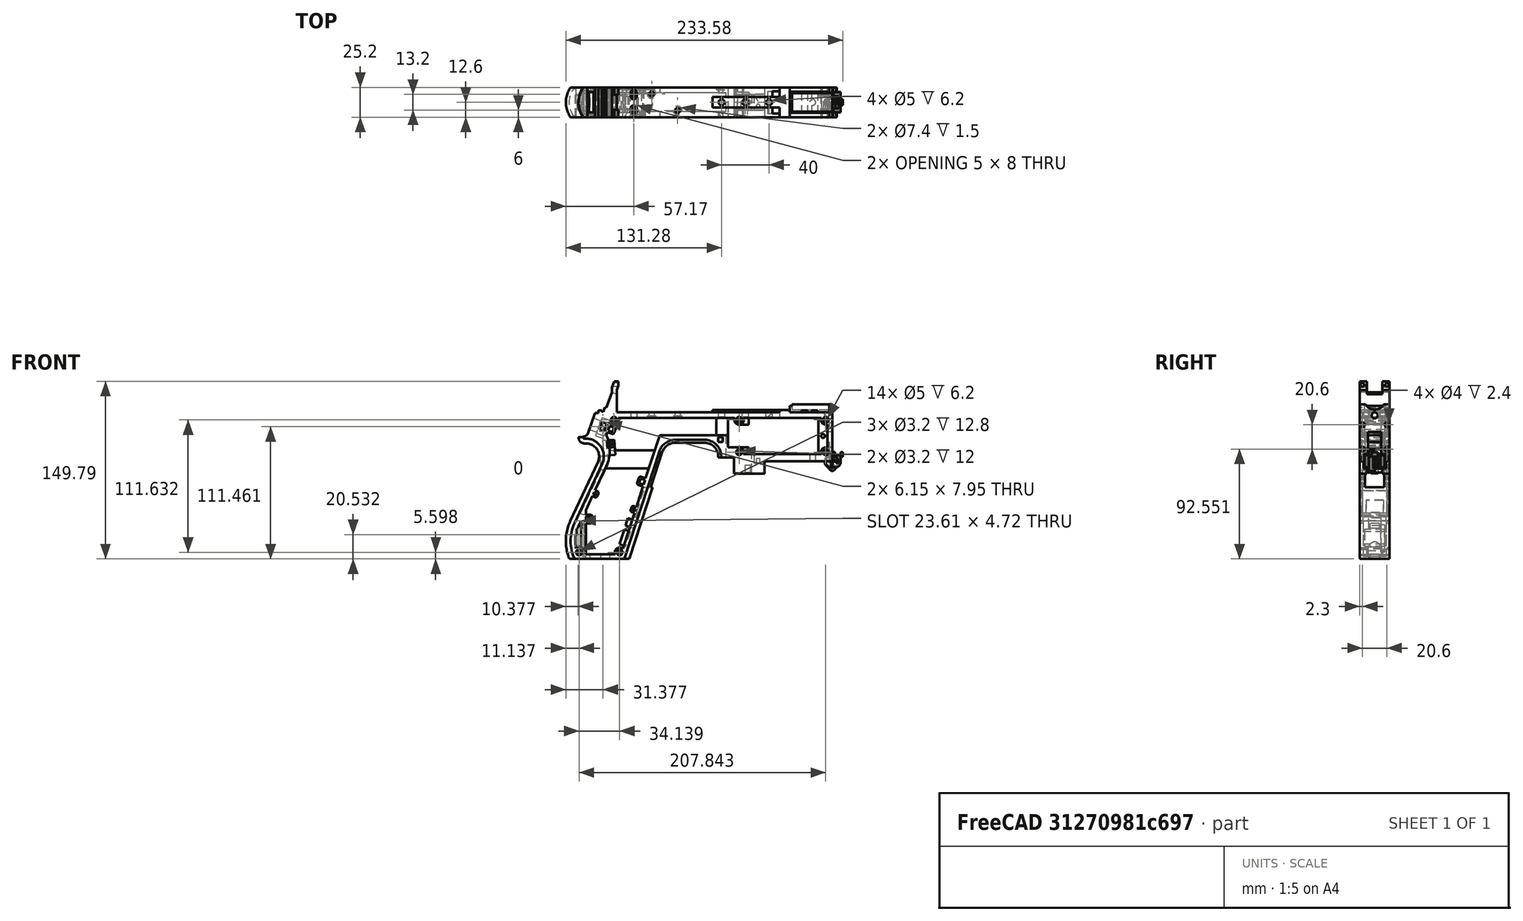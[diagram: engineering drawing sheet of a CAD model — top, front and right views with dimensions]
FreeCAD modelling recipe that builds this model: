
FCSTD DOCUMENT  (FreeCAD 1.0R39319 (Git))
Label: PICON-OF_ver_43
License: All rights reserved
LicenseURL: https://en.wikipedia.org/wiki/All_rights_reserved
objects: Sketcher::SketchObject×112, Part::Extrusion×55, Part::Cut×39, PartDesign::Pad×29, PartDesign::Pocket×18, PartDesign::Chamfer×15, PartDesign::Body×10, PartDesign::Fillet×6, PartDesign::SubtractivePipe×4, Part::Part2DObjectPython×4, PartDesign::SubtractiveLoft×4, PartDesign::Plane×2, PartDesign::SubShapeBinder×2, Part::Sweep×1, PartDesign::ShapeBinder×1, Part::MultiFuse×1, Mesh::Feature×1
note: 567 computed .brp shape members not serialized (recipe doc carries the construction recipe); baked Part::Feature solids carry a one-line shape summary decoded from their .brp

FEATURE [Sketcher::SketchObject] Sketch  label="corpo principale"
  ArcFitTolerance = 1e-06
  AttacherType = Attacher::AttachEngine3D
  AttachmentSupport = -> [XZ_Plane]
  FullyConstrained = true
  MakeInternals = false
  MapMode = 5
  Placement = pos=(0,0,0) rot=(1,0,0;1.5708rad)
  sketch-geometry (65):
    g0: LineSegment StartX=0 StartY=0 StartZ=0 EndX=-57.2 EndY=0 EndZ=0
    g1: LineSegment StartX=-57.2 StartY=0 StartZ=0 EndX=-57.2 EndY=-10.4 EndZ=0
    g2: LineSegment StartX=-57.2 StartY=-10.4 StartZ=0 EndX=-82.8 EndY=-10.4 EndZ=0
    g3: LineSegment StartX=-82.8 StartY=-10.4 StartZ=0 EndX=-82.8 EndY=3.2 EndZ=0
    g4: LineSegment StartX=-82.8 StartY=3.2 StartZ=0 EndX=-93.6 EndY=3.2 EndZ=0
    g5: LineSegment StartX=-93.6 StartY=3.2 StartZ=0 EndX=-93.6 EndY=4 EndZ=0
    g6: LineSegment StartX=-107.6 StartY=18 StartZ=0 EndX=-132.428 EndY=18 EndZ=0
    g7: LineSegment StartX=-145.743 StartY=8.32624 StartZ=0 EndX=-175.232 EndY=-82.4316 EndZ=0
    g8: LineSegment StartX=-175.232 StartY=-82.4316 StartZ=0 EndX=-217.232 EndY=-82.4316 EndZ=0
    g9: LineSegment StartX=-217.232 StartY=-52.1862 StartZ=0 EndX=-193.988 EndY=-2.33927 EndZ=0
    g10: LineSegment StartX=-206.196 StartY=23.0857 StartZ=0 EndX=-199.861 EndY=40.4914 EndZ=0
    g11: LineSegment StartX=-199.861 StartY=40.4914 StartZ=0 EndX=-197.061 EndY=40.4914 EndZ=0
    g12: LineSegment StartX=-197.061 StartY=40.4914 StartZ=0 EndX=-197.061 EndY=42.8914 EndZ=0
    g13: LineSegment StartX=-197.061 StartY=42.8914 StartZ=0 EndX=-194.261 EndY=42.8914 EndZ=0
    g14: LineSegment StartX=-194.261 StartY=42.8914 StartZ=0 EndX=-194.535 EndY=42.1397 EndZ=0
    g15: LineSegment StartX=-194.535 StartY=42.1397 StartZ=0 EndX=-193.031 EndY=41.5924 EndZ=0
    g16: LineSegment StartX=-193.031 StartY=41.5924 StartZ=0 EndX=-191.663 EndY=45.3512 EndZ=0
    g17: LineSegment StartX=-191.663 StartY=45.3512 StartZ=0 EndX=-190.536 EndY=44.9408 EndZ=0
    g18: LineSegment StartX=-190.536 StartY=44.9408 StartZ=0 EndX=-185.747 EndY=58.0965 EndZ=0
    g19: LineSegment StartX=-185.747 StartY=58.0965 StartZ=0 EndX=-185.747 EndY=62.0965 EndZ=0
    g20: LineSegment StartX=-185.747 StartY=62.0965 StartZ=0 EndX=-183.832 EndY=67.3588 EndZ=0
    g21: LineSegment StartX=-183.832 StartY=67.3588 StartZ=0 EndX=-180.232 EndY=67.3588 EndZ=0
    g22: LineSegment StartX=-180.232 StartY=67.3588 StartZ=0 EndX=-180.232 EndY=63.7588 EndZ=0
    g23: LineSegment StartX=-180.232 StartY=63.7588 StartZ=0 EndX=-181.6 EndY=60 EndZ=0
    g24: LineSegment StartX=-181.6 StartY=60 StartZ=0 EndX=-181.6 EndY=41.2 EndZ=0
    g25: LineSegment StartX=-181.6 StartY=41.2 StartZ=0 EndX=-100.8 EndY=41.2 EndZ=0
    g26: LineSegment StartX=-36 StartY=43.2 StartZ=0 EndX=-36 EndY=41.2 EndZ=0
    g27: LineSegment StartX=0 StartY=48 StartZ=0 EndX=0 EndY=0 EndZ=0
    g28: LineSegment StartX=-209.901 StartY=19.85 StartZ=0 EndX=-209.901 EndY=20.1 EndZ=0
    g29: LineSegment StartX=-208.001 StartY=22 StartZ=0 EndX=-207.747 EndY=22 EndZ=0
    g30: LineSegment StartX=-207.583 StartY=19 StartZ=0 EndX=-209.051 EndY=19 EndZ=0
    g31: ArcOfCircle CenterX=-208.001 CenterY=20.1 CenterZ=0 NormalX=0 NormalY=0 NormalZ=1 AngleXU=0 Radius=1.9 StartAngle=1.5708 EndAngle=3.14159
    g32: GeomPoint [constr] X=-209.901 Y=22 Z=0
    g33: ArcOfCircle CenterX=-209.051 CenterY=19.85 CenterZ=0 NormalX=0 NormalY=0 NormalZ=1 AngleXU=0 Radius=0.85 StartAngle=3.14159 EndAngle=4.71239
    g34: GeomPoint [constr] X=-209.901 Y=19 Z=0
    g35: ArcOfCircle CenterX=-207.747 CenterY=23.65 CenterZ=0 NormalX=0 NormalY=0 NormalZ=1 AngleXU=0 Radius=1.65 StartAngle=4.71239 EndAngle=5.93412
    g36: GeomPoint [constr] X=-206.591 Y=22 Z=0
    g37: LineSegment StartX=-4 StartY=6 StartZ=0 EndX=-4 EndY=36.4 EndZ=0
    g38: LineSegment StartX=-4 StartY=36.4 StartZ=0 EndX=-185.2 EndY=36.4 EndZ=0
    g39: LineSegment StartX=-185.2 StartY=36.4 StartZ=0 EndX=-190.441 EndY=22 EndZ=0
    g40: LineSegment StartX=-214.575 StartY=-78.4316 StartZ=0 EndX=-178.142 EndY=-78.4316 EndZ=0
    g41: LineSegment StartX=-178.142 StartY=-78.4316 StartZ=0 EndX=-145.51 EndY=22 EndZ=0
    g42: LineSegment StartX=-145.51 StartY=22 StartZ=0 EndX=-87.91 EndY=22 EndZ=0
    g43: LineSegment StartX=-87.91 StartY=22 StartZ=0 EndX=-87.91 EndY=11.6 EndZ=0
    g44: LineSegment StartX=-87.91 StartY=11.6 StartZ=0 EndX=-80.11 EndY=11.6 EndZ=0
    g45: LineSegment StartX=-80.11 StartY=11.6 StartZ=0 EndX=-80.11 EndY=6 EndZ=0
    g46: LineSegment StartX=-80.11 StartY=6 StartZ=0 EndX=-4 EndY=6 EndZ=0
    g47: LineSegment StartX=-190.363 StartY=-4.02975 StartZ=0 EndX=-213.607 EndY=-53.8767 EndZ=0
    g48: ArcOfCircle CenterX=-132.428 CenterY=4 CenterZ=0 NormalX=0 NormalY=0 NormalZ=1 AngleXU=0 Radius=14 StartAngle=1.5708 EndAngle=2.82743
    g49: GeomPoint [constr] X=-142.6 Y=18 Z=0
    g50: ArcOfCircle CenterX=-107.6 CenterY=4 CenterZ=0 NormalX=0 NormalY=0 NormalZ=1 AngleXU=0 Radius=14 StartAngle=0 EndAngle=1.5708
    g51: GeomPoint [constr] X=-93.6 Y=18 Z=0
    g52: ArcOfCircle CenterX=-184.801 CenterY=-67.3089 CenterZ=0 NormalX=0 NormalY=0 NormalZ=1 AngleXU=0 Radius=35.7833 StartAngle=2.70526 EndAngle=3.57792
    g53: ArcOfCircle CenterX=-207.583 CenterY=4 CenterZ=0 NormalX=0 NormalY=0 NormalZ=1 AngleXU=0 Radius=15 StartAngle=5.84685 EndAngle=7.85398
    g54: LineSegment [constr] StartX=-213.607 StartY=-53.8767 StartZ=0 EndX=-217.232 EndY=-52.1862 EndZ=0
    g55: ArcOfCircle CenterX=-184.801 CenterY=-67.3089 CenterZ=0 NormalX=0 NormalY=0 NormalZ=1 AngleXU=0 Radius=31.7833 StartAngle=2.70526 EndAngle=3.49911
    g56: ArcOfCircle CenterX=-218.095 CenterY=8.90192 CenterZ=0 NormalX=0 NormalY=0 NormalZ=1 AngleXU=0 Radius=30.5989 StartAngle=5.84685 EndAngle=6.72553
    g57: LineSegment StartX=-44.6 StartY=43.2 StartZ=0 EndX=-36 EndY=43.2 EndZ=0
    g58: LineSegment StartX=-100.8 StartY=41.2 StartZ=0 EndX=-44.6 EndY=41.2 EndZ=0
    g59: LineSegment StartX=-44.6 StartY=41.2 StartZ=0 EndX=-44.6 EndY=43.2 EndZ=0
    g60: LineSegment StartX=-2.4 StartY=48 StartZ=0 EndX=0 EndY=48 EndZ=0
    g61: LineSegment StartX=-36 StartY=41.2 StartZ=0 EndX=-2.4 EndY=41.2 EndZ=0
    g62: LineSegment StartX=-2.4 StartY=41.2 StartZ=0 EndX=-2.4 EndY=48 EndZ=0
    g63: LineSegment [constr] StartX=-181.6 StartY=36.4 StartZ=0 EndX=-152.209 EndY=36.4 EndZ=0
    g64: LineSegment [constr] StartX=-181.6 StartY=36.4 StartZ=0 EndX=-130.41 EndY=36.4 EndZ=0
  constraints (183):
    c: Coincident(g-1,g0)
    c: PointOnObject(g0,g-1)
    c: Coincident(g0,g1)
    c: Vertical(g1)
    c: Coincident(g1,g2)
    c: Horizontal(g2)
    c: Coincident(g2,g3)
    c: Vertical(g3)
    c: Coincident(g3,g4)
    c: Coincident(g4,g5)
    c: Vertical(g5)
    c: Horizontal(g6)
    c: Coincident(g7,g8)
    c: Horizontal(g8)
    c: Coincident(g10,g11)
    c: Horizontal(g11)
    c: Coincident(g11,g12)
    c: Vertical(g12)
    c: Coincident(g12,g13)
    c: Horizontal(g13)
    c: Coincident(g13,g14)
    c: Coincident(g14,g15)
    c: Coincident(g15,g16)
    c: Coincident(g16,g17)
    c: Coincident(g17,g18)
    c: Coincident(g18,g19)
    c: Vertical(g19)
    c: Coincident(g19,g20)
    c: Coincident(g20,g21)
    c: Horizontal(g21)
    c: Coincident(g21,g22)
    c: Vertical(g22)
    c: Coincident(g22,g23)
    c: Coincident(g23,g24)
    c: Vertical(g24)
    c: Coincident(g24,g25)
    c: Horizontal(g25)
    c: Coincident(g57,g26)
    c: Vertical(g26)
    c: Coincident(g26,g61)
    c: PointOnObject(g60,g-2)
    c: Coincident(g60,g27)
    c: Coincident(g27,g0)
    c: DistanceY(g27,g27) = 48
    c: DistanceY(g1,g1) = 10.4
    c: DistanceX(g0,g0) = 57.2
    c: DistanceX(g2,g2) = 25.6
    c: Horizontal(g4)
    c: DistanceY(g3,g3) = 13.6
    c: DistanceX(g4,g4) = 10.8
    c: DistanceY(g5,g51) = 14.8
    c: DistanceX(g49,g51) = 49
    c: Distance(g7,g49) = 105.6
    c: DistanceX(g61,g60) = 36
    c: DistanceX(g25,g25) = 80.8
    c: DistanceY(g24,g24) = 18.8
    c: DistanceY(g22,g22) = 3.6
    c: Distance(g23) = 4
    c: Angle(g-1,g23) = 1.22173
    c: DistanceX(g21,g21) = 3.6
    c: Distance(g20) = 5.6
    c: Angle(g-1,g20) = 1.22173
    c: DistanceY(g19,g19) = 4
    c: Distance(g18) = 14
    c: Angle(g-1,g18) = 1.22173
    c: Distance(g17) = 1.2
    c: Distance(g16) = 4
    c: Angle(g16) = 1.22173
    c: Perpendicular(g18,g17)
    c: Distance(g15) = 1.6
    c: Perpendicular(g16,g15)
    c: Distance(g14) = 0.8
    c: DistanceX(g13,g13) = 2.8
    c: Perpendicular(g15,g14)
    c: DistanceY(g12,g12) = 2.4
    c: DistanceX(g11,g11) = 2.8
    c: Distance(g9) = 55
    c: Angle(g9,g-1) = 2.00713
    c: Horizontal(g29)
    c: Vertical(g28)
    c: Horizontal(g30)
    c: PointOnObject(g32,g29)
    c: PointOnObject(g32,g28)
    c: Tangent(g29,g31) = 1.5708
    c: Tangent(g28,g31) = 1.5708
    c: PointOnObject(g34,g28)
    c: PointOnObject(g34,g30)
    c: Tangent(g28,g33) = 1.5708
    c: Tangent(g30,g33) = 1.5708
    c: PointOnObject(g36,g29)
    c: PointOnObject(g36,g10)
    c: Tangent(g29,g35) = -1.5708
    c: Tangent(g10,g35) = -1.5708
    c: Angle(g-1,g10) = 1.22173
    c: Radius(g35) = 1.65
    c: Vertical(g37)
    c: Coincident(g37,g38)
    c: Horizontal(g38)
    c: Coincident(g38,g39)
    c: Horizontal(g40)
    c: Coincident(g40,g41)
    c: Coincident(g41,g42)
    c: Horizontal(g42)
    c: Coincident(g42,g43)
    c: Vertical(g43)
    c: Coincident(g43,g44)
    c: Horizontal(g44)
    c: Coincident(g44,g45)
    c: Vertical(g45)
    c: Coincident(g45,g46)
    c: Coincident(g46,g37)
    c: Horizontal(g46)
    c: DistanceY(g0,g37) = 6
    c: DistanceX(g37,g0) = 4
    c: DistanceY(g37,g25) = 4.8
    c: DistanceX(g38,g38) = 181.2
    c: DistanceX(g42,g42) = 57.6
    c: DistanceY(g49,g41) = 4
    c: DistanceX(g41,g49) = 2.91
    c: DistanceY(g43,g43) = 10.4
    c: DistanceX(g44,g44) = 7.8
    c: DistanceY(g7,g40) = 4
    c: Distance(g47) = 55
    c: Angle(g-1,g39) = 1.22173
    c: PointOnObject(g49,g7)
    c: PointOnObject(g49,g6)
    c: Tangent(g7,g48) = -1.5708
    c: Tangent(g6,g48) = -1.5708
    c: PointOnObject(g51,g5)
    c: PointOnObject(g51,g6)
    c: Tangent(g5,g50) = -1.5708
    c: Tangent(g6,g50) = -1.5708
    c: Radius(g50) = 14
    c: Radius(g48) = 14
    c: DistanceX(g8,g8) = 42
    c: Angle(g7,g-1) = 1.88496
    c: Parallel(g41,g7)
    c: Parallel(g47,g9)
    c: Coincident(g52,g8)
    c: Tangent(g52,g9) = 1.5708
    c: DistanceX(g9,g8) = 0
    c: Tangent(g53,g9) = -1.5708
    c: Tangent(g53,g30) = -1.5708
    c: Diameter(g53) = 30
    c: DistanceY(g53,g0) = -4
    c: Coincident(g54,g47)
    c: Distance(g54) = 4
    c: Coincident(g54,g9)
    c: Coincident(g55,g40)
    c: Tangent(g55,g47) = -1.5708
    c: Coincident(g52,g55)
    c: Coincident(g56,g39)
    c: Tangent(g56,g47) = 1.5708
    c: Horizontal(g57)
    c: DistanceX(g57,g57) = 8.6
    c: Coincident(g58,g25)
    c: Horizontal(g58)
    c: Coincident(g59,g58)
    c: Vertical(g59)
    c: DistanceY(g58,g57) = 2
    c: DistanceX(g58,g58) = 56.2
    c: Coincident(g59,g57)
    c: DistanceY(g41,g36) = 0
    c: DistanceY(g36,g39) = 0
    c: DistanceY(g28,g28) = 0.25
    c: DistanceX(g30,g36) = 2.46
    c: DistanceX(g28,g29) = 1.9
    c: Coincident(g62,g60)
    c: Horizontal(g60)
    c: DistanceX(g62,g27) = 2.4
    c: Coincident(g61,g62)
    c: DistanceY(g26,g26) = 2
    c: Vertical(g62)
    c: DistanceY(g61,g60) = 6.8
    c: Horizontal(g61)
    c: Distance(g63) = 29.391
    c: PointOnObject(g63,g38)
    c: PointOnObject(g63,g38)
    c: Distance(g64) = 51.19
    c: PointOnObject(g64,g38)
    c: PointOnObject(g64,g38)
    c: DistanceX(g24,g63) = 0
    c: DistanceX(g24,g64) = 0
FEATURE [Part::Extrusion] Extrude  label="Extrude corpo principale"
  Base = -> Sketch
  Dir = (0,-1,2e-16)
  DirMode = 2
  FaceMakerClass = Part::FaceMakerBullseye
  FaceMakerMode = 3
  LengthFwd = 25.2
  LengthRev = 12.6
  Solid = true
  Symmetric = true
FEATURE [Sketcher::SketchObject] Sketch002  label="scavo grilletto"
  ArcFitTolerance = 1e-06
  AttachmentSupport = -> [XZ_Plane]
  ExternalGeometry = -> [Sketch]
  FullyConstrained = true
  MakeInternals = false
  MapMode = 5
  Placement = pos=(0,0,0) rot=(1,0,0;1.5708rad)
  sketch-geometry (4):
    g0: LineSegment StartX=-89.51 StartY=22 StartZ=0 EndX=-152.71 EndY=22 EndZ=0
    g1: LineSegment StartX=-152.71 StartY=22 StartZ=0 EndX=-167.006 EndY=-22 EndZ=0
    g2: LineSegment StartX=-167.006 StartY=-22 StartZ=0 EndX=-89.51 EndY=-22 EndZ=0
    g3: LineSegment StartX=-89.51 StartY=-22 StartZ=0 EndX=-89.51 EndY=22 EndZ=0
  constraints (12):
    c: Horizontal(g0)
    c: Coincident(g0,g1)
    c: Coincident(g1,g2)
    c: Horizontal(g2)
    c: Coincident(g2,g3)
    c: Coincident(g3,g0)
    c: Vertical(g3)
    c: Angle(g1,g0) = 1.88496
    c: DistanceY(g3,g3) = 44
    c: DistanceX(g0,g0) = 63.2
    c: DistanceX(g0,g-3) = 1.6
    c: DistanceY(g-3,g0) = 0
FEATURE [Sketcher::SketchObject] Sketch004  label="traiettoria arrotondamento impugnatura anteriore"
  ArcFitTolerance = 1e-06
  AttachmentSupport = -> [XZ_Plane]
  ExternalGeometry = -> [Sketch]
  FullyConstrained = true
  MakeInternals = false
  MapMode = 5
  Placement = pos=(0,0,0) rot=(1,0,0;1.5708rad)
  sketch-geometry (13):
    g0: LineSegment StartX=-175.232 StartY=-82.4316 StartZ=0 EndX=-145.743 EndY=8.32624 EndZ=0
    g1: LineSegment StartX=-93.6 StartY=3.2 StartZ=0 EndX=-93.6 EndY=4 EndZ=0
    g2: LineSegment StartX=-132.428 StartY=18 StartZ=0 EndX=-107.6 EndY=18 EndZ=0
    g3: ArcOfCircle CenterX=-132.428 CenterY=4 CenterZ=0 NormalX=0 NormalY=0 NormalZ=1 AngleXU=0 Radius=14 StartAngle=1.5708 EndAngle=2.82743
    g4: ArcOfCircle CenterX=-107.6 CenterY=4 CenterZ=0 NormalX=0 NormalY=0 NormalZ=1 AngleXU=0 Radius=14 StartAngle=0 EndAngle=1.5708
    g5: LineSegment StartX=-175.232 StartY=-82.4316 StartZ=0 EndX=-217.232 EndY=-82.4316 EndZ=0
    g6: LineSegment StartX=-217.232 StartY=-52.1862 StartZ=0 EndX=-193.988 EndY=-2.33927 EndZ=0
    g7: LineSegment StartX=-209.051 StartY=19 StartZ=0 EndX=-207.583 EndY=19 EndZ=0
    g8: LineSegment StartX=-209.901 StartY=20.1 StartZ=0 EndX=-209.901 EndY=19.85 EndZ=0
    g9: ArcOfCircle CenterX=-184.801 CenterY=-67.3089 CenterZ=0 NormalX=0 NormalY=0 NormalZ=1 AngleXU=0 Radius=35.7833 StartAngle=2.70526 EndAngle=3.57792
    g10: ArcOfCircle CenterX=-207.583 CenterY=4 CenterZ=0 NormalX=0 NormalY=0 NormalZ=1 AngleXU=0 Radius=15 StartAngle=5.84685 EndAngle=7.85398
    g11: ArcOfCircle CenterX=-209.051 CenterY=19.85 CenterZ=0 NormalX=0 NormalY=0 NormalZ=1 AngleXU=0 Radius=0.85 StartAngle=3.14159 EndAngle=4.71239
    g12: ArcOfCircle CenterX=-208.001 CenterY=20.1 CenterZ=0 NormalX=0 NormalY=0 NormalZ=1 AngleXU=0 Radius=1.9 StartAngle=1.5708 EndAngle=3.14159
  constraints (26):
    c: Coincident(g0,g-3)
    c: Coincident(g0,g-6)
    c: Coincident(g1,g-8)
    c: Coincident(g1,g-7)
    c: Coincident(g2,g-5)
    c: Coincident(g2,g-4)
    c: Coincident(g3,g2)
    c: Tangent(g3,g0) = 1.5708
    c: Coincident(g4,g1)
    c: Tangent(g4,g2) = 1.5708
    c: Coincident(g5,g0)
    c: Coincident(g5,g-9)
    c: Coincident(g6,g-12)
    c: Coincident(g6,g-11)
    c: Coincident(g7,g-15)
    c: Coincident(g7,g-14)
    c: Coincident(g8,g-16)
    c: Coincident(g8,g-17)
    c: Tangent(g9,g6) = 1.5708
    c: Coincident(g9,g5)
    c: Coincident(g10,g7)
    c: Tangent(g10,g6) = -1.5708
    c: Tangent(g11,g7) = -1.5708
    c: Coincident(g11,g8)
    c: Tangent(g12,g8) = -1.5708
    c: Coincident(g12,g-17)
FEATURE [PartDesign::Plane] DatumPlane  label="Piano per disegno arrotondamento impugnatura"
  AttachmentSupport = -> [Sketch]
  Length = 73.6581
  MapMode = 7
  Placement = pos=(-145.743,1.8e-15,8.32624) rot=(0.154555,0.154555,0.97582;1.59527rad)
  ResizeMode = 0
  Width = 303.511
FEATURE [Sketcher::SketchObject] Sketch005  label="forma arrotondamento impugnatura anteriore"
  ArcFitTolerance = 1e-06
  AttachmentSupport = -> [DatumPlane]
  FullyConstrained = true
  MakeInternals = false
  MapMode = 5
  Placement = pos=(-145.743,1.8e-15,8.32624) rot=(0.154555,0.154555,0.97582;1.59527rad)
  sketch-geometry (5):
    g0: GeomPoint [constr] X=0 Y=-4 Z=0
    g1: GeomPoint [constr] X=-12.6 Y=7.1e-15 Z=0
    g2: GeomPoint [constr] X=12.6 Y=4.97e-14 Z=0
    g3: LineSegment StartX=-12.6 StartY=7.1e-15 StartZ=0 EndX=12.6 EndY=4.97e-14 EndZ=0
    g4: ArcOfCircle CenterX=-3.88e-14 CenterY=17.845 CenterZ=0 NormalX=0 NormalY=0 NormalZ=1 AngleXU=0 Radius=21.845 StartAngle=4.09759 EndAngle=5.32718
  constraints (11):
    c: DistanceY(g0,g-1) = 4
    c: DistanceX(g-1,g0) = 0
    c: DistanceX(g1,g-1) = 12.6
    c: DistanceX(g-1,g2) = 12.6
    c: DistanceY(g-1,g2) = 0
    c: DistanceY(g-1,g1) = 0
    c: Coincident(g3,g1)
    c: Coincident(g3,g2)
    c: Coincident(g4,g1)
    c: Coincident(g4,g2)
    c: PointOnObject(g0,g4)
FEATURE [Part::Sweep] Sweep  label="Sweep impugnatura"
  Frenet = true
  Sections = -> [Sketch005]
  Solid = true
  Spine = -> Sketch [Edge32,Edge33,Edge34,Edge35,Edge36,Edge37,Edge38,Edge39,Edge40,Edge41,Edge42,Edge43,Edge44]
  Transition = 1
FEATURE [Sketcher::SketchObject] Sketch008  label="buchi e pulizie varie"
  ArcFitTolerance = 1e-06
  AttachmentSupport = -> [XZ_Plane]
  ExternalGeometry = -> [Sketch]
  FullyConstrained = true
  MakeInternals = false
  MapMode = 5
  Placement = pos=(0,0,0) rot=(1,0,0;1.5708rad)
  sketch-geometry (26):
    g0: LineSegment StartX=-96.278 StartY=20.155 StartZ=0 EndX=-92.278 EndY=20.155 EndZ=0
    g1: LineSegment StartX=-92.278 StartY=20.155 StartZ=0 EndX=-92.278 EndY=16.155 EndZ=0
    g2: LineSegment StartX=-92.278 StartY=16.155 StartZ=0 EndX=-96.278 EndY=16.155 EndZ=0
    g3: LineSegment StartX=-96.278 StartY=16.155 StartZ=0 EndX=-96.278 EndY=20.155 EndZ=0
    g4: LineSegment StartX=-222.232 StartY=-82.4316 StartZ=0 EndX=-170.232 EndY=-82.4316 EndZ=0
    g5: LineSegment StartX=-170.232 StartY=-82.4316 StartZ=0 EndX=-170.232 EndY=-86.4316 EndZ=0
    g6: LineSegment StartX=-170.232 StartY=-86.4316 StartZ=0 EndX=-222.232 EndY=-86.4316 EndZ=0
    g7: LineSegment StartX=-222.232 StartY=-86.4316 StartZ=0 EndX=-222.232 EndY=-82.4316 EndZ=0
    g8: LineSegment StartX=-213.901 StartY=20.1 StartZ=0 EndX=-213.901 EndY=26 EndZ=0
    g9: LineSegment StartX=-213.901 StartY=26 StartZ=0 EndX=-206.196 EndY=26 EndZ=0
    g10: LineSegment StartX=-17.4 StartY=42.8 StartZ=0 EndX=-12.4 EndY=42.8 EndZ=0
    g11: LineSegment StartX=-12.4 StartY=42.8 StartZ=0 EndX=-12.4 EndY=41.2 EndZ=0
    g12: LineSegment StartX=-12.4 StartY=41.2 StartZ=0 EndX=-17.4 EndY=41.2 EndZ=0
    g13: LineSegment StartX=-17.4 StartY=41.2 StartZ=0 EndX=-17.4 EndY=42.8 EndZ=0
    g14: LineSegment StartX=-25.9 StartY=42.8 StartZ=0 EndX=-20.9 EndY=42.8 EndZ=0
    g15: LineSegment StartX=-20.9 StartY=42.8 StartZ=0 EndX=-20.9 EndY=41.2 EndZ=0
    g16: LineSegment StartX=-20.9 StartY=41.2 StartZ=0 EndX=-25.9 EndY=41.2 EndZ=0
    g17: LineSegment StartX=-25.9 StartY=41.2 StartZ=0 EndX=-25.9 EndY=42.8 EndZ=0
    g18: GeomPoint [constr] X=-206.196 Y=23.0857 Z=0
    g19: GeomPoint [constr] X=-213.901 Y=20.1 Z=0
    g20: BSplineCurve PolesCount=4 KnotsCount=2 Degree=3 IsPeriodic=0
    g21-g24: Circle [constr] x4 (B-spline internal-alignment scaffolding for g20; pole/knot coordinates omitted)
    g25: LineSegment StartX=-206.196 StartY=26 StartZ=0 EndX=-206.196 EndY=23.0857 EndZ=0
  constraints (73):
    c: Horizontal(g0)
    c: Coincident(g1,g0)
    c: Vertical(g1)
    c: Coincident(g2,g1)
    c: Horizontal(g2)
    c: Coincident(g3,g2)
    c: Coincident(g3,g0)
    c: Vertical(g3)
    c: DistanceX(g0,g-4) = 4.368
    c: DistanceY(g0,g-4) = 1.845
    c: DistanceY(g1,g1) = 4
    c: DistanceX(g2,g2) = 4
    c: Horizontal(g4)
    c: Coincident(g5,g4)
    c: Vertical(g5)
    c: Coincident(g6,g5)
    c: Horizontal(g6)
    c: Coincident(g7,g6)
    c: Coincident(g7,g4)
    c: Vertical(g7)
    c: DistanceY(g7,g7) = 4
    c: DistanceX(g4,g-5) = 5
    c: DistanceX(g-5,g4) = 5
    c: DistanceY(g4,g-5) = 0
    c: Coincident(g9,g8)
    c: Parallel(g9,g-6)
    c: DistanceX(g8,g-8) = 4
    c: Horizontal(g10)
    c: Coincident(g11,g10)
    c: Vertical(g11)
    c: Coincident(g12,g11)
    c: Horizontal(g12)
    c: Coincident(g13,g12)
    c: Coincident(g13,g10)
    c: Vertical(g13)
    c: Horizontal(g14)
    c: Coincident(g15,g14)
    c: Vertical(g15)
    c: Coincident(g16,g15)
    c: Horizontal(g16)
    c: Coincident(g17,g16)
    c: Coincident(g17,g14)
    c: Vertical(g17)
    c: DistanceY(g11,g10) = 1.6
    c: DistanceX(g10,g10) = 5
    c: DistanceY(g15,g14) = 1.6
    c: DistanceX(g14,g14) = 5
    c: DistanceX(g15,g12) = 3.5
    c: DistanceX(g11,g-9) = 10
    c: DistanceY(g-9,g11) = 0
    c: DistanceY(g-9,g15) = 0
    c: Perpendicular(g8,g9)
    c: DistanceY(g-7,g9) = 4
    c: DistanceY(g8,g-8) = 0
    c: InternalAlignment(g18,g20)
    c: InternalAlignment(g19,g20)
    c: InternalAlignment(g21,g20)
    c: Weight(g21) = 1
    c: InternalAlignment(g22,g20)
    c: Equal(g22,g21)
    c: InternalAlignment(g23,g20)
    c: Equal(g23,g21)
    c: InternalAlignment(g24,g20)
    c: Equal(g24,g21)
    c: Coincident(g18,g-12)
    c: Coincident(g19,g8)
    c: Coincident(g25,g9)
    c: Coincident(g25,g20)
    c: Vertical(g25)
    c: DistanceY(g20,g23) = 0
    c: DistanceY(g22,g18) = 2.26
    c: DistanceX(g22,g18) = 0.93
    c: DistanceX(g20,g23) = 2.9
FEATURE [Part::Extrusion] Extrude004  label="Extrude Buchi e pulizie varie"
  Base = -> Sketch008
  Dir = (0,-1,2e-16)
  DirMode = 2
  FaceMakerClass = Part::FaceMakerBullseye
  FaceMakerMode = 3
  LengthFwd = 25.2
  LengthRev = 0
  Solid = true
  Symmetric = true
FEATURE [Sketcher::SketchObject] Sketch009  label="rinforzi"
  ArcFitTolerance = 1e-06
  AttachmentSupport = -> [XZ_Plane]
  ExternalGeometry = -> [Sketch]
  FullyConstrained = true
  MakeInternals = false
  MapMode = 5
  Placement = pos=(0,0,0) rot=(1,0,0;1.5708rad)
  sketch-geometry (9):
    g0: LineSegment StartX=-87.91 StartY=22 StartZ=0 EndX=-87.91 EndY=36.4 EndZ=0
    g1: LineSegment StartX=-87.91 StartY=36.4 StartZ=0 EndX=-97.91 EndY=36.4 EndZ=0
    g2: LineSegment StartX=-97.91 StartY=36.4 StartZ=0 EndX=-97.91 EndY=22 EndZ=0
    g3: LineSegment StartX=-97.91 StartY=22 StartZ=0 EndX=-87.91 EndY=22 EndZ=0
    g4: LineSegment StartX=-149.713 StartY=9.06563 StartZ=0 EndX=-154.586 EndY=-5.93437 EndZ=0
    g5: LineSegment StartX=-154.586 StartY=-5.93437 StartZ=0 EndX=-191.863 EndY=-5.93437 EndZ=0
    g6: LineSegment StartX=-191.863 StartY=-5.93437 StartZ=0 EndX=-191.863 EndY=9.06563 EndZ=0
    g7: LineSegment StartX=-191.863 StartY=9.06563 StartZ=0 EndX=-149.713 EndY=9.06563 EndZ=0
    g8: LineSegment [constr] StartX=-145.51 StartY=22 StartZ=0 EndX=-149.713 EndY=9.06563 EndZ=0
  constraints (25):
    c: Vertical(g0)
    c: Coincident(g1,g0)
    c: Horizontal(g1)
    c: Coincident(g2,g1)
    c: Vertical(g2)
    c: Coincident(g3,g2)
    c: Coincident(g3,g0)
    c: Horizontal(g3)
    c: Coincident(g0,g-4)
    c: DistanceX(g3,g3) = 10
    c: DistanceY(g0,g-3) = 0
    c: Coincident(g5,g4)
    c: Horizontal(g5)
    c: Coincident(g6,g5)
    c: Vertical(g6)
    c: Coincident(g7,g6)
    c: Coincident(g7,g4)
    c: Horizontal(g7)
    c: Distance(g8) = 13.6
    c: Parallel(g-6,g8)
    c: Coincident(g-6,g8)
    c: Parallel(g4,g-6)
    c: DistanceY(g4,g4) = 15
    c: Coincident(g4,g8)
    c: DistanceX(g-5,g5) = -1.5
FEATURE [Part::Extrusion] Extrude001  label="Extrude scavo grilletto"
  Base = -> Sketch002
  Dir = (0,-1,2e-16)
  DirMode = 2
  FaceMakerClass = Part::FaceMakerBullseye
  FaceMakerMode = 3
  LengthFwd = 16
  LengthRev = 0
  Solid = true
  Symmetric = true
FEATURE [Part::Extrusion] Extrude005  label="Extrude Rinforzi"
  Base = -> Sketch009
  Dir = (0,-1,2e-16)
  DirMode = 2
  FaceMakerClass = Part::FaceMakerBullseye
  FaceMakerMode = 3
  LengthFwd = 2
  LengthRev = 0
  Placement = pos=(0,12.6,0) rot=(0,0,1;0rad)
  Solid = true
  Symmetric = false
FEATURE [PartDesign::ShapeBinder] CopyCut
  TraceSupport = false
FEATURE [PartDesign::Plane] DatumPlane001
  AttachmentSupport = -> [CopyCut]
  Length = 283.944
  MapMode = 5
  Placement = pos=(0,12.6,0) rot=(0,0.707107,0.707107;3.14159rad)
  ResizeMode = 0
  Width = 188.15
FEATURE [Sketcher::SketchObject] Sketch010  label="buco neopixel"
  ArcFitTolerance = 1e-06
  AttachmentSupport = -> [XZ_Plane]
  ExternalGeometry = -> [Sketch]
  FullyConstrained = true
  MakeInternals = false
  MapMode = 5
  Placement = pos=(0,0,0) rot=(1,0,0;1.5708rad)
  sketch-geometry (5):
    g0: LineSegment [constr] StartX=-199.861 StartY=40.4914 StartZ=0 EndX=-201.368 EndY=36.3521 EndZ=0
    g1: LineSegment StartX=-201.368 StartY=36.3521 StartZ=0 EndX=-204.932 EndY=26.5605 EndZ=0
    g2: LineSegment StartX=-201.368 StartY=36.3521 StartZ=0 EndX=-180.2 EndY=28.6477 EndZ=0
    g3: LineSegment StartX=-180.2 StartY=28.6477 StartZ=0 EndX=-183.764 EndY=18.8561 EndZ=0
    g4: LineSegment StartX=-183.764 StartY=18.8561 StartZ=0 EndX=-204.932 EndY=26.5605 EndZ=0
  constraints (14):
    c: Parallel(g0,g-3)
    c: Distance(g0) = 4.405
    c: Coincident(g0,g-3)
    c: Coincident(g2,g1)
    c: Coincident(g3,g2)
    c: Coincident(g4,g3)
    c: Coincident(g4,g1)
    c: Parallel(g1,g-3)
    c: Distance(g1) = 10.42
    c: Coincident(g1,g0)
    c: Parallel(g2,g4)
    c: Perpendicular(g1,g2)
    c: DistanceX(g-4,g2) = 5
    c: Parallel(g3,g1)
FEATURE [Part::Extrusion] Extrude006  label="Extrude buco neopixel"
  Base = -> Sketch010
  Dir = (0,-1,2e-16)
  DirMode = 2
  FaceMakerClass = Part::FaceMakerBullseye
  FaceMakerMode = 3
  LengthFwd = 17.2
  LengthRev = 0
  Solid = true
  Symmetric = true
FEATURE [Sketcher::SketchObject] Sketch011  label="fermo grilletto"
  ArcFitTolerance = 1e-06
  AttachmentSupport = -> [XZ_Plane]
  ExternalGeometry = -> [Sketch]
  FullyConstrained = true
  MakeInternals = false
  MapMode = 5
  Placement = pos=(0,0,0) rot=(1,0,0;1.5708rad)
  sketch-geometry (18):
    g0: LineSegment [constr] StartX=-145.51 StartY=22 StartZ=0 EndX=-157.347 EndY=-14.4293 EndZ=0
    g1: LineSegment [constr] StartX=-157.347 StartY=-14.4293 StartZ=0 EndX=-157.841 EndY=-15.951 EndZ=0
    g2: LineSegment StartX=-161.151 StartY=-13.1932 StartZ=0 EndX=-155.825 EndY=-14.9237 EndZ=0
    g3: LineSegment StartX=-163.167 StartY=-14.2205 StartZ=0 EndX=-164.403 EndY=-18.0247 EndZ=0
    g4: LineSegment StartX=-163.376 StartY=-20.0408 StartZ=0 EndX=-158.05 EndY=-21.7713 EndZ=0
    g5: LineSegment StartX=-158.05 StartY=-21.7713 StartZ=0 EndX=-155.825 EndY=-14.9237 EndZ=0
    g6: LineSegment StartX=-161.645 StartY=-14.7149 StartZ=0 EndX=-157.841 EndY=-15.951 EndZ=0
    g7: LineSegment StartX=-157.841 StartY=-15.951 StartZ=0 EndX=-159.077 EndY=-19.7552 EndZ=0
    g8: LineSegment StartX=-159.077 StartY=-19.7552 StartZ=0 EndX=-162.881 EndY=-18.5191 EndZ=0
    g9: LineSegment StartX=-162.881 StartY=-18.5191 StartZ=0 EndX=-161.645 EndY=-14.7149 EndZ=0
    g10: LineSegment [constr] StartX=-161.645 StartY=-14.7149 StartZ=0 EndX=-161.151 EndY=-13.1932 EndZ=0
    g11: LineSegment [constr] StartX=-159.077 StartY=-19.7552 StartZ=0 EndX=-157.555 EndY=-20.2496 EndZ=0
    g12: LineSegment [constr] StartX=-159.077 StartY=-19.7552 StartZ=0 EndX=-159.572 EndY=-21.2769 EndZ=0
    g13: LineSegment [constr] StartX=-161.645 StartY=-14.7149 StartZ=0 EndX=-163.167 EndY=-14.2205 EndZ=0
    g14: ArcOfCircle CenterX=-161.645 CenterY=-14.7149 CenterZ=0 NormalX=0 NormalY=0 NormalZ=1 AngleXU=0 Radius=1.6 StartAngle=1.25664 EndAngle=2.82743
    g15: GeomPoint [constr] X=-162.673 Y=-12.6988 Z=0
    g16: ArcOfCircle CenterX=-162.881 CenterY=-18.5191 CenterZ=0 NormalX=0 NormalY=0 NormalZ=1 AngleXU=0 Radius=1.6 StartAngle=2.82743 EndAngle=4.39823
    g17: GeomPoint [constr] X=-164.897 Y=-19.5464 Z=0
  constraints (48):
    c: Parallel(g0,g-3)
    c: Distance(g0) = 38.304
    c: Coincident(g0,g-3)
    c: Parallel(g1,g-3)
    c: Distance(g1) = 1.6
    c: Coincident(g1,g0)
    c: Coincident(g5,g4)
    c: Coincident(g5,g2)
    c: Coincident(g7,g6)
    c: Coincident(g8,g7)
    c: Coincident(g9,g8)
    c: Coincident(g9,g6)
    c: Parallel(g7,g-3)
    c: Parallel(g9,g7)
    c: Perpendicular(g6,g7)
    c: Parallel(g6,g8)
    c: Distance(g6) = 4
    c: Distance(g9) = 4
    c: Parallel(g5,g7)
    c: Parallel(g9,g3)
    c: Parallel(g2,g6)
    c: Parallel(g4,g8)
    c: Parallel(g13,g6)
    c: Parallel(g10,g9)
    c: Parallel(g11,g8)
    c: Parallel(g12,g7)
    c: Distance(g10) = 1.6
    c: Distance(g13) = 1.6
    c: Distance(g12) = 1.6
    c: Distance(g11) = 1.6
    c: Coincident(g10,g6)
    c: Coincident(g13,g6)
    c: Coincident(g12,g7)
    c: Coincident(g11,g7)
    c: Distance(g10,g15) = 1.6
    c: Distance(g15,g13) = 1.6
    c: Distance(g4,g12) = 1.6
    c: Distance(g4,g11) = 1.6
    c: PointOnObject(g15,g2)
    c: Tangent(g3,g14) = -1.5708
    c: Tangent(g2,g14) = 1.5708
    c: PointOnObject(g17,g4)
    c: PointOnObject(g17,g3)
    c: Tangent(g4,g16) = -1.5708
    c: Tangent(g3,g16) = -1.5708
    c: Equal(g16,g14)
    c: Coincident(g16,g8)
    c: Coincident(g6,g1)
FEATURE [Part::Extrusion] Extrude007  label="Extrude fermo grilletto"
  Base = -> Sketch011
  Dir = (0,-1,2e-16)
  DirMode = 2
  FaceMakerClass = Part::FaceMakerBullseye
  FaceMakerMode = 3
  LengthFwd = 25.2
  LengthRev = 0
  Solid = true
  Symmetric = true
FEATURE [Sketcher::SketchObject] Sketch012  label="buco oled"
  ArcFitTolerance = 1e-06
  AttachmentSupport = -> [XZ_Plane]
  ExternalGeometry = -> [Sketch]
  FullyConstrained = true
  MakeInternals = false
  MapMode = 5
  Placement = pos=(0,0,0) rot=(1,0,0;1.5708rad)
  sketch-geometry (4):
    g0: LineSegment StartX=-185.747 StartY=58.0965 StartZ=0 EndX=-180.232 EndY=56.0891 EndZ=0
    g1: LineSegment StartX=-185.747 StartY=58.0965 StartZ=0 EndX=-185.747 EndY=67.3588 EndZ=0
    g2: LineSegment StartX=-185.747 StartY=67.3588 StartZ=0 EndX=-180.232 EndY=67.3588 EndZ=0
    g3: LineSegment StartX=-180.232 StartY=67.3588 StartZ=0 EndX=-180.232 EndY=56.0891 EndZ=0
  constraints (10):
    c: Coincident(g1,g0)
    c: Coincident(g2,g1)
    c: Coincident(g3,g2)
    c: Coincident(g3,g0)
    c: Parallel(g1,g-5)
    c: Perpendicular(g-3,g0)
    c: Parallel(g2,g-6)
    c: Parallel(g3,g-4)
    c: Coincident(g0,g-5)
    c: Coincident(g2,g-6)
FEATURE [Part::Extrusion] Extrude008  label="Extrude buco oled"
  Base = -> Sketch012
  Dir = (0,-1,2e-16)
  DirMode = 2
  FaceMakerClass = Part::FaceMakerBullseye
  FaceMakerMode = 3
  LengthFwd = 12.8
  LengthRev = 0
  Solid = true
  Symmetric = true
FEATURE [Sketcher::SketchObject] Sketch013  label="buco pompa"
  ArcFitTolerance = 1e-06
  AttachmentSupport = -> [XZ_Plane]
  ExternalGeometry = -> [Sketch]
  FullyConstrained = true
  MakeInternals = false
  MapMode = 5
  Placement = pos=(0,0,0) rot=(1,0,0;1.5708rad)
  sketch-geometry (8):
    g0: LineSegment StartX=-82.8 StartY=-10.4 StartZ=0 EndX=-82.8 EndY=-9.6 EndZ=0
    g1: LineSegment StartX=-82.8 StartY=-9.6 StartZ=0 EndX=-67.9 EndY=-9.6 EndZ=0
    g2: LineSegment StartX=-67.9 StartY=-9.6 StartZ=0 EndX=-67.9 EndY=6 EndZ=0
    g3: LineSegment StartX=-67.9 StartY=6 StartZ=0 EndX=-65.9 EndY=6 EndZ=0
    g4: LineSegment StartX=-65.9 StartY=6 StartZ=0 EndX=-65.9 EndY=-1.7 EndZ=0
    g5: LineSegment StartX=-65.9 StartY=-1.7 StartZ=0 EndX=-57.2 EndY=-1.7 EndZ=0
    g6: LineSegment StartX=-57.2 StartY=-1.7 StartZ=0 EndX=-57.2 EndY=-10.4 EndZ=0
    g7: LineSegment StartX=-57.2 StartY=-10.4 StartZ=0 EndX=-82.8 EndY=-10.4 EndZ=0
  constraints (22):
    c: Vertical(g0)
    c: Coincident(g1,g0)
    c: Horizontal(g1)
    c: Coincident(g2,g1)
    c: Vertical(g2)
    c: Coincident(g3,g2)
    c: Horizontal(g3)
    c: Coincident(g4,g3)
    c: Vertical(g4)
    c: Coincident(g5,g4)
    c: Horizontal(g5)
    c: Coincident(g6,g5)
    c: Vertical(g6)
    c: Coincident(g7,g6)
    c: Coincident(g7,g0)
    c: DistanceY(g0,g0) = 0.8
    c: DistanceY(g6,g6) = 8.7
    c: DistanceX(g1,g1) = 14.9
    c: DistanceX(g3,g3) = 2
    c: Coincident(g0,g-4)
    c: DistanceY(g2,g-6) = 0
    c: Coincident(g6,g-5)
FEATURE [Part::Extrusion] Extrude009  label="Extrude buco pompa"
  Base = -> Sketch013
  Dir = (0,-1,2e-16)
  DirMode = 2
  FaceMakerClass = Part::FaceMakerBullseye
  FaceMakerMode = 3
  LengthFwd = 13.2
  LengthRev = 0
  Solid = true
  Symmetric = true
FEATURE [Sketcher::SketchObject] Sketch014  label="buco frontale"
  ArcFitTolerance = 1e-06
  AttachmentSupport = -> [XZ_Plane]
  ExternalGeometry = -> [Sketch]
  FullyConstrained = true
  MakeInternals = false
  MapMode = 5
  Placement = pos=(0,0,0) rot=(1,0,0;1.5708rad)
  sketch-geometry (10):
    g0: LineSegment StartX=0 StartY=0 StartZ=0 EndX=0 EndY=24.671 EndZ=0
    g1: LineSegment StartX=0 StartY=24.671 StartZ=0 EndX=-4 EndY=24.671 EndZ=0
    g2: LineSegment StartX=-4 StartY=24.671 StartZ=0 EndX=-4 EndY=16 EndZ=0
    g3: LineSegment StartX=-4 StartY=16 StartZ=0 EndX=-2.4 EndY=16 EndZ=0
    g4: LineSegment StartX=-2.4 StartY=16 StartZ=0 EndX=-2.4 EndY=10 EndZ=0
    g5: LineSegment StartX=-2.4 StartY=10 StartZ=0 EndX=-12 EndY=10 EndZ=0
    g6: LineSegment StartX=-12 StartY=10 StartZ=0 EndX=-12 EndY=6 EndZ=0
    g7: LineSegment StartX=-12 StartY=6 StartZ=0 EndX=-2.4 EndY=6 EndZ=0
    g8: LineSegment StartX=-2.4 StartY=6 StartZ=0 EndX=-2.4 EndY=0 EndZ=0
    g9: LineSegment StartX=-2.4 StartY=0 StartZ=0 EndX=0 EndY=0 EndZ=0
  constraints (29):
    c: Vertical(g0)
    c: Coincident(g1,g0)
    c: Horizontal(g1)
    c: Coincident(g2,g1)
    c: Vertical(g2)
    c: Coincident(g3,g2)
    c: Horizontal(g3)
    c: Coincident(g4,g3)
    c: Vertical(g4)
    c: Coincident(g5,g4)
    c: Horizontal(g5)
    c: Coincident(g6,g5)
    c: Vertical(g6)
    c: Coincident(g7,g6)
    c: Coincident(g8,g7)
    c: Vertical(g8)
    c: Coincident(g9,g8)
    c: Coincident(g9,g0)
    c: Horizontal(g9)
    c: DistanceY(g0,g0) = 24.671
    c: Horizontal(g7)
    c: DistanceY(g6,g6) = 4
    c: DistanceY(g4,g4) = 6
    c: DistanceX(g9,g9) = 2.4
    c: Coincident(g0,g-1)
    c: DistanceY(g-3,g7) = 0
    c: DistanceX(g8,g4) = 0
    c: DistanceX(g-3,g1) = 0
    c: DistanceX(g6,g-3) = 8
FEATURE [Part::Extrusion] Extrude010  label="Extrude buco frontale"
  Base = -> Sketch014
  Dir = (0,-1,2e-16)
  DirMode = 2
  FaceMakerClass = Part::FaceMakerBullseye
  FaceMakerMode = 3
  LengthFwd = 11.2
  LengthRev = 0
  Solid = true
  Symmetric = true
FEATURE [Sketcher::SketchObject] Sketch015  label="guida rail"
  ArcFitTolerance = 1e-06
  AttachmentSupport = -> [XZ_Plane]
  ExternalGeometry = -> [Sketch]
  FullyConstrained = true
  MakeInternals = false
  MapMode = 5
  Placement = pos=(0,0,0) rot=(1,0,0;1.5708rad)
  sketch-geometry (4):
    g0: LineSegment StartX=-100.8 StartY=43.2 StartZ=0 EndX=-44.6 EndY=43.2 EndZ=0
    g1: LineSegment StartX=-44.6 StartY=43.2 StartZ=0 EndX=-44.6 EndY=41.2 EndZ=0
    g2: LineSegment StartX=-44.6 StartY=41.2 StartZ=0 EndX=-100.8 EndY=41.2 EndZ=0
    g3: LineSegment StartX=-100.8 StartY=41.2 StartZ=0 EndX=-100.8 EndY=43.2 EndZ=0
  constraints (9):
    c: Horizontal(g0)
    c: Coincident(g1,g0)
    c: Coincident(g2,g1)
    c: Coincident(g3,g2)
    c: Coincident(g3,g0)
    c: Vertical(g3)
    c: Coincident(g2,g-3)
    c: Coincident(g1,g-3)
    c: Coincident(g0,g-4)
FEATURE [Part::Extrusion] Extrude011  label="Extrude guida rail"
  Base = -> Sketch015
  Dir = (0,-1,2e-16)
  DirMode = 2
  FaceMakerClass = Part::FaceMakerBullseye
  FaceMakerMode = 3
  LengthFwd = 9
  LengthRev = 0
  Solid = true
  Symmetric = true
FEATURE [Sketcher::SketchObject] Sketch016  label="guide per coperture laterali"
  ArcFitTolerance = 1e-06
  AttachmentSupport = -> [XZ_Plane]
  ExternalGeometry = -> [Sketch]
  FullyConstrained = true
  MakeInternals = false
  MapMode = 5
  Placement = pos=(0,0,0) rot=(1,0,0;1.5708rad)
  sketch-geometry (14):
    g0: Circle CenterX=-5.6 CenterY=7.6 CenterZ=0 NormalX=0 NormalY=0 NormalZ=1 AngleXU=0 Radius=1.6
    g1: Circle CenterX=-5.6 CenterY=7.6 CenterZ=0 NormalX=0 NormalY=0 NormalZ=1 AngleXU=0 Radius=4
    g2: Circle CenterX=-5.6 CenterY=34.8 CenterZ=0 NormalX=0 NormalY=0 NormalZ=1 AngleXU=0 Radius=1.6
    g3: Circle CenterX=-5.6 CenterY=34.8 CenterZ=0 NormalX=0 NormalY=0 NormalZ=1 AngleXU=0 Radius=4
    g4: Circle CenterX=-184.08 CenterY=34.8 CenterZ=0 NormalX=0 NormalY=0 NormalZ=1 AngleXU=0 Radius=1.6
    g5: Circle CenterX=-184.08 CenterY=34.8 CenterZ=0 NormalX=0 NormalY=0 NormalZ=1 AngleXU=0 Radius=4
    g6: Circle CenterX=-179.305 CenterY=-76.8316 CenterZ=0 NormalX=0 NormalY=0 NormalZ=1 AngleXU=0 Radius=1.6
    g7: Circle CenterX=-179.305 CenterY=-76.8316 CenterZ=0 NormalX=0 NormalY=0 NormalZ=1 AngleXU=0 Radius=4
    g8: Circle CenterX=-213.443 CenterY=-76.8316 CenterZ=0 NormalX=0 NormalY=0 NormalZ=1 AngleXU=0 Radius=1.6
    g9: Circle CenterX=-213.443 CenterY=-76.8316 CenterZ=0 NormalX=0 NormalY=0 NormalZ=1 AngleXU=0 Radius=4
    g10: Circle CenterX=-78.51 CenterY=7.6 CenterZ=0 NormalX=0 NormalY=0 NormalZ=1 AngleXU=0 Radius=1.6
    g11: Circle CenterX=-78.51 CenterY=7.6 CenterZ=0 NormalX=0 NormalY=0 NormalZ=1 AngleXU=0 Radius=4
    g12: Circle CenterX=-78.51 CenterY=34.8 CenterZ=0 NormalX=0 NormalY=0 NormalZ=1 AngleXU=0 Radius=1.6
    g13: Circle CenterX=-78.51 CenterY=34.8 CenterZ=0 NormalX=0 NormalY=0 NormalZ=1 AngleXU=0 Radius=4
  constraints (35):
    c: Diameter(g0) = 3.2
    c: Diameter(g1) = 8
    c: Coincident(g0,g1)
    c: Diameter(g2) = 3.2
    c: Diameter(g3) = 8
    c: Coincident(g3,g2)
    c: Tangent(g2,g-7)
    c: Diameter(g4) = 3.2
    c: Diameter(g5) = 8
    c: Coincident(g5,g4)
    c: Tangent(g4,g-7)
    c: Tangent(g4,g-8)
    c: Diameter(g6) = 3.2
    c: Diameter(g7) = 8
    c: Coincident(g7,g6)
    c: Tangent(g6,g-9)
    c: Tangent(g6,g-10)
    c: Diameter(g8) = 3.2
    c: Diameter(g9) = 8
    c: Coincident(g9,g8)
    c: Tangent(g8,g-10)
    c: Tangent(g8,g-11)
    c: Diameter(g10) = 3.2
    c: Diameter(g11) = 8
    c: Diameter(g12) = 3.2
    c: Diameter(g13) = 8
    c: Coincident(g12,g13)
    c: Coincident(g10,g11)
    c: Tangent(g12,g-7)
    c: DistanceX(g12,g10) = 0
    c: Tangent(g2,g-6)
    c: Tangent(g0,g-6)
    c: Tangent(g0,g-3)
    c: Tangent(g10,g-3)
    c: Tangent(g10,g-4)
FEATURE [Part::Extrusion] Extrude012  label="extrude guide per coperture laterali"
  Base = -> Sketch016
  Dir = (0,-1,2e-16)
  DirMode = 2
  FaceMakerClass = Part::FaceMakerBullseye
  FaceMakerMode = 3
  LengthFwd = 25.2
  LengthRev = 0
  Solid = true
  Symmetric = true
FEATURE [Sketcher::SketchObject] Sketch017  label="supporto CAM"
  ArcFitTolerance = 1e-06
  AttachmentSupport = -> [XZ_Plane]
  ExternalGeometry = -> [Sketch]
  FullyConstrained = true
  MakeInternals = false
  MapMode = 5
  Placement = pos=(0,0,0) rot=(1,0,0;1.5708rad)
  sketch-geometry (6):
    g0: LineSegment StartX=-2.4 StartY=48 StartZ=0 EndX=-2.4 EndY=41.2 EndZ=0
    g1: LineSegment StartX=-2.4 StartY=48 StartZ=0 EndX=-34 EndY=48 EndZ=0
    g2: LineSegment StartX=-34 StartY=48 StartZ=0 EndX=-34 EndY=46.72 EndZ=0
    g3: LineSegment StartX=-34 StartY=46.72 StartZ=0 EndX=-36 EndY=46.72 EndZ=0
    g4: LineSegment StartX=-36 StartY=46.72 StartZ=0 EndX=-36 EndY=41.2 EndZ=0
    g5: LineSegment StartX=-36 StartY=41.2 StartZ=0 EndX=-2.4 EndY=41.2 EndZ=0
  constraints (15):
    c: Coincident(g1,g0)
    c: Horizontal(g1)
    c: Coincident(g2,g1)
    c: Vertical(g2)
    c: Coincident(g3,g2)
    c: Horizontal(g3)
    c: Coincident(g4,g3)
    c: Coincident(g5,g4)
    c: DistanceX(g1,g0) = 31.6
    c: Coincident(g5,g0)
    c: Vertical(g4)
    c: DistanceY(g2,g1) = 1.28
    c: Coincident(g0,g-3)
    c: Coincident(g0,g-3)
    c: Coincident(g4,g-4)
FEATURE [Part::Extrusion] Extrude013  label="Extrude supporto CAM"
  Base = -> Sketch017
  Dir = (0,-1,2e-16)
  DirMode = 2
  FaceMakerClass = Part::FaceMakerBullseye
  FaceMakerMode = 3
  LengthFwd = 17.8
  LengthRev = 0
  Solid = true
  Symmetric = true
FEATURE [Sketcher::SketchObject] Sketch018  label="Scavo CAM"
  ArcFitTolerance = 1e-06
  AttachmentSupport = -> [YZ_Plane]
  ExternalGeometry = -> [Sketch]
  FullyConstrained = true
  MakeInternals = false
  MapMode = 5
  Placement = pos=(0,0,0) rot=(0.57735,0.57735,0.57735;2.0944rad)
  sketch-geometry (4):
    g0: LineSegment StartX=-7.73 StartY=48 StartZ=0 EndX=7.73 EndY=48 EndZ=0
    g1: LineSegment [constr] StartX=1.07e-14 StartY=48 StartZ=0 EndX=0 EndY=43.5155 EndZ=0
    g2: ArcOfCircle CenterX=9e-15 CenterY=52.42 CenterZ=0 NormalX=0 NormalY=0 NormalZ=1 AngleXU=0 Radius=8.90445 StartAngle=3.66102 EndAngle=5.76376
    g3: Circle [constr] CenterX=9e-15 CenterY=52.42 CenterZ=0 NormalX=0 NormalY=0 NormalZ=1 AngleXU=0 Radius=8.9
  constraints (13):
    c: Horizontal(g0)
    c: DistanceY(g-3,g0) = 0
    c: DistanceX(g0,g0) = 15.46
    c: DistanceX(g0,g-3) = 7.73
    c: DistanceX(g-3) = 0
    c: Coincident(g1,g-3)
    c: PointOnObject(g1,g-2)
    c: Coincident(g2,g0)
    c: Coincident(g2,g0)
    c: PointOnObject(g1,g2)
    c: Diameter(g3) = 17.8
    c: DistanceY(g1,g3) = 4.42
    c: Coincident(g2,g3)
FEATURE [Part::Extrusion] Extrude014  label="Extrude Scavo CAM"
  Base = -> Sketch018
  Dir = (1,0,0)
  DirMode = 2
  FaceMakerClass = Part::FaceMakerBullseye
  FaceMakerMode = 3
  LengthFwd = -34
  LengthRev = 0
  Solid = true
  Symmetric = false
FEATURE [Sketcher::SketchObject] Sketch019  label="scavo rumble"
  ArcFitTolerance = 1e-06
  AttachmentSupport = -> [XZ_Plane]
  ExternalGeometry = -> [Sketch]
  FullyConstrained = true
  MakeInternals = false
  MapMode = 5
  Placement = pos=(0,0,0) rot=(1,0,0;1.5708rad)
  sketch-geometry (6):
    g0: LineSegment StartX=-164.266 StartY=-23.4275 StartZ=0 EndX=-159.13 EndY=-25.0962 EndZ=0
    g1: LineSegment StartX=-159.13 StartY=-25.0962 StartZ=0 EndX=-166.238 EndY=-46.9705 EndZ=0
    g2: LineSegment StartX=-166.238 StartY=-46.9705 StartZ=0 EndX=-171.373 EndY=-45.3018 EndZ=0
    g3: LineSegment StartX=-171.373 StartY=-45.3018 StartZ=0 EndX=-164.266 EndY=-23.4275 EndZ=0
    g4: LineSegment [constr] StartX=-145.51 StartY=22 StartZ=0 EndX=-160.652 EndY=-24.6018 EndZ=0
    g5: LineSegment [constr] StartX=-159.13 StartY=-25.0962 StartZ=0 EndX=-160.652 EndY=-24.6018 EndZ=0
  constraints (17):
    c: Coincident(g1,g0)
    c: Coincident(g2,g1)
    c: Coincident(g3,g2)
    c: Coincident(g3,g0)
    c: Parallel(g3,g-3)
    c: Parallel(g3,g1)
    c: Perpendicular(g3,g0)
    c: Perpendicular(g2,g3)
    c: Distance(g2,g0) = 23
    c: Parallel(g4,g-3)
    c: Distance(g4) = 49
    c: Coincident(g4,g-3)
    c: Parallel(g5,g0)
    c: Distance(g5) = 1.6
    c: Coincident(g5,g0)
    c: Distance(g5,g0) = 3.8
    c: Coincident(g5,g4)
FEATURE [Part::Extrusion] Extrude015  label="scavo rumble001"
  Base = -> Sketch019
  Dir = (0,-1,2e-16)
  DirMode = 2
  FaceMakerClass = Part::FaceMakerBullseye
  FaceMakerMode = 3
  LengthFwd = 21
  LengthRev = 0
  Solid = true
  Symmetric = true
FEATURE [Sketcher::SketchObject] Sketch020  label="fermo rumble"
  ArcFitTolerance = 1e-06
  AttachmentSupport = -> [XZ_Plane]
  ExternalGeometry = -> [Sketch019,Sketch]
  FullyConstrained = true
  MakeInternals = false
  MapMode = 5
  Placement = pos=(0,0,0) rot=(1,0,0;1.5708rad)
  sketch-geometry (16):
    g0: LineSegment [constr] StartX=-166.4 StartY=-42.2914 StartZ=0 EndX=-167.759 EndY=-46.4761 EndZ=0
    g1: LineSegment [constr] StartX=-167.759 StartY=-46.4761 StartZ=0 EndX=-166.238 EndY=-46.9705 EndZ=0
    g2: LineSegment StartX=-167.812 StartY=-39.5193 StartZ=0 EndX=-165.72 EndY=-40.1991 EndZ=0
    g3: LineSegment StartX=-165.72 StartY=-40.1991 StartZ=0 EndX=-166.4 EndY=-42.2914 EndZ=0
    g4: LineSegment StartX=-166.4 StartY=-42.2914 StartZ=0 EndX=-168.492 EndY=-41.6116 EndZ=0
    g5: LineSegment StartX=-168.492 StartY=-41.6116 StartZ=0 EndX=-167.812 EndY=-39.5193 EndZ=0
    g6: LineSegment StartX=-167.318 StartY=-37.9976 StartZ=0 EndX=-163.894 EndY=-39.11 EndZ=0
    g7: LineSegment StartX=-163.894 StartY=-39.11 StartZ=0 EndX=-165.501 EndY=-44.0555 EndZ=0
    g8: LineSegment StartX=-165.501 StartY=-44.0555 StartZ=0 EndX=-168.924 EndY=-42.9431 EndZ=0
    g9: LineSegment StartX=-169.952 StartY=-40.9269 StartZ=0 EndX=-169.334 EndY=-39.0248 EndZ=0
    g10: LineSegment [constr] StartX=-169.334 StartY=-39.0248 StartZ=0 EndX=-168.839 EndY=-37.5031 EndZ=0
    g11: LineSegment [constr] StartX=-168.839 StartY=-37.5031 StartZ=0 EndX=-167.318 EndY=-37.9976 EndZ=0
    g12: ArcOfCircle CenterX=-168.43 CenterY=-41.4214 CenterZ=0 NormalX=0 NormalY=0 NormalZ=1 AngleXU=0 Radius=1.6 StartAngle=2.82743 EndAngle=4.39823
    g13: GeomPoint [constr] X=-170.446 Y=-42.4486 Z=0
    g14: ArcOfCircle CenterX=-167.812 CenterY=-39.5193 CenterZ=0 NormalX=0 NormalY=0 NormalZ=1 AngleXU=0 Radius=1.6 StartAngle=1.25664 EndAngle=2.82743
    g15: GeomPoint [constr] X=-168.839 Y=-37.5031 Z=0
  constraints (42):
    c: Parallel(g0,g-4)
    c: Distance(g0) = 4.4
    c: Coincident(g1,g0)
    c: Perpendicular(g0,g1)
    c: Distance(g1) = 1.6
    c: Coincident(g1,g-5)
    c: Coincident(g3,g2)
    c: Coincident(g4,g3)
    c: Coincident(g5,g4)
    c: Coincident(g5,g2)
    c: Parallel(g3,g-4)
    c: Parallel(g3,g5)
    c: Perpendicular(g2,g3)
    c: Parallel(g4,g2)
    c: Distance(g2) = 2.2
    c: Distance(g3) = 2.2
    c: Coincident(g7,g6)
    c: Coincident(g8,g7)
    c: Parallel(g7,g-4)
    c: Parallel(g7,g9)
    c: Perpendicular(g6,g7)
    c: Parallel(g6,g8)
    c: Distance(g6,g15) = 5.2
    c: Distance(g7) = 5.2
    c: Coincident(g11,g10)
    c: Parallel(g10,g9)
    c: Parallel(g11,g6)
    c: Distance(g10) = 1.6
    c: Distance(g11) = 1.6
    c: Coincident(g10,g15)
    c: Distance(g11,g2) = 1.6
    c: Distance(g2,g10) = 1.6
    c: PointOnObject(g13,g8)
    c: PointOnObject(g13,g9)
    c: Tangent(g8,g12) = 1.5708
    c: Tangent(g9,g12) = 1.5708
    c: PointOnObject(g15,g9)
    c: Tangent(g6,g14) = 1.5708
    c: Tangent(g9,g14) = 1.5708
    c: Equal(g12,g14)
    c: Coincident(g6,g11)
    c: Coincident(g3,g0)
FEATURE [Part::Extrusion] Extrude016  label="Extrude fermo rumble"
  Base = -> Sketch020
  Dir = (0,-1,2e-16)
  DirMode = 2
  FaceMakerClass = Part::FaceMakerBullseye
  FaceMakerMode = 3
  LengthFwd = 25.2
  LengthRev = 0
  Solid = true
  Symmetric = true
FEATURE [Sketcher::SketchObject] Sketch021  label="perno fermo rumble001"
  ArcFitTolerance = 1e-06
  AttachmentSupport = -> [XZ_Plane001]
  FullyConstrained = true
  MakeInternals = false
  MapMode = 5
  Placement = pos=(0,0,0) rot=(1,0,0;1.5708rad)
  sketch-geometry (16):
    g0: LineSegment StartX=0 StartY=0.45 StartZ=0 EndX=0 EndY=1.55 EndZ=0
    g1: LineSegment StartX=0.45 StartY=2 StartZ=0 EndX=1.55 EndY=2 EndZ=0
    g2: LineSegment StartX=2 StartY=1.55 StartZ=0 EndX=2 EndY=0.45 EndZ=0
    g3: LineSegment StartX=1.55 StartY=0 StartZ=0 EndX=0.45 EndY=0 EndZ=0
    g4: ArcOfCircle [constr] CenterX=0.45 CenterY=1.55 CenterZ=0 NormalX=0 NormalY=0 NormalZ=1 AngleXU=0 Radius=0.45 StartAngle=1.5708 EndAngle=3.14159
    g5: GeomPoint [constr] X=0 Y=2 Z=0
    g6: LineSegment StartX=0.45 StartY=2 StartZ=0 EndX=0 EndY=1.55 EndZ=0
    g7: ArcOfCircle [constr] CenterX=1.55 CenterY=1.55 CenterZ=0 NormalX=0 NormalY=0 NormalZ=1 AngleXU=0 Radius=0.45 StartAngle=0 EndAngle=1.5708
    g8: GeomPoint [constr] X=2 Y=2 Z=0
    g9: LineSegment StartX=2 StartY=1.55 StartZ=0 EndX=1.55 EndY=2 EndZ=0
    g10: ArcOfCircle [constr] CenterX=1.55 CenterY=0.45 CenterZ=0 NormalX=0 NormalY=0 NormalZ=1 AngleXU=0 Radius=0.45 StartAngle=4.71239 EndAngle=6.28319
    g11: GeomPoint [constr] X=2 Y=0 Z=0
    g12: LineSegment StartX=1.55 StartY=0 StartZ=0 EndX=2 EndY=0.45 EndZ=0
    g13: ArcOfCircle [constr] CenterX=0.45 CenterY=0.45 CenterZ=0 NormalX=0 NormalY=0 NormalZ=1 AngleXU=0 Radius=0.45 StartAngle=3.14159 EndAngle=4.71239
    g14: GeomPoint [constr] X=0 Y=0 Z=0
    g15: LineSegment StartX=0 StartY=0.45 StartZ=0 EndX=0.45 EndY=0 EndZ=0
  constraints (35):
    c: Coincident(g14,g-1)
    c: PointOnObject(g5,g-2)
    c: Horizontal(g1)
    c: Vertical(g2)
    c: Horizontal(g3)
    c: DistanceX(g5,g8) = 2
    c: DistanceY(g11,g8) = 2
    c: PointOnObject(g5,g0)
    c: PointOnObject(g5,g1)
    c: Tangent(g0,g4) = 1.5708
    c: Tangent(g1,g4) = 1.5708
    c: Coincident(g6,g0)
    c: Coincident(g6,g1)
    c: PointOnObject(g8,g2)
    c: PointOnObject(g8,g1)
    c: Tangent(g2,g7) = 1.5708
    c: Tangent(g1,g7) = 1.5708
    c: Coincident(g9,g2)
    c: Coincident(g9,g1)
    c: PointOnObject(g11,g2)
    c: PointOnObject(g11,g3)
    c: Tangent(g2,g10) = 1.5708
    c: Tangent(g3,g10) = 1.5708
    c: Coincident(g12,g2)
    c: Coincident(g12,g3)
    c: PointOnObject(g14,g0)
    c: PointOnObject(g14,g3)
    c: Tangent(g0,g13) = 1.5708
    c: Tangent(g3,g13) = 1.5708
    c: Coincident(g15,g0)
    c: Coincident(g15,g3)
    c: Equal(g6,g9)
    c: Equal(g9,g12)
    c: Equal(g12,g15)
    c: DistanceX(g14,g3) = 0.45
FEATURE [Sketcher::SketchObject] Sketch022  label="fori per M3x5(OD)x6(L)"
  ArcFitTolerance = 1e-06
  AttachmentSupport = -> [XZ_Plane]
  ExternalGeometry = -> [Sketch016]
  FullyConstrained = true
  MakeInternals = false
  MapMode = 5
  Placement = pos=(0,0,0) rot=(1,0,0;1.5708rad)
  sketch-geometry (7):
    g0: Circle CenterX=-5.6 CenterY=34.8 CenterZ=0 NormalX=0 NormalY=0 NormalZ=1 AngleXU=0 Radius=2.5
    g1: Circle CenterX=-5.6 CenterY=7.6 CenterZ=0 NormalX=0 NormalY=0 NormalZ=1 AngleXU=0 Radius=2.5
    g2: Circle CenterX=-78.51 CenterY=34.8 CenterZ=0 NormalX=0 NormalY=0 NormalZ=1 AngleXU=0 Radius=2.5
    g3: Circle CenterX=-78.51 CenterY=7.6 CenterZ=0 NormalX=0 NormalY=0 NormalZ=1 AngleXU=0 Radius=2.5
    g4: Circle CenterX=-184.08 CenterY=34.8 CenterZ=0 NormalX=0 NormalY=0 NormalZ=1 AngleXU=0 Radius=2.5
    g5: Circle CenterX=-179.305 CenterY=-76.8316 CenterZ=0 NormalX=0 NormalY=0 NormalZ=1 AngleXU=0 Radius=2.5
    g6: Circle CenterX=-213.443 CenterY=-76.8316 CenterZ=0 NormalX=0 NormalY=0 NormalZ=1 AngleXU=0 Radius=2.5
  constraints (14):
    c: Diameter(g0) = 5
    c: Diameter(g1) = 5
    c: Diameter(g2) = 5
    c: Diameter(g3) = 5
    c: Diameter(g4) = 5
    c: Diameter(g5) = 5
    c: Diameter(g6) = 5
    c: Coincident(g0,g-8)
    c: Coincident(g1,g-9)
    c: Coincident(g2,g-6)
    c: Coincident(g3,g-7)
    c: Coincident(g4,g-5)
    c: Coincident(g5,g-4)
    c: Coincident(g6,g-3)
FEATURE [Part::Extrusion] Extrude018  label="Extrude fori M3x5x6 - dx"
  Base = -> Sketch022
  Dir = (0,-1,2e-16)
  DirMode = 2
  FaceMakerClass = Part::FaceMakerBullseye
  FaceMakerMode = 3
  LengthFwd = 6.2
  LengthRev = 0
  Placement = pos=(0,-9.5,0) rot=(0,0,1;0rad)
  Solid = true
  Symmetric = true
FEATURE [Part::Extrusion] Extrude019  label="Extrude fori M3x5x6 - sx"
  Base = -> Sketch022
  Dir = (0,-1,2e-16)
  DirMode = 2
  FaceMakerClass = Part::FaceMakerBullseye
  FaceMakerMode = 3
  LengthFwd = 6.2
  LengthRev = 0
  Placement = pos=(0,9.5,0) rot=(0,0,1;0rad)
  Solid = true
  Symmetric = true
FEATURE [Sketcher::SketchObject] Sketch023  label="foro anteriore M3x5x6"
  ArcFitTolerance = 1e-06
  AttachmentSupport = -> [YZ_Plane]
  FullyConstrained = true
  MakeInternals = false
  MapMode = 5
  Placement = pos=(0,0,0) rot=(0.57735,0.57735,0.57735;2.0944rad)
  sketch-geometry (2):
    g0: LineSegment [constr] StartX=0 StartY=0 StartZ=0 EndX=0 EndY=38.6 EndZ=0
    g1: Circle CenterX=0 CenterY=38.6 CenterZ=0 NormalX=0 NormalY=0 NormalZ=1 AngleXU=0 Radius=2.5
  constraints (5):
    c: Coincident(g0,g-1)
    c: PointOnObject(g0,g-2)
    c: DistanceY(g0,g0) = 38.6
    c: Diameter(g1) = 5
    c: Coincident(g1,g0)
FEATURE [Part::Extrusion] Extrude020  label="Extrude foro anteriore M3x5x6"
  Base = -> Sketch023
  Dir = (1,0,0)
  DirMode = 2
  FaceMakerClass = Part::FaceMakerBullseye
  FaceMakerMode = 3
  LengthFwd = -6.2
  LengthRev = 0
  Solid = true
  Symmetric = false
FEATURE [Sketcher::SketchObject] Sketch024  label="fori per viti frontale"
  ArcFitTolerance = 1e-06
  AttachmentSupport = -> [YZ_Plane]
  FullyConstrained = true
  MakeInternals = false
  MapMode = 5
  Placement = pos=(0,0,0) rot=(0.57735,0.57735,0.57735;2.0944rad)
  sketch-geometry (9):
    g0: LineSegment [constr] StartX=-10.3 StartY=30.721 StartZ=0 EndX=10.3 EndY=30.721 EndZ=0
    g1: LineSegment [constr] StartX=10.3 StartY=30.721 StartZ=0 EndX=10.3 EndY=10.121 EndZ=0
    g2: LineSegment [constr] StartX=10.3 StartY=10.121 StartZ=0 EndX=-10.3 EndY=10.121 EndZ=0
    g3: LineSegment [constr] StartX=-10.3 StartY=10.121 StartZ=0 EndX=-10.3 EndY=30.721 EndZ=0
    g4: LineSegment [constr] StartX=0 StartY=0 StartZ=0 EndX=0 EndY=10.121 EndZ=0
    g5: Circle CenterX=-10.3 CenterY=30.721 CenterZ=0 NormalX=0 NormalY=0 NormalZ=1 AngleXU=0 Radius=2
    g6: Circle CenterX=10.3 CenterY=30.721 CenterZ=0 NormalX=0 NormalY=0 NormalZ=1 AngleXU=0 Radius=2
    g7: Circle CenterX=-10.3 CenterY=10.121 CenterZ=0 NormalX=0 NormalY=0 NormalZ=1 AngleXU=0 Radius=2
    g8: Circle CenterX=10.3 CenterY=10.121 CenterZ=0 NormalX=0 NormalY=0 NormalZ=1 AngleXU=0 Radius=2
  constraints (22):
    c: Horizontal(g0)
    c: Coincident(g1,g0)
    c: Vertical(g1)
    c: Coincident(g2,g1)
    c: Horizontal(g2)
    c: Coincident(g3,g2)
    c: Coincident(g3,g0)
    c: Vertical(g3)
    c: DistanceX(g0,g0) = 20.6
    c: DistanceY(g3,g3) = 20.6
    c: Coincident(g4,g-1)
    c: PointOnObject(g4,g-2)
    c: DistanceY(g4,g4) = 10.121
    c: Symmetric(g2,g2,g4)
    c: Diameter(g5) = 4
    c: Diameter(g6) = 4
    c: Diameter(g7) = 4
    c: Diameter(g8) = 4
    c: Coincident(g5,g0)
    c: Coincident(g6,g0)
    c: Coincident(g7,g2)
    c: Coincident(g8,g1)
FEATURE [Part::Extrusion] Extrude021  label="Extrude fori per viti frontale"
  Base = -> Sketch024
  Dir = (1,0,0)
  DirMode = 2
  FaceMakerClass = Part::FaceMakerBullseye
  FaceMakerMode = 3
  LengthFwd = -2.4
  LengthRev = 0
  Solid = true
  Symmetric = false
FEATURE [Sketcher::SketchObject] Sketch025  label="foro per filo CAM"
  ArcFitTolerance = 1e-06
  AttachmentSupport = -> [XZ_Plane]
  ExternalGeometry = -> [Sketch]
  FullyConstrained = true
  MakeInternals = false
  MapMode = 5
  Placement = pos=(0,0,0) rot=(1,0,0;1.5708rad)
  sketch-geometry (4):
    g0: LineSegment StartX=-44.6 StartY=41.2 StartZ=0 EndX=-44.6 EndY=36.4 EndZ=0
    g1: LineSegment StartX=-44.6 StartY=36.4 StartZ=0 EndX=-54.6 EndY=36.4 EndZ=0
    g2: LineSegment StartX=-54.6 StartY=36.4 StartZ=0 EndX=-50.4 EndY=41.2 EndZ=0
    g3: LineSegment StartX=-50.4 StartY=41.2 StartZ=0 EndX=-44.6 EndY=41.2 EndZ=0
  constraints (11):
    c: Vertical(g0)
    c: Coincident(g1,g0)
    c: Horizontal(g1)
    c: Coincident(g2,g1)
    c: Coincident(g3,g2)
    c: Coincident(g3,g0)
    c: Horizontal(g3)
    c: Coincident(g0,g-3)
    c: DistanceY(g0,g-4) = 0
    c: DistanceX(g3,g3) = 5.8
    c: DistanceX(g1,g1) = 10
FEATURE [Part::Extrusion] Extrude022  label="Extrude foro per filo CAM dx"
  Base = -> Sketch025
  Dir = (0,-1,2e-16)
  DirMode = 2
  FaceMakerClass = Part::FaceMakerBullseye
  FaceMakerMode = 3
  LengthFwd = 4.9
  LengthRev = 0
  Placement = pos=(0,6.95,0) rot=(0,0,1;0rad)
  Solid = true
  Symmetric = true
FEATURE [Part::Extrusion] Extrude023  label="Extrude foro per filo CAM sx"
  Base = -> Sketch025
  Dir = (0,-1,2e-16)
  DirMode = 2
  FaceMakerClass = Part::FaceMakerBullseye
  FaceMakerMode = 3
  LengthFwd = 4.9
  LengthRev = 0
  Placement = pos=(0,-6.95,0) rot=(0,0,1;0rad)
  Solid = true
  Symmetric = true
FEATURE [Sketcher::SketchObject] Sketch026  label="foro sotto anteriore M3x5x6"
  ArcFitTolerance = 1e-06
  AttachmentSupport = -> [XY_Plane]
  FullyConstrained = true
  MakeInternals = false
  MapMode = 5
  sketch-geometry (2):
    g0: LineSegment [constr] StartX=0 StartY=0 StartZ=0 EndX=-16.5 EndY=0 EndZ=0
    g1: Circle CenterX=-16.5 CenterY=0 CenterZ=0 NormalX=0 NormalY=0 NormalZ=1 AngleXU=0 Radius=2.5
  constraints (5):
    c: Distance(g0) = 16.5
    c: Coincident(g0,g-1)
    c: PointOnObject(g0,g-1)
    c: Diameter(g1) = 5
    c: Coincident(g0,g1)
FEATURE [Sketcher::SketchObject] Sketch027  label="foro sotto posteriore M3x5x6"
  ArcFitTolerance = 1e-06
  AttachmentSupport = -> [XY_Plane]
  ExternalGeometry = -> [Sketch]
  FullyConstrained = true
  MakeInternals = false
  MapMode = 5
  sketch-geometry (2):
    g0: LineSegment [constr] StartX=-82.8 StartY=2e-16 StartZ=0 EndX=-71.3 EndY=2e-16 EndZ=0
    g1: Circle CenterX=-71.3 CenterY=2e-16 CenterZ=0 NormalX=0 NormalY=0 NormalZ=1 AngleXU=0 Radius=2.5
  constraints (5):
    c: Distance(g0) = 11.5
    c: Coincident(g0,g-3)
    c: PointOnObject(g0,g-3)
    c: Diameter(g1) = 5
    c: Coincident(g1,g0)
FEATURE [Sketcher::SketchObject] Sketch029  label="fori sotto impugnatura"
  ArcFitTolerance = 1e-06
  AttachmentSupport = -> [XY_Plane]
  ExternalGeometry = -> [Sketch]
  FullyConstrained = true
  MakeInternals = false
  MapMode = 5
  sketch-geometry (15):
    g0: LineSegment [constr] StartX=-175.232 StartY=-1.83e-14 StartZ=0 EndX=-191.232 EndY=0 EndZ=0
    g1: Circle CenterX=-191.232 CenterY=0 CenterZ=0 NormalX=0 NormalY=0 NormalZ=1 AngleXU=0 Radius=3.95
    g2: LineSegment [constr] StartX=-175.232 StartY=-1.83e-14 StartZ=0 EndX=-204.275 EndY=0 EndZ=0
    g3: LineSegment StartX=-204.275 StartY=3.525 StartZ=0 EndX=-204.275 EndY=-3.525 EndZ=0
    g4: LineSegment StartX=-205.4 StartY=-4.65 StartZ=0 EndX=-206.65 EndY=-4.65 EndZ=0
    g5: LineSegment StartX=-207.775 StartY=-3.525 StartZ=0 EndX=-207.775 EndY=3.525 EndZ=0
    g6: LineSegment StartX=-206.65 StartY=4.65 StartZ=0 EndX=-205.4 EndY=4.65 EndZ=0
    g7: ArcOfCircle CenterX=-206.65 CenterY=3.525 CenterZ=0 NormalX=0 NormalY=0 NormalZ=1 AngleXU=0 Radius=1.125 StartAngle=1.5708 EndAngle=3.14159
    g8: GeomPoint [constr] X=-207.775 Y=4.65 Z=0
    g9: ArcOfCircle CenterX=-205.4 CenterY=3.525 CenterZ=0 NormalX=0 NormalY=0 NormalZ=1 AngleXU=0 Radius=1.125 StartAngle=0 EndAngle=1.5708
    g10: GeomPoint [constr] X=-204.275 Y=4.65 Z=0
    g11: ArcOfCircle CenterX=-205.4 CenterY=-3.525 CenterZ=0 NormalX=0 NormalY=0 NormalZ=1 AngleXU=0 Radius=1.125 StartAngle=4.71239 EndAngle=6.28319
    g12: GeomPoint [constr] X=-204.275 Y=-4.65 Z=0
    g13: ArcOfCircle CenterX=-206.65 CenterY=-3.525 CenterZ=0 NormalX=0 NormalY=0 NormalZ=1 AngleXU=0 Radius=1.125 StartAngle=3.14159 EndAngle=4.71239
    g14: GeomPoint [constr] X=-207.775 Y=-4.65 Z=0
  constraints (35):
    c: Distance(g0) = 16
    c: Coincident(g0,g-3)
    c: PointOnObject(g0,g-1)
    c: Diameter(g1) = 7.9
    c: Coincident(g1,g0)
    c: Coincident(g2,g0)
    c: PointOnObject(g2,g-1)
    c: Vertical(g3)
    c: Horizontal(g4)
    c: Vertical(g5)
    c: Horizontal(g6)
    c: DistanceY(g12,g10) = 9.3
    c: DistanceX(g8,g10) = 3.5
    c: Symmetric(g10,g12,g2)
    c: PointOnObject(g8,g5)
    c: PointOnObject(g8,g6)
    c: Tangent(g5,g7) = 1.5708
    c: Tangent(g6,g7) = 1.5708
    c: PointOnObject(g10,g3)
    c: PointOnObject(g10,g6)
    c: Tangent(g3,g9) = 1.5708
    c: Tangent(g6,g9) = 1.5708
    c: PointOnObject(g12,g3)
    c: PointOnObject(g12,g4)
    c: Tangent(g3,g11) = 1.5708
    c: Tangent(g4,g11) = 1.5708
    c: PointOnObject(g14,g4)
    c: PointOnObject(g14,g5)
    c: Tangent(g4,g13) = 1.5708
    c: Tangent(g5,g13) = 1.5708
    c: Equal(g7,g9)
    c: Equal(g9,g11)
    c: Equal(g11,g13)
    c: DistanceX(g6,g6) = 1.25
    c: DistanceX(g-5,g5) = 6.8
FEATURE [Sketcher::SketchObject] Sketch030  label="fori superiori per solenoide e oled"
  ArcFitTolerance = 1e-06
  AttachmentSupport = -> [XY_Plane]
  ExternalGeometry = -> [Sketch]
  FullyConstrained = true
  MakeInternals = false
  MapMode = 5
  sketch-geometry (33):
    g0: LineSegment [constr] StartX=-181.6 StartY=1.12e-14 StartZ=0 EndX=-169.91 EndY=0 EndZ=0
    g1: LineSegment [constr] StartX=-169.91 StartY=0 StartZ=0 EndX=-169.91 EndY=-2.6 EndZ=0
    g2: LineSegment [constr] StartX=-169.91 StartY=0 StartZ=0 EndX=-169.91 EndY=2.6 EndZ=0
    g3: LineSegment StartX=-169.91 StartY=4.975 StartZ=0 EndX=-169.91 EndY=8.225 EndZ=0
    g4: LineSegment StartX=-167.535 StartY=10.6 StartZ=0 EndX=-167.285 EndY=10.6 EndZ=0
    g5: LineSegment StartX=-164.91 StartY=8.225 StartZ=0 EndX=-164.91 EndY=4.975 EndZ=0
    g6: LineSegment StartX=-167.285 StartY=2.6 StartZ=0 EndX=-167.535 EndY=2.6 EndZ=0
    g7: LineSegment StartX=-169.91 StartY=-4.975 StartZ=0 EndX=-169.91 EndY=-8.225 EndZ=0
    g8: LineSegment StartX=-167.535 StartY=-10.6 StartZ=0 EndX=-167.285 EndY=-10.6 EndZ=0
    g9: LineSegment StartX=-164.91 StartY=-8.225 StartZ=0 EndX=-164.91 EndY=-4.975 EndZ=0
    g10: LineSegment StartX=-167.285 StartY=-2.6 StartZ=0 EndX=-167.535 EndY=-2.6 EndZ=0
    g11: ArcOfCircle CenterX=-167.535 CenterY=8.225 CenterZ=0 NormalX=0 NormalY=0 NormalZ=1 AngleXU=0 Radius=2.375 StartAngle=1.5708 EndAngle=3.14159
    g12: GeomPoint [constr] X=-169.91 Y=10.6 Z=0
    g13: ArcOfCircle CenterX=-167.285 CenterY=8.225 CenterZ=0 NormalX=0 NormalY=0 NormalZ=1 AngleXU=0 Radius=2.375 StartAngle=0 EndAngle=1.5708
    g14: GeomPoint [constr] X=-164.91 Y=10.6 Z=0
    g15: ArcOfCircle CenterX=-167.285 CenterY=4.975 CenterZ=0 NormalX=0 NormalY=0 NormalZ=1 AngleXU=0 Radius=2.375 StartAngle=4.71239 EndAngle=6.28319
    g16: GeomPoint [constr] X=-164.91 Y=2.6 Z=0
    g17: ArcOfCircle CenterX=-167.535 CenterY=4.975 CenterZ=0 NormalX=0 NormalY=0 NormalZ=1 AngleXU=0 Radius=2.375 StartAngle=3.14159 EndAngle=4.71239
    g18: GeomPoint [constr] X=-169.91 Y=2.6 Z=0
    g19: ArcOfCircle CenterX=-167.535 CenterY=-4.975 CenterZ=0 NormalX=0 NormalY=0 NormalZ=1 AngleXU=0 Radius=2.375 StartAngle=1.5708 EndAngle=3.14159
    g20: GeomPoint [constr] X=-169.91 Y=-2.6 Z=0
    g21: ArcOfCircle CenterX=-167.285 CenterY=-4.975 CenterZ=0 NormalX=0 NormalY=0 NormalZ=1 AngleXU=0 Radius=2.375 StartAngle=0 EndAngle=1.5708
    g22: GeomPoint [constr] X=-164.91 Y=-2.6 Z=0
    g23: ArcOfCircle CenterX=-167.285 CenterY=-8.225 CenterZ=0 NormalX=0 NormalY=0 NormalZ=1 AngleXU=0 Radius=2.375 StartAngle=4.71239 EndAngle=6.28319
    g24: GeomPoint [constr] X=-164.91 Y=-10.6 Z=0
    g25: ArcOfCircle CenterX=-167.535 CenterY=-8.225 CenterZ=0 NormalX=0 NormalY=0 NormalZ=1 AngleXU=0 Radius=2.375 StartAngle=3.14159 EndAngle=4.71239
    g26: GeomPoint [constr] X=-169.91 Y=-10.6 Z=0
    g27: LineSegment [constr] StartX=-181.6 StartY=1.12e-14 StartZ=0 EndX=-152.209 EndY=0 EndZ=0
    g28: LineSegment [constr] StartX=-181.6 StartY=1.12e-14 StartZ=0 EndX=-130.41 EndY=0 EndZ=0
    g29: LineSegment [constr] StartX=-152.209 StartY=0 StartZ=0 EndX=-152.209 EndY=6.95 EndZ=0
    g30: LineSegment [constr] StartX=-130.41 StartY=0 StartZ=0 EndX=-130.41 EndY=-6.95 EndZ=0
    g31: Circle CenterX=-152.209 CenterY=6.95 CenterZ=0 NormalX=0 NormalY=0 NormalZ=1 AngleXU=0 Radius=2.1
    g32: Circle CenterX=-130.41 CenterY=-6.95 CenterZ=0 NormalX=0 NormalY=0 NormalZ=1 AngleXU=0 Radius=2.1
  constraints (79):
    c: Distance(g0) = 11.69
    c: PointOnObject(g0,g-1)
    c: Coincident(g-4,g0)
    c: Distance(g1) = 2.6
    c: Coincident(g1,g0)
    c: Vertical(g1)
    c: Distance(g2) = 2.6
    c: Coincident(g2,g0)
    c: Vertical(g2)
    c: Distance(g18,g12) = 8
    c: Coincident(g18,g2)
    c: Vertical(g3)
    c: Distance(g14,g12) = 5
    c: Horizontal(g4)
    c: Distance(g16,g14) = 8
    c: Vertical(g5)
    c: Distance(g26,g20) = 8
    c: Coincident(g20,g1)
    c: Vertical(g7)
    c: Distance(g26,g24) = 5
    c: Horizontal(g8)
    c: Distance(g24,g22) = 8
    c: Vertical(g9)
    c: PointOnObject(g12,g3)
    c: PointOnObject(g12,g4)
    c: Tangent(g3,g11) = 1.5708
    c: Tangent(g4,g11) = 1.5708
    c: PointOnObject(g14,g5)
    c: PointOnObject(g14,g4)
    c: Tangent(g5,g13) = 1.5708
    c: Tangent(g4,g13) = 1.5708
    c: PointOnObject(g16,g5)
    c: PointOnObject(g16,g6)
    c: Tangent(g5,g15) = 1.5708
    c: Tangent(g6,g15) = 1.5708
    c: PointOnObject(g18,g3)
    c: PointOnObject(g18,g6)
    c: Tangent(g3,g17) = 1.5708
    c: Tangent(g6,g17) = 1.5708
    c: Equal(g11,g13)
    c: Equal(g13,g15)
    c: Equal(g15,g17)
    c: DistanceX(g4,g4) = 0.25
    c: PointOnObject(g20,g7)
    c: PointOnObject(g20,g10)
    c: Tangent(g7,g19) = -1.5708
    c: Tangent(g10,g19) = -1.5708
    c: PointOnObject(g22,g9)
    c: PointOnObject(g22,g10)
    c: Tangent(g9,g21) = -1.5708
    c: Tangent(g10,g21) = -1.5708
    c: PointOnObject(g24,g9)
    c: PointOnObject(g24,g8)
    c: Tangent(g9,g23) = -1.5708
    c: Tangent(g8,g23) = -1.5708
    c: PointOnObject(g26,g8)
    c: PointOnObject(g26,g7)
    c: Tangent(g8,g25) = -1.5708
    c: Tangent(g7,g25) = -1.5708
    c: Equal(g19,g21)
    c: Equal(g21,g23)
    c: Equal(g23,g25)
    c: DistanceX(g10,g10) = 0.25
    c: Distance(g27) = 29.391
    c: Coincident(g27,g0)
    c: PointOnObject(g27,g-1)
    c: Distance(g28) = 51.19
    c: Coincident(g28,g0)
    c: PointOnObject(g28,g-1)
    c: Distance(g29) = 6.95
    c: Coincident(g29,g27)
    c: Vertical(g29)
    c: Distance(g30) = 6.95
    c: Coincident(g30,g28)
    c: Vertical(g30)
    c: Diameter(g31) = 4.2
    c: Diameter(g32) = 4.2
    c: Coincident(g32,g30)
    c: Coincident(g31,g29)
FEATURE [Sketcher::SketchObject] Sketch031  label="fori inferiori switch pompa"
  ArcFitTolerance = 1e-06
  AttachmentSupport = -> [XY_Plane]
  ExternalGeometry = -> [Sketch]
  FullyConstrained = true
  MakeInternals = false
  MapMode = 5
  sketch-geometry (4):
    g0: LineSegment [constr] StartX=-57.2 StartY=1.9e-15 StartZ=0 EndX=-62.45 EndY=1.9e-15 EndZ=0
    g1: LineSegment [constr] StartX=-62.45 StartY=3.25 StartZ=0 EndX=-62.45 EndY=-3.25 EndZ=0
    g2: Circle CenterX=-62.45 CenterY=3.25 CenterZ=0 NormalX=0 NormalY=0 NormalZ=1 AngleXU=0 Radius=1.6
    g3: Circle CenterX=-62.45 CenterY=-3.25 CenterZ=0 NormalX=0 NormalY=0 NormalZ=1 AngleXU=0 Radius=1.6
  constraints (10):
    c: Distance(g0) = 5.25
    c: Coincident(g0,g-3)
    c: PointOnObject(g0,g-3)
    c: Vertical(g1)
    c: DistanceY(g1,g1) = 6.5
    c: Symmetric(g1,g1,g0)
    c: Diameter(g2) = 3.2
    c: Diameter(g3) = 3.2
    c: Coincident(g2,g1)
    c: Coincident(g3,g1)
FEATURE [Sketcher::SketchObject] Sketch032  label="spazio per PILA 18650"
  ArcFitTolerance = 1e-06
  AttachmentSupport = -> [XY_Plane]
  ExternalGeometry = -> [Sketch]
  FullyConstrained = true
  MakeInternals = false
  MapMode = 5
  sketch-geometry (2):
    g0: LineSegment [constr] StartX=-178.142 StartY=-1.74e-14 StartZ=0 EndX=-191.142 EndY=-1.83e-14 EndZ=0
    g1: Circle CenterX=-191.142 CenterY=-1.83e-14 CenterZ=0 NormalX=0 NormalY=0 NormalZ=1 AngleXU=0 Radius=10.5
  constraints (5):
    c: Distance(g0) = 13
    c: Coincident(g0,g-3)
    c: PointOnObject(g0,g-4)
    c: Diameter(g1) = 21
    c: Coincident(g1,g0)
FEATURE [Part::Extrusion] Extrude030  label="Extrude spazio per PILA 18650"
  Base = -> Sketch032
  Dir = (0,0,1)
  DirLink = -> Sketch [Edge45]
  DirMode = 2
  FaceMakerClass = Part::FaceMakerBullseye
  FaceMakerMode = 3
  LengthFwd = 76
  LengthRev = 0
  Placement = pos=(6,0,-72) rot=(0,0,1;0rad)
  Solid = true
  Symmetric = false
FEATURE [Sketcher::SketchObject] Sketch033  label="fermo per scheda micro"
  ArcFitTolerance = 1e-06
  AttachmentSupport = -> [XZ_Plane]
  ExternalGeometry = -> [Sketch]
  FullyConstrained = true
  MakeInternals = false
  MapMode = 5
  Placement = pos=(0,0,0) rot=(1,0,0;1.5708rad)
  sketch-geometry (12):
    g0: LineSegment StartX=-11.6 StartY=6 StartZ=0 EndX=-4 EndY=6 EndZ=0
    g1: LineSegment StartX=-4 StartY=6 StartZ=0 EndX=-4 EndY=36.4 EndZ=0
    g2: LineSegment StartX=-4 StartY=36.4 StartZ=0 EndX=-11.6 EndY=36.4 EndZ=0
    g3: LineSegment StartX=-11.6 StartY=36.4 StartZ=0 EndX=-11.6 EndY=6 EndZ=0
    g4: LineSegment StartX=-80.11 StartY=11.6 StartZ=0 EndX=-70.51 EndY=11.6 EndZ=0
    g5: LineSegment StartX=-70.51 StartY=11.6 StartZ=0 EndX=-70.51 EndY=6 EndZ=0
    g6: LineSegment StartX=-70.51 StartY=6 StartZ=0 EndX=-80.11 EndY=6 EndZ=0
    g7: LineSegment StartX=-80.11 StartY=6 StartZ=0 EndX=-80.11 EndY=11.6 EndZ=0
    g8: LineSegment StartX=-78.51 StartY=36.4 StartZ=0 EndX=-70.51 EndY=36.4 EndZ=0
    g9: LineSegment StartX=-70.51 StartY=36.4 StartZ=0 EndX=-70.51 EndY=30.8 EndZ=0
    g10: LineSegment StartX=-70.51 StartY=30.8 StartZ=0 EndX=-78.51 EndY=30.8 EndZ=0
    g11: LineSegment StartX=-78.51 StartY=30.8 StartZ=0 EndX=-78.51 EndY=36.4 EndZ=0
  constraints (33):
    c: Horizontal(g0)
    c: Coincident(g1,g0)
    c: Coincident(g2,g1)
    c: Horizontal(g2)
    c: Coincident(g3,g2)
    c: Coincident(g3,g0)
    c: Vertical(g3)
    c: DistanceX(g2,g2) = 7.6
    c: Coincident(g1,g-3)
    c: Coincident(g0,g-3)
    c: Horizontal(g4)
    c: Coincident(g5,g4)
    c: Vertical(g5)
    c: Coincident(g6,g5)
    c: Horizontal(g6)
    c: Coincident(g7,g6)
    c: Coincident(g7,g4)
    c: Vertical(g7)
    c: DistanceY(g5,g5) = 5.6
    c: DistanceX(g4,g4) = 9.6
    c: Coincident(g9,g8)
    c: Vertical(g9)
    c: Coincident(g10,g9)
    c: Horizontal(g10)
    c: Coincident(g11,g10)
    c: Coincident(g11,g8)
    c: Vertical(g11)
    c: DistanceY(g9,g9) = 5.6
    c: DistanceX(g10,g10) = 8
    c: Coincident(g4,g-4)
    c: DistanceX(g4,g10) = 1.6
    c: Horizontal(g8)
    c: DistanceY(g8,g1) = 0
FEATURE [Sketcher::SketchObject] Sketch034  label="buchi guida rail"
  ArcFitTolerance = 1e-06
  AttachmentSupport = -> [XY_Plane]
  ExternalGeometry = -> [Sketch]
  FullyConstrained = true
  MakeInternals = false
  MapMode = 5
  sketch-geometry (6):
    g0: LineSegment [constr] StartX=-100.8 StartY=9.1e-15 StartZ=0 EndX=-93.3 EndY=0 EndZ=0
    g1: LineSegment [constr] StartX=-93.3 StartY=0 StartZ=0 EndX=-73.3 EndY=0 EndZ=0
    g2: LineSegment [constr] StartX=-73.3 StartY=0 StartZ=0 EndX=-53.3 EndY=0 EndZ=0
    g3: Circle CenterX=-93.3 CenterY=0 CenterZ=0 NormalX=0 NormalY=0 NormalZ=1 AngleXU=0 Radius=2.5
    g4: Circle CenterX=-73.3 CenterY=0 CenterZ=0 NormalX=0 NormalY=0 NormalZ=1 AngleXU=0 Radius=2.5
    g5: Circle CenterX=-53.3 CenterY=0 CenterZ=0 NormalX=0 NormalY=0 NormalZ=1 AngleXU=0 Radius=2.5
  constraints (15):
    c: Distance(g0) = 7.5
    c: Coincident(g0,g-3)
    c: PointOnObject(g0,g-1)
    c: Distance(g1) = 20
    c: Coincident(g1,g0)
    c: PointOnObject(g1,g-1)
    c: Distance(g2) = 20
    c: Coincident(g2,g1)
    c: PointOnObject(g2,g-1)
    c: Diameter(g3) = 5
    c: Diameter(g4) = 5
    c: Diameter(g5) = 5
    c: Coincident(g3,g0)
    c: Coincident(g4,g1)
    c: Coincident(g5,g2)
FEATURE [Part::Extrusion] Extrude032  label="Extrude buchi guida rail"
  Base = -> Sketch034
  Dir = (0,0,1)
  DirMode = 2
  FaceMakerClass = Part::FaceMakerBullseye
  FaceMakerMode = 3
  LengthFwd = -6.2
  LengthRev = 0
  Placement = pos=(0,0,43.2) rot=(0,0,1;0rad)
  Solid = true
  Symmetric = false
FEATURE [Part::Extrusion] Extrude033  label="Extrude fori superiori per solenoide e oled001"
  Base = -> Sketch030
  Dir = (0,0,1)
  DirMode = 2
  FaceMakerClass = Part::FaceMakerBullseye
  FaceMakerMode = 3
  LengthFwd = -4.8
  LengthRev = 0
  Placement = pos=(0,0,41.2) rot=(0,0,1;0rad)
  Solid = true
  Symmetric = false
FEATURE [Part::Extrusion] Extrude034  label="Extrude fori sotto impugnatura001"
  Base = -> Sketch029
  Dir = (0,0,1)
  DirMode = 2
  FaceMakerClass = Part::FaceMakerBullseye
  FaceMakerMode = 3
  LengthFwd = 5
  LengthRev = 0
  Placement = pos=(0,0,-83) rot=(0,0,1;0rad)
  Solid = true
  Symmetric = false
FEATURE [Part::Extrusion] Extrude035  label="Extrude fori inferiori switch pompa001"
  Base = -> Sketch031
  Dir = (0,0,1)
  DirMode = 2
  FaceMakerClass = Part::FaceMakerBullseye
  FaceMakerMode = 3
  LengthFwd = 4
  LengthRev = 0
  Placement = pos=(0,0,-1.7) rot=(0,0,1;0rad)
  Solid = true
  Symmetric = false
FEATURE [Part::Extrusion] Extrude036  label="Extrude foro sotto posteriore M3x5x007"
  Base = -> Sketch027
  Dir = (0,0,1)
  DirMode = 2
  FaceMakerClass = Part::FaceMakerBullseye
  FaceMakerMode = 3
  LengthFwd = 6.2
  LengthRev = 0
  Placement = pos=(0,0,-9.6) rot=(0,0,1;0rad)
  Solid = true
  Symmetric = false
FEATURE [Part::Extrusion] Extrude037  label="Extrude foro sotto anteriore M3x5x007"
  Base = -> Sketch026
  Dir = (0,0,1)
  DirMode = 2
  FaceMakerClass = Part::FaceMakerBullseye
  FaceMakerMode = 3
  LengthFwd = 6.2
  LengthRev = 0
  Solid = true
  Symmetric = false
FEATURE [Sketcher::SketchObject] Sketch035  label="foro per fissaggio micro"
  ArcFitTolerance = 1e-06
  AttachmentSupport = -> [XZ_Plane]
  ExternalGeometry = -> [Sketch,Sketch033]
  FullyConstrained = true
  MakeInternals = false
  MapMode = 5
  Placement = pos=(0,0,0) rot=(1,0,0;1.5708rad)
  sketch-geometry (3):
    g0: Circle CenterX=-7.8 CenterY=21.2 CenterZ=0 NormalX=0 NormalY=0 NormalZ=1 AngleXU=0 Radius=1.6
    g1: GeomPoint [constr] X=-4 Y=21.2 Z=0
    g2: LineSegment [constr] StartX=-4 StartY=21.2 StartZ=0 EndX=-11.6 EndY=21.2 EndZ=0
  constraints (6):
    c: Diameter(g0) = 3.2
    c: Symmetric(g-3,g-3,g1)
    c: Coincident(g2,g1)
    c: Horizontal(g2)
    c: DistanceX(g-4,g2) = 0
    c: Symmetric(g2,g1,g0)
FEATURE [Part::Extrusion] Extrude038  label="Extrude foro per fissaggio micro"
  Base = -> Sketch035
  Dir = (0,-1,2e-16)
  DirMode = 2
  FaceMakerClass = Part::FaceMakerBullseye
  FaceMakerMode = 3
  LengthFwd = 3
  LengthRev = 0
  Placement = pos=(0,8.6,0) rot=(0,0,1;0rad)
  Solid = true
  Symmetric = false
FEATURE [Sketcher::SketchObject] Sketch036  label="supporto per alimentatore"
  ArcFitTolerance = 1e-06
  AttachmentSupport = -> [XZ_Plane]
  ExternalGeometry = -> [Sketch,Sketch016,Sketch022]
  FullyConstrained = true
  MakeInternals = false
  MapMode = 5
  Placement = pos=(0,0,0) rot=(1,0,0;1.5708rad)
  sketch-geometry (5):
    g0: LineSegment StartX=-211.843 StartY=-50.0944 StartZ=0 EndX=-211.843 EndY=-80.4316 EndZ=0
    g1: LineSegment StartX=-211.843 StartY=-50.0944 StartZ=0 EndX=-207.775 EndY=-41.3701 EndZ=0
    g2: LineSegment [constr] StartX=-209.443 StartY=-50.0944 StartZ=0 EndX=-209.443 EndY=-80.4316 EndZ=0
    g3: LineSegment StartX=-207.775 StartY=-41.3701 StartZ=0 EndX=-207.775 EndY=-80.4316 EndZ=0
    g4: LineSegment StartX=-211.843 StartY=-80.4316 StartZ=0 EndX=-207.775 EndY=-80.4316 EndZ=0
  constraints (15):
    c: Vertical(g0)
    c: Coincident(g1,g0)
    c: Vertical(g2)
    c: Tangent(g2,g-5)
    c: Coincident(g3,g1)
    c: Vertical(g3)
    c: DistanceY(g-3,g3) = -2
    c: Tangent(g1,g-8)
    c: DistanceY(g-3,g0) = -2
    c: Coincident(g4,g0)
    c: Coincident(g4,g3)
    c: Tangent(g0,g-6)
    c: DistanceY(g-3,g2) = -2
    c: DistanceY(g2,g0) = 0
    c: DistanceX(g-3,g3) = 6.8
FEATURE [Part::Extrusion] Extrude039  label="Extrude039 supporto alimentatore"
  Base = -> Sketch036
  Dir = (0,-1,2e-16)
  DirMode = 2
  FaceMakerClass = Part::FaceMakerBullseye
  FaceMakerMode = 3
  LengthFwd = 25.2
  LengthRev = 0
  Solid = true
  Symmetric = true
FEATURE [Sketcher::SketchObject] Sketch037  label="scavo per alimentatore"
  ArcFitTolerance = 1e-06
  AttachmentSupport = -> [XZ_Plane]
  ExternalGeometry = -> [Sketch036]
  FullyConstrained = true
  MakeInternals = false
  MapMode = 5
  Placement = pos=(0,0,0) rot=(1,0,0;1.5708rad)
  sketch-geometry (4):
    g0: LineSegment StartX=-209.575 StartY=-50.4316 StartZ=0 EndX=-209.575 EndY=-80.4316 EndZ=0
    g1: LineSegment StartX=-209.575 StartY=-50.4316 StartZ=0 EndX=-207.775 EndY=-50.4316 EndZ=0
    g2: LineSegment StartX=-207.775 StartY=-50.4316 StartZ=0 EndX=-207.775 EndY=-80.4316 EndZ=0
    g3: LineSegment StartX=-207.775 StartY=-80.4316 StartZ=0 EndX=-209.575 EndY=-80.4316 EndZ=0
  constraints (11):
    c: Vertical(g0)
    c: Coincident(g1,g0)
    c: Horizontal(g1)
    c: Coincident(g2,g1)
    c: Vertical(g2)
    c: Coincident(g3,g2)
    c: Coincident(g3,g0)
    c: Horizontal(g3)
    c: DistanceX(g1,g1) = 1.8
    c: Coincident(g2,g-3)
    c: DistanceY(g2,g2) = 30
FEATURE [Part::Extrusion] Extrude040  label="Extrude040 scavo alimentatore"
  Base = -> Sketch037
  Dir = (0,-1,2e-16)
  DirMode = 2
  FaceMakerClass = Part::FaceMakerBullseye
  FaceMakerMode = 3
  LengthFwd = 19.5
  LengthRev = 0
  Solid = true
  Symmetric = true
FEATURE [Part::Extrusion] Extrude031  label="Extrude fermo per scheda micro"
  Base = -> Sketch033
  Dir = (0,-1,2e-16)
  DirMode = 2
  FaceMakerClass = Part::FaceMakerBullseye
  FaceMakerMode = 3
  LengthFwd = 3
  LengthRev = 0
  Placement = pos=(0,8.6,0) rot=(0,0,1;0rad)
  Solid = true
  Symmetric = false
FEATURE [Sketcher::SketchObject] Sketch038  label="scavo driver solenoide"
  ArcFitTolerance = 1e-06
  AttachmentSupport = -> [XZ_Plane]
  ExternalGeometry = -> [Sketch,Sketch036]
  FullyConstrained = true
  MakeInternals = false
  MapMode = 5
  Placement = pos=(0,0,0) rot=(1,0,0;1.5708rad)
  sketch-geometry (7):
    g0: LineSegment StartX=-192.222 StartY=-8.0175 StartZ=0 EndX=-194.941 EndY=-6.74965 EndZ=0
    g1: LineSegment StartX=-194.941 StartY=-6.74965 StartZ=0 EndX=-212.269 EndY=-43.9083 EndZ=0
    g2: LineSegment StartX=-192.222 StartY=-8.0175 StartZ=0 EndX=-188.779 EndY=-9.62345 EndZ=0
    g3: LineSegment StartX=-188.779 StartY=-9.62345 StartZ=0 EndX=-205.357 EndY=-45.1761 EndZ=0
    g4: LineSegment StartX=-205.357 StartY=-45.1761 StartZ=0 EndX=-209.55 EndY=-45.1761 EndZ=0
    g5: LineSegment [constr] StartX=-212.269 StartY=-43.9083 StartZ=0 EndX=-209.55 EndY=-45.1761 EndZ=0
    g6: LineSegment StartX=-212.269 StartY=-43.9083 StartZ=0 EndX=-209.55 EndY=-45.1761 EndZ=0
  constraints (20):
    c: Coincident(g1,g0)
    c: Coincident(g3,g2)
    c: Coincident(g4,g3)
    c: Distance(g2) = 3.8
    c: Distance(g1) = 41
    c: Coincident(g5,g1)
    c: Distance(g5) = 3
    c: Perpendicular(g5,g-3)
    c: Parallel(g1,g-3)
    c: Perpendicular(g1,g0)
    c: Distance(g0) = 3
    c: Coincident(g6,g1)
    c: Parallel(g3,g-3)
    c: Perpendicular(g2,g3)
    c: Coincident(g2,g0)
    c: Perpendicular(g-4,g4)
    c: PointOnObject(g5,g-3)
    c: Distance(g-3,g5) = 9.6
    c: Coincident(g4,g5)
    c: Coincident(g6,g4)
FEATURE [Part::Extrusion] Extrude041  label="Extrude scavo driver solenoide"
  Base = -> Sketch038
  Dir = (0,-1,2e-16)
  DirMode = 2
  FaceMakerClass = Part::FaceMakerBullseye
  FaceMakerMode = 3
  LengthFwd = 20.6
  LengthRev = 0
  Solid = true
  Symmetric = true
FEATURE [Sketcher::SketchObject] Sketch039  label="scavo per cavo usb per micro"
  ArcFitTolerance = 1e-06
  AttachmentSupport = -> [XZ_Plane]
  ExternalGeometry = -> [Sketch,Sketch016]
  FullyConstrained = true
  MakeInternals = false
  MapMode = 5
  Placement = pos=(0,0,0) rot=(1,0,0;1.5708rad)
  sketch-geometry (4):
    g0: LineSegment StartX=-82.51 StartY=36.4 StartZ=0 EndX=-74.51 EndY=36.4 EndZ=0
    g1: LineSegment StartX=-74.51 StartY=36.4 StartZ=0 EndX=-74.51 EndY=30.8 EndZ=0
    g2: LineSegment StartX=-74.51 StartY=30.8 StartZ=0 EndX=-82.51 EndY=30.8 EndZ=0
    g3: LineSegment StartX=-82.51 StartY=30.8 StartZ=0 EndX=-82.51 EndY=36.4 EndZ=0
  constraints (11):
    c: Coincident(g1,g0)
    c: Vertical(g1)
    c: Coincident(g2,g1)
    c: Horizontal(g2)
    c: Coincident(g3,g2)
    c: Coincident(g3,g0)
    c: Vertical(g3)
    c: Tangent(g0,g-3)
    c: Tangent(g2,g-4)
    c: Tangent(g3,g-4)
    c: Tangent(g1,g-4)
FEATURE [Part::Extrusion] Extrude042  label="Extrude scavo per cavo usb per micro"
  Base = -> Sketch039
  Dir = (0,-1,2e-16)
  DirMode = 2
  FaceMakerClass = Part::FaceMakerBullseye
  FaceMakerMode = 3
  LengthFwd = 11.2
  LengthRev = 0
  Solid = true
  Symmetric = true
FEATURE [Sketcher::SketchObject] Sketch040  label="scavo saldature alimentatore connettore 5v"
  ArcFitTolerance = 1e-06
  AttachmentSupport = -> [XZ_Plane]
  ExternalGeometry = -> [Sketch037]
  FullyConstrained = true
  MakeInternals = false
  MapMode = 5
  Placement = pos=(0,0,0) rot=(1,0,0;1.5708rad)
  sketch-geometry (4):
    g0: LineSegment StartX=-211.175 StartY=-52.4316 StartZ=0 EndX=-211.175 EndY=-56.4316 EndZ=0
    g1: LineSegment StartX=-211.175 StartY=-52.4316 StartZ=0 EndX=-209.575 EndY=-52.4316 EndZ=0
    g2: LineSegment StartX=-209.575 StartY=-52.4316 StartZ=0 EndX=-209.575 EndY=-56.4316 EndZ=0
    g3: LineSegment StartX=-209.575 StartY=-56.4316 StartZ=0 EndX=-211.175 EndY=-56.4316 EndZ=0
  constraints (11):
    c: Vertical(g0)
    c: Coincident(g1,g0)
    c: Horizontal(g1)
    c: Coincident(g2,g1)
    c: Coincident(g3,g2)
    c: Coincident(g3,g0)
    c: Horizontal(g3)
    c: DistanceX(g1,g1) = 1.6
    c: DistanceY(g2,g2) = 4
    c: Tangent(g2,g-3)
    c: DistanceY(g1,g-3) = 2
FEATURE [Part::Extrusion] Extrude043  label="Extrude scavo saldature alimentatore connettore 5v"
  Base = -> Sketch040
  Dir = (0,-1,2e-16)
  DirMode = 2
  FaceMakerClass = Part::FaceMakerBullseye
  FaceMakerMode = 3
  LengthFwd = 8
  LengthRev = 0
  Solid = true
  Symmetric = true
FEATURE [Sketcher::SketchObject] Sketch041  label="scavo saldature alimentatore connettore 5v verticali"
  ArcFitTolerance = 1e-06
  AttachmentSupport = -> [XZ_Plane]
  ExternalGeometry = -> [Sketch037]
  FullyConstrained = true
  MakeInternals = false
  MapMode = 5
  Placement = pos=(0,0,0) rot=(1,0,0;1.5708rad)
  sketch-geometry (4):
    g0: LineSegment StartX=-211.175 StartY=-53.6316 StartZ=0 EndX=-209.575 EndY=-53.6316 EndZ=0
    g1: LineSegment StartX=-209.575 StartY=-53.6316 StartZ=0 EndX=-209.575 EndY=-76.6316 EndZ=0
    g2: LineSegment StartX=-209.575 StartY=-76.6316 StartZ=0 EndX=-211.175 EndY=-76.6316 EndZ=0
    g3: LineSegment StartX=-211.175 StartY=-76.6316 StartZ=0 EndX=-211.175 EndY=-53.6316 EndZ=0
  constraints (11):
    c: Horizontal(g0)
    c: Coincident(g1,g0)
    c: Coincident(g2,g1)
    c: Horizontal(g2)
    c: Coincident(g3,g2)
    c: Coincident(g3,g0)
    c: Vertical(g3)
    c: DistanceY(g3,g3) = 23
    c: DistanceX(g0,g0) = 1.6
    c: Tangent(g1,g-3)
    c: DistanceY(g0,g-3) = 3.2
FEATURE [Part::Extrusion] Extrude044  label="Extrude scavo saldature alimentatore connettore 5v verticali"
  Base = -> Sketch041
  Dir = (0,-1,2e-16)
  DirMode = 2
  FaceMakerClass = Part::FaceMakerBullseye
  FaceMakerMode = 3
  LengthFwd = 3.2
  LengthRev = 0
  Placement = pos=(0,8.3,0) rot=(0,0,1;0rad)
  Solid = true
  Symmetric = false
FEATURE [Sketcher::SketchObject] Sketch042  label="fermi per driver solenoide e alimentatore"
  ArcFitTolerance = 1e-06
  AttachmentSupport = -> [XZ_Plane]
  ExternalGeometry = -> [Sketch036,Sketch037,Sketch,Sketch038]
  FullyConstrained = true
  MakeInternals = false
  MapMode = 5
  Placement = pos=(0,0,0) rot=(1,0,0;1.5708rad)
  sketch-geometry (27):
    g0: LineSegment StartX=-200.59 StartY=-25.9624 StartZ=0 EndX=-201.52 EndY=-27.9563 EndZ=0
    g1: LineSegment StartX=-201.52 StartY=-27.9563 StartZ=0 EndX=-199.526 EndY=-28.886 EndZ=0
    g2: LineSegment StartX=-199.526 StartY=-28.886 StartZ=0 EndX=-198.596 EndY=-26.8922 EndZ=0
    g3: LineSegment StartX=-198.596 StartY=-26.8922 StartZ=0 EndX=-200.59 EndY=-25.9624 EndZ=0
    g4: LineSegment StartX=-201.364 StartY=-23.8361 StartZ=0 EndX=-203.646 EndY=-28.7302 EndZ=0
    g5: LineSegment StartX=-203.646 StartY=-28.7302 StartZ=0 EndX=-200.202 EndY=-30.3361 EndZ=0
    g6: LineSegment StartX=-198.076 StartY=-29.5622 StartZ=0 EndX=-197.146 EndY=-27.5683 EndZ=0
    g7: LineSegment StartX=-197.92 StartY=-25.4421 StartZ=0 EndX=-201.364 EndY=-23.8361 EndZ=0
    g8: LineSegment [constr] StartX=-198.752 StartY=-31.0123 StartZ=0 EndX=-198.076 EndY=-29.5622 EndZ=0
    g9: LineSegment [constr] StartX=-198.752 StartY=-31.0123 StartZ=0 EndX=-200.202 EndY=-30.3361 EndZ=0
    g10: ArcOfCircle CenterX=-198.596 CenterY=-26.8922 CenterZ=0 NormalX=0 NormalY=0 NormalZ=1 AngleXU=0 Radius=1.6 StartAngle=5.84685 EndAngle=7.41765
    g11: GeomPoint [constr] X=-196.47 Y=-26.1183 Z=0
    g12: ArcOfCircle CenterX=-199.526 CenterY=-28.886 CenterZ=0 NormalX=0 NormalY=0 NormalZ=1 AngleXU=0 Radius=1.6 StartAngle=4.27606 EndAngle=5.84685
    g13: GeomPoint [constr] X=-198.752 Y=-31.0123 Z=0
    g14: LineSegment StartX=-207.775 StartY=-46.8316 StartZ=0 EndX=-207.775 EndY=-50.8316 EndZ=0
    g15: LineSegment StartX=-207.775 StartY=-46.8316 StartZ=0 EndX=-203.775 EndY=-46.8316 EndZ=0
    g16: LineSegment StartX=-203.775 StartY=-46.8316 StartZ=0 EndX=-203.775 EndY=-50.8316 EndZ=0
    g17: LineSegment StartX=-207.775 StartY=-50.8316 StartZ=0 EndX=-203.775 EndY=-50.8316 EndZ=0
    g18: LineSegment StartX=-209.375 StartY=-52.4316 StartZ=0 EndX=-203.775 EndY=-52.4316 EndZ=0
    g19: LineSegment StartX=-202.175 StartY=-50.8316 StartZ=0 EndX=-202.175 EndY=-46.8316 EndZ=0
    g20: LineSegment StartX=-203.775 StartY=-45.2316 StartZ=0 EndX=-209.375 EndY=-45.2316 EndZ=0
    g21: LineSegment StartX=-209.375 StartY=-45.2316 StartZ=0 EndX=-209.375 EndY=-52.4316 EndZ=0
    g22: ArcOfCircle CenterX=-203.775 CenterY=-46.8316 CenterZ=0 NormalX=0 NormalY=0 NormalZ=1 AngleXU=0 Radius=1.6 StartAngle=1.8e-15 EndAngle=1.5708
    g23: GeomPoint [constr] X=-202.175 Y=-45.2316 Z=0
    g24: ArcOfCircle CenterX=-203.775 CenterY=-50.8316 CenterZ=0 NormalX=0 NormalY=0 NormalZ=1 AngleXU=0 Radius=1.6 StartAngle=4.71239 EndAngle=6.28319
    g25: GeomPoint [constr] X=-202.175 Y=-52.4316 Z=0
    g26: LineSegment [constr] StartX=-207.775 StartY=-50.4316 StartZ=0 EndX=-207.775 EndY=-50.8316 EndZ=0
  constraints (69):
    c: Coincident(g1,g0)
    c: Coincident(g2,g1)
    c: Coincident(g3,g2)
    c: Coincident(g3,g0)
    c: Parallel(g0,g2)
    c: Perpendicular(g3,g0)
    c: Perpendicular(g1,g0)
    c: Coincident(g5,g4)
    c: Coincident(g7,g4)
    c: Distance(g3) = 2.2
    c: Distance(g2) = 2.2
    c: Parallel(g6,g2)
    c: Parallel(g6,g4)
    c: Perpendicular(g5,g6)
    c: Perpendicular(g7,g6)
    c: Distance(g13,g11) = 5.4
    c: Distance(g5,g13) = 5.4
    c: Coincident(g9,g8)
    c: Distance(g8) = 1.6
    c: Distance(g9) = 1.6
    c: Perpendicular(g9,g8)
    c: Parallel(g8,g6)
    c: Coincident(g8,g13)
    c: Distance(g8,g1) = 1.6
    c: Distance(g9,g1) = 1.6
    c: Tangent(g0,g-5)
    c: Distance(g0,g-6) = 19
    c: PointOnObject(g11,g7)
    c: PointOnObject(g11,g6)
    c: Tangent(g7,g10) = -1.5708
    c: Tangent(g6,g10) = -1.5708
    c: PointOnObject(g13,g5)
    c: Tangent(g5,g12) = -1.5708
    c: Tangent(g6,g12) = -1.5708
    c: Equal(g10,g12)
    c: Coincident(g10,g2)
    c: Vertical(g14)
    c: Coincident(g15,g14)
    c: Horizontal(g15)
    c: Coincident(g16,g15)
    c: Vertical(g16)
    c: Coincident(g17,g14)
    c: Coincident(g17,g16)
    c: Horizontal(g17)
    c: Distance(g16) = 4
    c: Distance(g15) = 4
    c: Horizontal(g18)
    c: Vertical(g19)
    c: Horizontal(g20)
    c: Coincident(g21,g20)
    c: Coincident(g21,g18)
    c: Vertical(g21)
    c: Distance(g20,g23) = 7.2
    c: Distance(g25,g23) = 7.2
    c: DistanceY(g18,g14) = 1.6
    c: DistanceX(g18,g14) = 1.6
    c: PointOnObject(g23,g20)
    c: PointOnObject(g23,g19)
    c: Tangent(g20,g22) = -1.5708
    c: Tangent(g19,g22) = -1.5708
    c: PointOnObject(g25,g19)
    c: Tangent(g18,g24) = -1.5708
    c: Tangent(g19,g24) = -1.5708
    c: Equal(g22,g24)
    c: Coincident(g22,g15)
    c: Vertical(g26)
    c: Distance(g26) = 0.4
    c: Coincident(g26,g-4)
    c: Coincident(g14,g26)
FEATURE [Part::Extrusion] Extrude045  label="Extrude fermi per driver solenoide e alimentatore"
  Base = -> Sketch042
  Dir = (0,-1,2e-16)
  DirMode = 2
  FaceMakerClass = Part::FaceMakerBullseye
  FaceMakerMode = 3
  LengthFwd = 25.2
  LengthRev = 0
  Solid = true
  Symmetric = true
FEATURE [Sketcher::SketchObject] Sketch043  label="scavo pulizia fermo alimentatore"
  ArcFitTolerance = 1e-06
  AttachmentSupport = -> [XZ_Plane]
  ExternalGeometry = -> [Sketch042,Sketch036,Sketch037]
  FullyConstrained = true
  MakeInternals = false
  MapMode = 5
  Placement = pos=(0,0,0) rot=(1,0,0;1.5708rad)
  sketch-geometry (6):
    g0: LineSegment StartX=-209.375 StartY=-52.4316 StartZ=0 EndX=-209.375 EndY=-50.4316 EndZ=0
    g1: LineSegment StartX=-209.375 StartY=-50.4316 StartZ=0 EndX=-207.775 EndY=-50.4316 EndZ=0
    g2: LineSegment StartX=-207.775 StartY=-50.4316 StartZ=0 EndX=-207.775 EndY=-45.2316 EndZ=0
    g3: LineSegment StartX=-207.775 StartY=-45.2316 StartZ=0 EndX=-202.175 EndY=-45.2316 EndZ=0
    g4: LineSegment StartX=-202.175 StartY=-45.2316 StartZ=0 EndX=-202.175 EndY=-52.4316 EndZ=0
    g5: LineSegment StartX=-202.175 StartY=-52.4316 StartZ=0 EndX=-209.375 EndY=-52.4316 EndZ=0
  constraints (13):
    c: Vertical(g0)
    c: Coincident(g1,g0)
    c: Coincident(g2,g1)
    c: Coincident(g3,g2)
    c: Coincident(g4,g3)
    c: Coincident(g5,g4)
    c: Coincident(g5,g0)
    c: Horizontal(g5)
    c: Coincident(g0,g-6)
    c: Tangent(g1,g-8)
    c: Tangent(g2,g-4)
    c: Tangent(g3,g-7)
    c: Tangent(g4,g-3)
FEATURE [Part::Extrusion] Extrude046  label="Extrude scavo pulizia fermo alimentatore"
  Base = -> Sketch043
  Dir = (0,-1,2e-16)
  DirMode = 2
  FaceMakerClass = Part::FaceMakerBullseye
  FaceMakerMode = 3
  LengthFwd = 19.5
  LengthRev = 0
  Solid = true
  Symmetric = true
FEATURE [Sketcher::SketchObject] Sketch044  label="buchini per fissaggio oled"
  ArcFitTolerance = 1e-06
  AttachmentSupport = -> [YZ_Plane]
  ExternalGeometry = -> [Sketch]
  FullyConstrained = true
  MakeInternals = false
  MapMode = 5
  Placement = pos=(0,0,0) rot=(0.57735,0.57735,0.57735;2.0944rad)
  sketch-geometry (5):
    g0: LineSegment [constr] StartX=1.5e-14 StartY=67.3588 StartZ=0 EndX=0 EndY=64.3588 EndZ=0
    g1: LineSegment [constr] StartX=0 StartY=64.3588 StartZ=0 EndX=10.4 EndY=64.3588 EndZ=0
    g2: LineSegment [constr] StartX=0 StartY=64.3588 StartZ=0 EndX=-10.4 EndY=64.3588 EndZ=0
    g3: Circle CenterX=10.4 CenterY=64.3588 CenterZ=0 NormalX=0 NormalY=0 NormalZ=1 AngleXU=0 Radius=1.5
    g4: Circle CenterX=-10.4 CenterY=64.3588 CenterZ=0 NormalX=0 NormalY=0 NormalZ=1 AngleXU=0 Radius=1.5
  constraints (13):
    c: Distance(g0) = 3
    c: PointOnObject(g0,g-2)
    c: Coincident(g1,g0)
    c: Horizontal(g1)
    c: Coincident(g2,g0)
    c: Horizontal(g2)
    c: DistanceX(g1,g1) = 10.4
    c: Coincident(g3,g1)
    c: Diameter(g4) = 3
    c: Coincident(g4,g2)
    c: Coincident(g0,g-7)
    c: Equal(g1,g2)
    c: Equal(g4,g3)
FEATURE [Part::Extrusion] Extrude047  label="Extrude buchini per fissaggio oled"
  Base = -> Sketch044
  Dir = (1,0,0)
  DirMode = 2
  FaceMakerClass = Part::FaceMakerBullseye
  FaceMakerMode = 3
  LengthFwd = 10
  LengthRev = 0
  Placement = pos=(-186,0,0) rot=(0,0,1;0rad)
  Solid = true
  Symmetric = false
FEATURE [Sketcher::SketchObject] Sketch046  label="scavo 5x5 neopixel"
  ArcFitTolerance = 1e-06
  AttachmentSupport = -> [YZ_Plane002]
  FullyConstrained = true
  MakeInternals = false
  MapMode = 5
  Placement = pos=(0,0,0) rot=(0.57735,0.57735,0.57735;2.0944rad)
  sketch-geometry (4):
    g0: LineSegment StartX=-2.7 StartY=2.7 StartZ=0 EndX=2.7 EndY=2.7 EndZ=0
    g1: LineSegment StartX=2.7 StartY=2.7 StartZ=0 EndX=2.7 EndY=-2.7 EndZ=0
    g2: LineSegment StartX=2.7 StartY=-2.7 StartZ=0 EndX=-2.7 EndY=-2.7 EndZ=0
    g3: LineSegment StartX=-2.7 StartY=-2.7 StartZ=0 EndX=-2.7 EndY=2.7 EndZ=0
  constraints (11):
    c: Horizontal(g0)
    c: Coincident(g1,g0)
    c: Vertical(g1)
    c: Coincident(g2,g1)
    c: Horizontal(g2)
    c: Coincident(g3,g2)
    c: Coincident(g3,g0)
    c: Vertical(g3)
    c: DistanceX(g0,g0) = 5.4
    c: DistanceY(g1,g1) = 5.4
    c: Symmetric(g0,g1,g-1)
FEATURE [Sketcher::SketchObject] Sketch047  label="scavo 10x10 neopixel corpo"
  ArcFitTolerance = 1e-06
  AttachmentOffset = pos=(0,0,1) rot=(0,0,1;0rad)
  AttachmentSupport = -> [YZ_Plane002]
  FullyConstrained = true
  MakeInternals = false
  MapMode = 5
  Placement = pos=(1,0,0) rot=(0.57735,0.57735,0.57735;2.0944rad)
  sketch-geometry (4):
    g0: LineSegment StartX=-5 StartY=5.1 StartZ=0 EndX=5 EndY=5.1 EndZ=0
    g1: LineSegment StartX=5 StartY=5.1 StartZ=0 EndX=5 EndY=-5.1 EndZ=0
    g2: LineSegment StartX=5 StartY=-5.1 StartZ=0 EndX=-5 EndY=-5.1 EndZ=0
    g3: LineSegment StartX=-5 StartY=-5.1 StartZ=0 EndX=-5 EndY=5.1 EndZ=0
  constraints (11):
    c: Horizontal(g0)
    c: Coincident(g1,g0)
    c: Vertical(g1)
    c: Coincident(g2,g1)
    c: Horizontal(g2)
    c: Coincident(g3,g2)
    c: Coincident(g3,g0)
    c: Vertical(g3)
    c: DistanceX(g0,g0) = 10
    c: DistanceY(g1,g1) = 10.2
    c: Symmetric(g0,g2,g-1)
FEATURE [Sketcher::SketchObject] Sketch048  label="buco per perno blocco neopixel"
  ArcFitTolerance = 1e-06
  AttachmentSupport = -> [XZ_Plane002]
  FullyConstrained = true
  MakeInternals = false
  MapMode = 5
  Placement = pos=(0,0,0) rot=(1,0,0;1.5708rad)
  sketch-geometry (4):
    g0: LineSegment StartX=3 StartY=1.2 StartZ=0 EndX=3 EndY=-1.2 EndZ=0
    g1: LineSegment StartX=3 StartY=-1.2 StartZ=0 EndX=5.4 EndY=-1.2 EndZ=0
    g2: LineSegment StartX=5.4 StartY=-1.2 StartZ=0 EndX=5.4 EndY=1.2 EndZ=0
    g3: LineSegment StartX=5.4 StartY=1.2 StartZ=0 EndX=3 EndY=1.2 EndZ=0
  constraints (11):
    c: Coincident(g1,g0)
    c: Horizontal(g1)
    c: Coincident(g2,g1)
    c: Vertical(g2)
    c: Coincident(g3,g2)
    c: Coincident(g3,g0)
    c: Horizontal(g3)
    c: DistanceX(g1,g1) = 2.4
    c: DistanceY(g2,g2) = 2.4
    c: Symmetric(g0,g0,g-1)
    c: DistanceX(g-1,g0) = 3
FEATURE [Sketcher::SketchObject] Sketch045  label="blocco principale per neopixel"
  ArcFitTolerance = 1e-06
  AttachmentSupport = -> [XZ_Plane002]
  ExternalGeometry = -> [Sketch048]
  FullyConstrained = true
  MakeInternals = false
  MapMode = 5
  Placement = pos=(0,0,0) rot=(1,0,0;1.5708rad)
  sketch-geometry (6):
    g0: LineSegment StartX=0 StartY=5.1 StartZ=0 EndX=0 EndY=-5.1 EndZ=0
    g1: LineSegment StartX=0 StartY=-5.1 StartZ=0 EndX=3 EndY=-5.1 EndZ=0
    g2: LineSegment StartX=7 StartY=-1.1 StartZ=0 EndX=7 EndY=5.1 EndZ=0
    g3: LineSegment StartX=7 StartY=5.1 StartZ=0 EndX=0 EndY=5.1 EndZ=0
    g4: ArcOfCircle CenterX=3 CenterY=-1.1 CenterZ=0 NormalX=0 NormalY=0 NormalZ=1 AngleXU=0 Radius=4 StartAngle=4.71239 EndAngle=6.28319
    g5: GeomPoint [constr] X=7 Y=-5.1 Z=0
  constraints (15):
    c: Vertical(g0)
    c: Coincident(g1,g0)
    c: Horizontal(g1)
    c: Vertical(g2)
    c: Coincident(g3,g2)
    c: Coincident(g3,g0)
    c: Horizontal(g3)
    c: DistanceY(g0,g0) = 10.2
    c: Symmetric(g0,g0,g-1)
    c: DistanceX(g3,g3) = 7
    c: PointOnObject(g5,g2)
    c: PointOnObject(g5,g1)
    c: Tangent(g2,g4) = -1.5708
    c: Tangent(g1,g4) = -1.5708
    c: DistanceX(g-3,g1) = 0
FEATURE [Sketcher::SketchObject] Sketch049  label="rinforzi esterni per corpo neopoixel"
  ArcFitTolerance = 1e-06
  AttachmentSupport = -> [XZ_Plane002]
  ExternalGeometry = -> [Sketch045]
  FullyConstrained = true
  MakeInternals = false
  MapMode = 5
  Placement = pos=(0,0,0) rot=(1,0,0;1.5708rad)
  sketch-geometry (8):
    g0: LineSegment StartX=1 StartY=-4.1 StartZ=0 EndX=2 EndY=-4.1 EndZ=0
    g1: LineSegment StartX=2 StartY=-4.1 StartZ=0 EndX=2 EndY=-5.1 EndZ=0
    g2: LineSegment StartX=2 StartY=-5.1 StartZ=0 EndX=1 EndY=-5.1 EndZ=0
    g3: LineSegment StartX=1 StartY=-5.1 StartZ=0 EndX=1 EndY=-4.1 EndZ=0
    g4: LineSegment StartX=1 StartY=5.1 StartZ=0 EndX=2 EndY=5.1 EndZ=0
    g5: LineSegment StartX=2 StartY=5.1 StartZ=0 EndX=2 EndY=4.1 EndZ=0
    g6: LineSegment StartX=2 StartY=4.1 StartZ=0 EndX=1 EndY=4.1 EndZ=0
    g7: LineSegment StartX=1 StartY=4.1 StartZ=0 EndX=1 EndY=5.1 EndZ=0
  constraints (24):
    c: Horizontal(g0)
    c: Coincident(g1,g0)
    c: Vertical(g1)
    c: Coincident(g2,g1)
    c: Horizontal(g2)
    c: Coincident(g3,g2)
    c: Coincident(g3,g0)
    c: Vertical(g3)
    c: Horizontal(g4)
    c: Coincident(g5,g4)
    c: Vertical(g5)
    c: Coincident(g6,g5)
    c: Horizontal(g6)
    c: Coincident(g7,g6)
    c: Coincident(g7,g4)
    c: Vertical(g7)
    c: DistanceX(g4,g4) = 1
    c: DistanceY(g5,g5) = 1
    c: DistanceX(g0,g0) = 1
    c: DistanceY(g1,g1) = 1
    c: DistanceX(g-3,g4) = 1
    c: DistanceY(g-3,g4) = 0
    c: DistanceX(g-4,g2) = 1
    c: DistanceY(g2,g-4) = 0
FEATURE [Sketcher::SketchObject] Sketch052  label="scavo saldature driver solenoide"
  ArcFitTolerance = 1e-06
  AttachmentSupport = -> [XZ_Plane]
  ExternalGeometry = -> [Sketch038]
  FullyConstrained = true
  MakeInternals = false
  MapMode = 5
  Placement = pos=(0,0,0) rot=(1,0,0;1.5708rad)
  sketch-geometry (4):
    g0: LineSegment StartX=-195.304 StartY=-6.5806 StartZ=0 EndX=-196.994 EndY=-10.2058 EndZ=0
    g1: LineSegment StartX=-196.994 StartY=-10.2058 StartZ=0 EndX=-196.632 EndY=-10.3749 EndZ=0
    g2: LineSegment StartX=-196.632 StartY=-10.3749 StartZ=0 EndX=-194.941 EndY=-6.74965 EndZ=0
    g3: LineSegment StartX=-194.941 StartY=-6.74965 StartZ=0 EndX=-195.304 EndY=-6.5806 EndZ=0
  constraints (11):
    c: Coincident(g1,g0)
    c: Coincident(g2,g1)
    c: Coincident(g3,g2)
    c: Coincident(g3,g0)
    c: Parallel(g2,g0)
    c: Perpendicular(g2,g3)
    c: Perpendicular(g1,g2,g1) = 1.5708
    c: Parallel(g2,g-3)
    c: Distance(g2) = 4
    c: Distance(g3) = 0.4
    c: Coincident(g2,g-3)
FEATURE [Part::Extrusion] Extrude055  label="Extrude scavo saldature driver solenoide"
  Base = -> Sketch052
  Dir = (0,-1,2e-16)
  DirMode = 2
  FaceMakerClass = Part::FaceMakerBullseye
  FaceMakerMode = 3
  LengthFwd = 6
  LengthRev = 0
  Solid = true
  Symmetric = true
FEATURE [Sketcher::SketchObject] Sketch053  label="scavo saldature rumble"
  ArcFitTolerance = 1e-06
  AttachmentSupport = -> [XZ_Plane]
  ExternalGeometry = -> [Sketch019]
  FullyConstrained = true
  MakeInternals = false
  MapMode = 5
  Placement = pos=(0,0,0) rot=(1,0,0;1.5708rad)
  sketch-geometry (4):
    g0: LineSegment StartX=-165.001 StartY=-43.1663 StartZ=0 EndX=-166.238 EndY=-46.9705 EndZ=0
    g1: LineSegment StartX=-166.238 StartY=-46.9705 StartZ=0 EndX=-165.096 EndY=-47.3413 EndZ=0
    g2: LineSegment StartX=-165.096 StartY=-47.3413 StartZ=0 EndX=-163.86 EndY=-43.5371 EndZ=0
    g3: LineSegment StartX=-163.86 StartY=-43.5371 StartZ=0 EndX=-165.001 EndY=-43.1663 EndZ=0
  constraints (11):
    c: Coincident(g1,g0)
    c: Coincident(g2,g1)
    c: Coincident(g3,g2)
    c: Coincident(g3,g0)
    c: Parallel(g0,g2)
    c: Perpendicular(g3,g0)
    c: Perpendicular(g1,g0)
    c: Parallel(g0,g-3)
    c: Distance(g0) = 4
    c: Distance(g1) = 1.2
    c: Coincident(g0,g-3)
FEATURE [Part::Extrusion] Extrude056  label="Extrude scavo saldature rumble"
  Base = -> Sketch053
  Dir = (0,-1,2e-16)
  DirMode = 2
  FaceMakerClass = Part::FaceMakerBullseye
  FaceMakerMode = 3
  LengthFwd = 8.4
  LengthRev = 0
  Solid = true
  Symmetric = true
FEATURE [Sketcher::SketchObject] Sketch054  label="scavo saldature alimentatore connettore USB"
  ArcFitTolerance = 1e-06
  AttachmentSupport = -> [XZ_Plane]
  ExternalGeometry = -> [Sketch037]
  FullyConstrained = true
  MakeInternals = false
  MapMode = 5
  Placement = pos=(0,0,0) rot=(1,0,0;1.5708rad)
  sketch-geometry (4):
    g0: LineSegment StartX=-209.575 StartY=-80.4316 StartZ=0 EndX=-210.375 EndY=-80.4316 EndZ=0
    g1: LineSegment StartX=-210.375 StartY=-80.4316 StartZ=0 EndX=-210.375 EndY=-72.4316 EndZ=0
    g2: LineSegment StartX=-210.375 StartY=-72.4316 StartZ=0 EndX=-209.575 EndY=-72.4316 EndZ=0
    g3: LineSegment StartX=-209.575 StartY=-72.4316 StartZ=0 EndX=-209.575 EndY=-80.4316 EndZ=0
  constraints (11):
    c: Horizontal(g0)
    c: Coincident(g1,g0)
    c: Vertical(g1)
    c: Coincident(g2,g1)
    c: Horizontal(g2)
    c: Coincident(g3,g2)
    c: Coincident(g3,g0)
    c: Vertical(g3)
    c: DistanceX(g0,g0) = 0.8
    c: DistanceY(g3,g3) = 8
    c: Coincident(g0,g-4)
FEATURE [Part::Extrusion] Extrude057  label="Extrude scavo saldature alimentatore connettore USB"
  Base = -> Sketch054
  Dir = (0,-1,2e-16)
  DirMode = 2
  FaceMakerClass = Part::FaceMakerBullseye
  FaceMakerMode = 3
  LengthFwd = 11
  LengthRev = 0
  Solid = true
  Symmetric = true
FEATURE [Sketcher::SketchObject] Sketch055  label="buco interno per micro switch"
  ArcFitTolerance = 1e-06
  AttachmentSupport = -> [XZ_Plane]
  ExternalGeometry = -> [Sketch]
  FullyConstrained = true
  MakeInternals = false
  MapMode = 5
  Placement = pos=(0,0,0) rot=(1,0,0;1.5708rad)
  sketch-geometry (11):
    g0: LineSegment [constr] StartX=-194.483 StartY=34.2854 StartZ=0 EndX=-196.022 EndY=30.0568 EndZ=0
    g1: LineSegment [constr] StartX=-196.022 StartY=30.0568 StartZ=0 EndX=-197.561 EndY=25.8282 EndZ=0
    g2: LineSegment [constr] StartX=-196.022 StartY=30.0568 StartZ=0 EndX=-194.143 EndY=29.3727 EndZ=0
    g3: LineSegment [constr] StartX=-196.022 StartY=30.0568 StartZ=0 EndX=-197.902 EndY=30.7408 EndZ=0
    g4: LineSegment StartX=-196.362 StartY=34.9694 StartZ=0 EndX=-192.604 EndY=33.6014 EndZ=0
    g5: LineSegment StartX=-199.441 StartY=26.5122 StartZ=0 EndX=-195.682 EndY=25.1441 EndZ=0
    g6: LineSegment StartX=-192.604 StartY=33.6014 StartZ=0 EndX=-195.682 EndY=25.1441 EndZ=0
    g7: LineSegment StartX=-196.362 StartY=34.9694 StartZ=0 EndX=-199.441 EndY=26.5122 EndZ=0
    g8: GeomPoint [constr] X=-187.821 Y=29.2 Z=0
    g9: LineSegment [constr] StartX=-188.505 StartY=27.3206 StartZ=0 EndX=-196.022 EndY=30.0568 EndZ=0
    g10: LineSegment [constr] StartX=-187.821 StartY=29.2 StartZ=0 EndX=-188.505 EndY=27.3206 EndZ=0
  constraints (27):
    c: Coincident(g2,g0)
    c: Parallel(g0,g-3)
    c: Tangent(g1,g0) = -1.5708
    c: Perpendicular(g0,g2)
    c: Tangent(g2,g3)
    c: Distance(g0,g1) = 9
    c: Equal(g0,g1)
    c: Distance(g3,g2) = 4
    c: Equal(g2,g3)
    c: Parallel(g3,g4)
    c: Symmetric(g4,g4,g0)
    c: Parallel(g6,g1)
    c: Parallel(g7,g1)
    c: Symmetric(g6,g6,g2)
    c: Symmetric(g5,g5,g1)
    c: Symmetric(g7,g7,g3)
    c: Coincident(g7,g4)
    c: Coincident(g6,g4)
    c: Coincident(g5,g6)
    c: Symmetric(g-3,g-3,g8)
    c: Perpendicular(g-3,g9)
    c: Distance(g9) = 8
    c: Coincident(g3,g9)
    c: Coincident(g10,g8)
    c: Parallel(g10,g-3)
    c: Distance(g10) = 2
    c: Coincident(g10,g9)
FEATURE [Sketcher::SketchObject] Sketch056  label="buco esterno per micro switch"
  ArcFitTolerance = 1e-06
  AttachmentSupport = -> [XZ_Plane]
  ExternalGeometry = -> [Sketch055]
  FullyConstrained = true
  MakeInternals = false
  MapMode = 5
  Placement = pos=(0,0,0) rot=(1,0,0;1.5708rad)
  sketch-geometry (17):
    g0: GeomPoint [constr] X=-194.143 Y=29.3727 Z=0
    g1: GeomPoint [constr] X=-194.483 Y=34.2854 Z=0
    g2: GeomPoint [constr] X=-197.902 Y=30.7408 Z=0
    g3: GeomPoint [constr] X=-197.561 Y=25.8282 Z=0
    g4: GeomPoint [constr] X=-196.022 Y=30.0568 Z=0
    g5: LineSegment [constr] StartX=-194.483 StartY=34.2854 StartZ=0 EndX=-196.022 EndY=30.0568 EndZ=0
    g6: LineSegment [constr] StartX=-196.022 StartY=30.0568 StartZ=0 EndX=-197.561 EndY=25.8282 EndZ=0
    g7: LineSegment [constr] StartX=-197.902 StartY=30.7408 StartZ=0 EndX=-196.022 EndY=30.0568 EndZ=0
    g8: LineSegment [constr] StartX=-196.022 StartY=30.0568 StartZ=0 EndX=-194.143 EndY=29.3727 EndZ=0
    g9: LineSegment [constr] StartX=-195.338 StartY=31.9362 StartZ=0 EndX=-196.022 EndY=30.0568 EndZ=0
    g10: LineSegment [constr] StartX=-196.022 StartY=30.0568 StartZ=0 EndX=-196.706 EndY=28.1774 EndZ=0
    g11: LineSegment [constr] StartX=-196.022 StartY=30.0568 StartZ=0 EndX=-196.821 EndY=30.3475 EndZ=0
    g12: LineSegment [constr] StartX=-196.022 StartY=30.0568 StartZ=0 EndX=-195.223 EndY=29.7661 EndZ=0
    g13: LineSegment StartX=-194.539 StartY=31.6454 StartZ=0 EndX=-195.907 EndY=27.8867 EndZ=0
    g14: LineSegment StartX=-196.137 StartY=32.2269 StartZ=0 EndX=-197.505 EndY=28.4681 EndZ=0
    g15: LineSegment StartX=-196.137 StartY=32.2269 StartZ=0 EndX=-194.539 EndY=31.6454 EndZ=0
    g16: LineSegment StartX=-197.505 StartY=28.4681 StartZ=0 EndX=-195.907 EndY=27.8867 EndZ=0
  constraints (34):
    c: Symmetric(g-5,g-5,g1)
    c: Symmetric(g-5,g-6,g0)
    c: Symmetric(g-6,g-6,g3)
    c: Symmetric(g-5,g-6,g2)
    c: Coincident(g5,g1)
    c: Coincident(g5,g4)
    c: Coincident(g6,g4)
    c: Coincident(g6,g3)
    c: Equal(g5,g6)
    c: Coincident(g7,g2)
    c: Coincident(g7,g4)
    c: Coincident(g8,g4)
    c: Coincident(g8,g0)
    c: Equal(g7,g8)
    c: Coincident(g11,g9)
    c: Coincident(g12,g9)
    c: Tangent(g10,g9) = -1.5708
    c: Perpendicular(g11,g9)
    c: Parallel(g9,g-4)
    c: Equal(g9,g10)
    c: Parallel(g12,g11)
    c: Equal(g11,g12)
    c: Distance(g11,g12) = 1.7
    c: Distance(g9,g10) = 4
    c: Symmetric(g13,g13,g12)
    c: Parallel(g13,g9)
    c: Symmetric(g14,g14,g11)
    c: Symmetric(g15,g15,g9)
    c: Parallel(g15,g11)
    c: Symmetric(g16,g16,g10)
    c: Coincident(g16,g14)
    c: Coincident(g15,g14)
    c: Coincident(g13,g15)
    c: Coincident(g9,g4)
FEATURE [Sketcher::SketchObject] Sketch057  label="buco interno per SWITCH"
  ArcFitTolerance = 1e-06
  AttachmentSupport = -> [XZ_Plane]
  ExternalGeometry = -> [Sketch]
  FullyConstrained = true
  MakeInternals = false
  MapMode = 5
  Placement = pos=(0,0,0) rot=(1,0,0;1.5708rad)
  sketch-geometry (10):
    g0: GeomPoint [constr] X=-187.821 Y=29.2 Z=0
    g1: LineSegment [constr] StartX=-188.505 StartY=27.3206 StartZ=0 EndX=-193.203 EndY=29.0307 EndZ=0
    g2: LineSegment [constr] StartX=-190.809 StartY=35.6086 StartZ=0 EndX=-195.597 EndY=22.4529 EndZ=0
    g3: GeomPoint [constr] X=-193.203 Y=29.0307 Z=0
    g4: LineSegment [constr] StartX=-196.492 StartY=30.2278 StartZ=0 EndX=-189.914 EndY=27.8336 EndZ=0
    g5: LineSegment StartX=-194.098 StartY=36.8056 StartZ=0 EndX=-187.52 EndY=34.4115 EndZ=0
    g6: LineSegment StartX=-194.098 StartY=36.8056 StartZ=0 EndX=-198.886 EndY=23.6499 EndZ=0
    g7: LineSegment StartX=-187.52 StartY=34.4115 StartZ=0 EndX=-192.308 EndY=21.2558 EndZ=0
    g8: LineSegment StartX=-198.886 StartY=23.6499 StartZ=0 EndX=-192.308 EndY=21.2558 EndZ=0
    g9: LineSegment [constr] StartX=-187.821 StartY=29.2 StartZ=0 EndX=-188.505 EndY=27.3206 EndZ=0
  constraints (23):
    c: Symmetric(g-3,g-3,g0)
    c: Perpendicular(g1,g-3)
    c: Parallel(g2,g-3)
    c: Symmetric(g2,g2,g3)
    c: Perpendicular(g2,g4)
    c: Symmetric(g4,g4,g3)
    c: Distance(g2) = 14
    c: Distance(g4) = 7
    c: Distance(g1) = 5
    c: Parallel(g5,g4)
    c: Parallel(g7,g2)
    c: Symmetric(g5,g5,g2)
    c: Symmetric(g6,g6,g4)
    c: Symmetric(g7,g7,g4)
    c: Symmetric(g8,g8,g2)
    c: Coincident(g6,g5)
    c: Coincident(g7,g5)
    c: Coincident(g8,g7)
    c: Coincident(g3,g1)
    c: Coincident(g9,g0)
    c: Parallel(g9,g-3)
    c: Distance(g9) = 2
    c: Coincident(g1,g9)
FEATURE [Sketcher::SketchObject] Sketch058  label="buco esterno per SWITCH"
  ArcFitTolerance = 1e-06
  AttachmentSupport = -> [XZ_Plane]
  ExternalGeometry = -> [Sketch057]
  FullyConstrained = true
  MakeInternals = false
  MapMode = 5
  Placement = pos=(0,0,0) rot=(1,0,0;1.5708rad)
  sketch-geometry (12):
    g0: GeomPoint [constr] X=-190.809 Y=35.6086 Z=0
    g1: GeomPoint [constr] X=-196.492 Y=30.2278 Z=0
    g2: GeomPoint [constr] X=-189.914 Y=27.8336 Z=0
    g3: GeomPoint [constr] X=-195.597 Y=22.4529 Z=0
    g4: GeomPoint [constr] X=-193.203 Y=29.0307 Z=0
    g5: LineSegment [constr] StartX=-192.006 StartY=32.3196 StartZ=0 EndX=-194.4 EndY=25.7418 EndZ=0
    g6: GeomPoint [constr] X=-193.203 Y=29.0307 Z=0
    g7: LineSegment [constr] StartX=-195.082 StartY=29.7148 StartZ=0 EndX=-191.324 EndY=28.3467 EndZ=0
    g8: LineSegment StartX=-193.885 StartY=33.0037 StartZ=0 EndX=-190.127 EndY=31.6356 EndZ=0
    g9: LineSegment StartX=-190.127 StartY=31.6356 StartZ=0 EndX=-192.521 EndY=25.0578 EndZ=0
    g10: LineSegment StartX=-196.28 StartY=26.4258 StartZ=0 EndX=-192.521 EndY=25.0578 EndZ=0
    g11: LineSegment StartX=-193.885 StartY=33.0037 StartZ=0 EndX=-196.28 EndY=26.4258 EndZ=0
  constraints (21):
    c: Symmetric(g-6,g-6,g3)
    c: Symmetric(g-4,g-6,g2)
    c: Symmetric(g-5,g-4,g0)
    c: Symmetric(g-5,g-6,g1)
    c: Symmetric(g1,g2,g4)
    c: Parallel(g5,g-4)
    c: Symmetric(g5,g5,g6)
    c: Perpendicular(g7,g5)
    c: Symmetric(g7,g7,g6)
    c: Distance(g5) = 7
    c: Distance(g7) = 4
    c: Parallel(g8,g7)
    c: Parallel(g11,g5)
    c: Symmetric(g8,g8,g5)
    c: Symmetric(g9,g9,g7)
    c: Symmetric(g10,g10,g5)
    c: Symmetric(g11,g11,g7)
    c: Coincident(g11,g8)
    c: Coincident(g9,g8)
    c: Coincident(g9,g10)
    c: Coincident(g6,g4)
FEATURE [Part::Extrusion] Extrude060  label="Extrude buco interno per SWITCH destro"
  Base = -> Sketch057
  Dir = (0,-1,2e-16)
  DirMode = 2
  FaceMakerClass = Part::FaceMakerBullseye
  FaceMakerMode = 3
  LengthFwd = 13.2
  LengthRev = 0
  Placement = pos=(0,2.6,0) rot=(0,0,1;0rad)
  Solid = true
  Symmetric = false
FEATURE [Part::Extrusion] Extrude061  label="Extrude buco esterno per SWITCH destro"
  Base = -> Sketch058
  Dir = (0,-1,2e-16)
  DirMode = 2
  FaceMakerClass = Part::FaceMakerBullseye
  FaceMakerMode = 3
  LengthFwd = 2
  LengthRev = 0
  Placement = pos=(0,-10.6,0) rot=(0,0,1;0rad)
  Solid = true
  Symmetric = false
FEATURE [Sketcher::SketchObject] Sketch059  label="buco per spazio introduzione SWITCH"
  ArcFitTolerance = 1e-06
  AttachmentSupport = -> [XZ_Plane]
  ExternalGeometry = -> [Sketch057,Sketch010]
  FullyConstrained = true
  MakeInternals = false
  MapMode = 5
  Placement = pos=(0,0,0) rot=(1,0,0;1.5708rad)
  sketch-geometry (8):
    g0: LineSegment [constr] StartX=-201.368 StartY=36.3521 StartZ=0 EndX=-195.094 EndY=34.0687 EndZ=0
    g1: LineSegment [constr] StartX=-194.098 StartY=36.8056 StartZ=0 EndX=-195.094 EndY=34.0687 EndZ=0
    g2: LineSegment StartX=-198.658 StartY=24.2771 StartZ=0 EndX=-199.654 EndY=21.5401 EndZ=0
    g3: LineSegment StartX=-199.654 StartY=21.5401 StartZ=0 EndX=-181.196 EndY=14.822 EndZ=0
    g4: LineSegment StartX=-181.196 StartY=14.822 StartZ=0 EndX=-180.2 EndY=17.559 EndZ=0
    g5: LineSegment StartX=-180.2 StartY=17.559 StartZ=0 EndX=-198.658 EndY=24.2771 EndZ=0
    g6: LineSegment [constr] StartX=-204.932 StartY=26.5605 StartZ=0 EndX=-198.658 EndY=24.2771 EndZ=0
    g7: LineSegment [constr] StartX=-198.658 StartY=24.2771 StartZ=0 EndX=-199.654 EndY=21.5401 EndZ=0
  constraints (20):
    c: Parallel(g1,g-3)
    c: Parallel(g0,g-4)
    c: Coincident(g0,g-4)
    c: Coincident(g1,g-3)
    c: Coincident(g0,g1)
    c: Coincident(g3,g2)
    c: Coincident(g4,g3)
    c: Coincident(g5,g4)
    c: Coincident(g5,g2)
    c: Parallel(g5,g-5)
    c: Parallel(g3,g-5)
    c: Parallel(g4,g-6)
    c: DistanceX(g-6,g4) = 0
    c: Coincident(g6,g-5)
    c: Equal(g6,g0)
    c: Coincident(g7,g6)
    c: Equal(g7,g1)
    c: Tangent(g7,g-3)
    c: Coincident(g2,g6)
    c: Coincident(g2,g7)
FEATURE [Part::Extrusion] Extrude062  label="Extrude buco per spazio introduzione SWITCH"
  Base = -> Sketch059
  Dir = (0,-1,2e-16)
  DirMode = 2
  FaceMakerClass = Part::FaceMakerBullseye
  FaceMakerMode = 3
  LengthFwd = 13.2
  LengthRev = 0
  Solid = true
  Symmetric = true
FEATURE [Part::Extrusion] Extrude063  label="Extrude buco interno per SWITCH sinistro"
  Base = -> Sketch057
  Dir = (0,-1,2e-16)
  DirMode = 2
  FaceMakerClass = Part::FaceMakerBullseye
  FaceMakerMode = 3
  LengthFwd = 13.2
  LengthRev = 0
  Placement = pos=(0,10.6,0) rot=(0,0,1;0rad)
  Solid = true
  Symmetric = false
FEATURE [Part::Extrusion] Extrude064  label="Extrude buco esterno per SWITCH sinistro"
  Base = -> Sketch058
  Dir = (0,-1,2e-16)
  DirMode = 2
  FaceMakerClass = Part::FaceMakerBullseye
  FaceMakerMode = 3
  LengthFwd = 2
  LengthRev = 0
  Placement = pos=(0,12.6,0) rot=(0,0,1;0rad)
  Solid = true
  Symmetric = false
FEATURE [Sketcher::SketchObject] Sketch061  label="struttura esterna blocco switch"
  ArcFitTolerance = 1e-06
  AttachmentSupport = -> [XZ_Plane003]
  FullyConstrained = true
  MakeInternals = false
  MapMode = 5
  Placement = pos=(0,0,0) rot=(1,0,0;1.5708rad)
  sketch-geometry (5):
    g0: LineSegment StartX=-1 StartY=-5.1 StartZ=0 EndX=1 EndY=-5.1 EndZ=0
    g1: LineSegment StartX=1 StartY=-5.1 StartZ=0 EndX=1 EndY=5.1 EndZ=0
    g2: LineSegment StartX=1 StartY=5.1 StartZ=0 EndX=-1 EndY=5.1 EndZ=0
    g3: LineSegment StartX=-1 StartY=5.1 StartZ=0 EndX=-1 EndY=-5.1 EndZ=0
    g4: GeomPoint [constr] X=0 Y=0 Z=0
  constraints (12):
    c: Coincident(g0,g1)
    c: Coincident(g1,g2)
    c: Coincident(g2,g3)
    c: Coincident(g3,g0)
    c: Horizontal(g0)
    c: Horizontal(g2)
    c: Vertical(g1)
    c: Vertical(g3)
    c: Symmetric(g2,g0,g4)
    c: Distance(g1,g3) = 2
    c: Distance(g0,g2) = 10.2
    c: Coincident(g4,g-1)
FEATURE [Sketcher::SketchObject] Sketch062  label="struttura interna blocco switch"
  ArcFitTolerance = 1e-06
  AttachmentSupport = -> [XZ_Plane003]
  ExternalGeometry = -> [Sketch061]
  FullyConstrained = true
  MakeInternals = false
  MapMode = 5
  Placement = pos=(0,0,0) rot=(1,0,0;1.5708rad)
  sketch-geometry (5):
    g0: LineSegment StartX=-1 StartY=3.1 StartZ=0 EndX=-1 EndY=-3.1 EndZ=0
    g1: LineSegment StartX=-1 StartY=-3.1 StartZ=0 EndX=1 EndY=-3.1 EndZ=0
    g2: LineSegment StartX=1 StartY=-3.1 StartZ=0 EndX=1 EndY=3.1 EndZ=0
    g3: LineSegment StartX=1 StartY=3.1 StartZ=0 EndX=-1 EndY=3.1 EndZ=0
    g4: GeomPoint [constr] X=0 Y=0 Z=0
  constraints (12):
    c: Coincident(g0,g1)
    c: Coincident(g1,g2)
    c: Coincident(g2,g3)
    c: Coincident(g3,g0)
    c: Vertical(g0)
    c: Vertical(g2)
    c: Horizontal(g1)
    c: Horizontal(g3)
    c: Symmetric(g2,g0,g4)
    c: Coincident(g4,g-1)
    c: Distance(g0) = 6.2
    c: Equal(g3,g-3)
FEATURE [Sketcher::SketchObject] Sketch063  label="blocchi tra switch"
  ArcFitTolerance = 1e-06
  AttachmentSupport = -> [XZ_Plane003]
  ExternalGeometry = -> [Sketch061,Sketch062]
  FullyConstrained = true
  MakeInternals = false
  MapMode = 5
  Placement = pos=(0,0,0) rot=(1,0,0;1.5708rad)
  sketch-geometry (8):
    g0: LineSegment StartX=-3 StartY=5.1 StartZ=0 EndX=-1 EndY=5.1 EndZ=0
    g1: LineSegment StartX=-1 StartY=5.1 StartZ=0 EndX=-1 EndY=3.1 EndZ=0
    g2: LineSegment StartX=-1 StartY=3.1 StartZ=0 EndX=-3 EndY=3.1 EndZ=0
    g3: LineSegment StartX=-3 StartY=3.1 StartZ=0 EndX=-3 EndY=5.1 EndZ=0
    g4: LineSegment StartX=-3 StartY=-3.1 StartZ=0 EndX=-1 EndY=-3.1 EndZ=0
    g5: LineSegment StartX=-1 StartY=-3.1 StartZ=0 EndX=-1 EndY=-5.1 EndZ=0
    g6: LineSegment StartX=-1 StartY=-5.1 StartZ=0 EndX=-3 EndY=-5.1 EndZ=0
    g7: LineSegment StartX=-3 StartY=-5.1 StartZ=0 EndX=-3 EndY=-3.1 EndZ=0
  constraints (20):
    c: Horizontal(g0)
    c: Coincident(g1,g0)
    c: Coincident(g2,g1)
    c: Horizontal(g2)
    c: Coincident(g3,g2)
    c: Coincident(g3,g0)
    c: Vertical(g3)
    c: Horizontal(g4)
    c: Coincident(g5,g4)
    c: Coincident(g6,g5)
    c: Horizontal(g6)
    c: Coincident(g7,g6)
    c: Coincident(g7,g4)
    c: Vertical(g7)
    c: Coincident(g0,g-4)
    c: Coincident(g1,g-5)
    c: Coincident(g4,g-6)
    c: Coincident(g5,g-7)
    c: Distance(g0) = 2
    c: Distance(g4) = 2
FEATURE [Sketcher::SketchObject] Sketch066  label="piano per rampino"
  ArcFitTolerance = 1e-06
  AttachmentSupport = -> [XZ_Plane002]
  ExternalGeometry = -> [Sketch045]
  FullyConstrained = true
  MakeInternals = false
  MapMode = 5
  Placement = pos=(0,0,0) rot=(1,0,0;1.5708rad)
  sketch-geometry (4):
    g0: LineSegment StartX=5.4 StartY=5.1 StartZ=0 EndX=5.4 EndY=3.9 EndZ=0
    g1: LineSegment StartX=5.4 StartY=3.9 StartZ=0 EndX=7 EndY=3.9 EndZ=0
    g2: LineSegment StartX=7 StartY=3.9 StartZ=0 EndX=7 EndY=5.1 EndZ=0
    g3: LineSegment StartX=7 StartY=5.1 StartZ=0 EndX=5.4 EndY=5.1 EndZ=0
  constraints (11):
    c: Coincident(g0,g1)
    c: Coincident(g1,g2)
    c: Coincident(g2,g3)
    c: Coincident(g3,g0)
    c: Vertical(g0)
    c: Vertical(g2)
    c: Horizontal(g1)
    c: Horizontal(g3)
    c: Distance(g0,g2) = 1.6
    c: Distance(g1,g3) = 1.2
    c: Coincident(g2,g-3)
FEATURE [Sketcher::SketchObject] Sketch064  label="rampini_per_serraggio_struttura"
  ArcFitTolerance = 1e-06
  AttachmentSupport = -> [XZ_Plane002]
  ExternalGeometry = -> [Sketch066,Sketch045]
  FullyConstrained = true
  MakeInternals = false
  MapMode = 5
  Placement = pos=(0,0,0) rot=(1,0,0;1.5708rad)
  sketch-geometry (7):
    g0: LineSegment StartX=7 StartY=5.1 StartZ=0 EndX=7 EndY=3.9 EndZ=0
    g1: LineSegment StartX=7 StartY=3.9 StartZ=0 EndX=9 EndY=3.9 EndZ=0
    g2: LineSegment StartX=7 StartY=5.1 StartZ=0 EndX=7 EndY=5.1 EndZ=0
    g3: LineSegment StartX=7 StartY=5.1 StartZ=0 EndX=7 EndY=7.5 EndZ=0
    g4: LineSegment StartX=9 StartY=5.1 StartZ=0 EndX=9 EndY=3.9 EndZ=0
    g5: LineSegment StartX=7 StartY=7.5 StartZ=0 EndX=9 EndY=7.5 EndZ=0
    g6: LineSegment StartX=9 StartY=7.5 StartZ=0 EndX=9 EndY=5.1 EndZ=0
  constraints (20):
    c: Vertical(g0)
    c: Coincident(g1,g0)
    c: Horizontal(g1)
    c: Coincident(g2,g0)
    c: Horizontal(g2)
    c: Coincident(g3,g2)
    c: Vertical(g3)
    c: Coincident(g5,g3)
    c: Coincident(g4,g6)
    c: Coincident(g4,g1)
    c: Vertical(g4)
    c: Coincident(g0,g-3)
    c: DistanceY(g-4,g3) = 2.4
    c: DistanceX(g1,g1) = 2
    c: DistanceY(g2,g6) = 0
    c: DistanceX(g2,g2) = 0
    c: DistanceY(g0,g0) = 1.2
    c: Coincident(g5,g6)
    c: Horizontal(g5)
    c: Vertical(g6)
FEATURE [Sketcher::SketchObject] Sketch067  label="perno per blocco switch"
  ArcFitTolerance = 1e-06
  AttachmentSupport = -> [XZ_Plane]
  ExternalGeometry = -> [Sketch,Sketch010]
  FullyConstrained = true
  MakeInternals = false
  MapMode = 5
  Placement = pos=(0,0,0) rot=(1,0,0;1.5708rad)
  sketch-geometry (14):
    g0: LineSegment StartX=-191.073 StartY=24.9429 StartZ=0 EndX=-185.81 EndY=23.0276 EndZ=0
    g1: LineSegment StartX=-183.76 StartY=23.9839 StartZ=0 EndX=-182.392 EndY=27.7427 EndZ=0
    g2: LineSegment StartX=-183.348 StartY=29.7934 StartZ=0 EndX=-188.61 EndY=31.7087 EndZ=0
    g3: LineSegment StartX=-188.61 StartY=31.7087 StartZ=0 EndX=-191.073 EndY=24.9429 EndZ=0
    g4: GeomPoint [constr] X=-186.459 Y=27.0946 Z=0
    g5: LineSegment StartX=-189.022 StartY=25.8992 StartZ=0 EndX=-185.263 EndY=24.5311 EndZ=0
    g6: LineSegment StartX=-185.263 StartY=24.5311 StartZ=0 EndX=-183.895 EndY=28.2899 EndZ=0
    g7: LineSegment StartX=-183.895 StartY=28.2899 StartZ=0 EndX=-187.654 EndY=29.658 EndZ=0
    g8: LineSegment StartX=-187.654 StartY=29.658 StartZ=0 EndX=-189.022 EndY=25.8992 EndZ=0
    g9: GeomPoint [constr] X=-186.459 Y=27.0946 Z=0
    g10: ArcOfCircle CenterX=-185.263 CenterY=24.5311 CenterZ=0 NormalX=0 NormalY=0 NormalZ=1 AngleXU=0 Radius=1.6 StartAngle=4.36332 EndAngle=5.93412
    g11: GeomPoint [constr] X=-184.307 Y=22.4804 Z=0
    g12: ArcOfCircle CenterX=-183.895 CenterY=28.2899 CenterZ=0 NormalX=0 NormalY=0 NormalZ=1 AngleXU=0 Radius=1.6 StartAngle=5.93412 EndAngle=7.50492
    g13: GeomPoint [constr] X=-181.844 Y=29.2462 Z=0
  constraints (30):
    c: Coincident(g2,g3)
    c: Coincident(g3,g0)
    c: Symmetric(g13,g0,g4)
    c: Distance(g11,g3) = 7.2
    c: Distance(g0,g2) = 7.2
    c: Parallel(g3,g1)
    c: Parallel(g2,g0)
    c: Perpendicular(g2,g3)
    c: Coincident(g5,g6)
    c: Coincident(g6,g7)
    c: Coincident(g7,g8)
    c: Coincident(g8,g5)
    c: Symmetric(g7,g5,g9)
    c: Distance(g6,g8) = 4
    c: Distance(g5,g7) = 4
    c: Coincident(g9,g4)
    c: Parallel(g8,g6)
    c: Parallel(g7,g5)
    c: Perpendicular(g7,g8)
    c: Tangent(g8,g-3)
    c: Tangent(g2,g-4)
    c: PointOnObject(g11,g1)
    c: PointOnObject(g11,g0)
    c: Tangent(g1,g10) = -1.5708
    c: Tangent(g0,g10) = -1.5708
    c: PointOnObject(g13,g1)
    c: Tangent(g1,g12) = -1.5708
    c: Tangent(g2,g12) = -1.5708
    c: Equal(g10,g12)
    c: Coincident(g10,g5)
FEATURE [Part::Extrusion] Extrude072  label="Extrude perno per blocco switch"
  Base = -> Sketch067
  Dir = (0,-1,2e-16)
  DirMode = 2
  FaceMakerClass = Part::FaceMakerBullseye
  FaceMakerMode = 3
  LengthFwd = 25.2
  LengthRev = 0
  Solid = true
  Symmetric = true
FEATURE [Part::MultiFuse] Fusion
  Refine = true
  Shapes = -> [Extrude,Sweep,Extrude007,Extrude011,Extrude005,Extrude012,Extrude013,Extrude016,Extrude031,Extrude039,Extrude045,Extrude072]
FEATURE [Part::Cut] Cut
  Base = -> Fusion
  Refine = true
  Tool = -> Extrude001
FEATURE [Part::Cut] Cut001
  Base = -> Cut
  Refine = true
  Tool = -> Extrude004
FEATURE [Part::Cut] Cut002
  Base = -> Cut001
  Refine = true
  Tool = -> Extrude006
FEATURE [Part::Cut] Cut003
  Base = -> Cut002
  Refine = true
  Tool = -> Extrude008
FEATURE [Part::Cut] Cut004
  Base = -> Cut003
  Refine = true
  Tool = -> Extrude009
FEATURE [Part::Cut] Cut005
  Base = -> Cut004
  Refine = true
  Tool = -> Extrude010
FEATURE [Part::Cut] Cut006
  Base = -> Cut005
  Refine = true
  Tool = -> Extrude014
FEATURE [Part::Cut] Cut007
  Base = -> Cut006
  Refine = true
  Tool = -> Extrude015
FEATURE [Part::Cut] Cut008
  Base = -> Cut007
  Refine = true
  Tool = -> Extrude018
FEATURE [Part::Cut] Cut009
  Base = -> Cut008
  Refine = true
  Tool = -> Extrude019
FEATURE [Part::Cut] Cut010
  Base = -> Cut009
  Refine = true
  Tool = -> Extrude020
FEATURE [Part::Cut] Cut011
  Base = -> Cut010
  Refine = true
  Tool = -> Extrude021
FEATURE [Part::Cut] Cut012
  Base = -> Cut011
  Refine = true
  Tool = -> Extrude022
FEATURE [Part::Cut] Cut013
  Base = -> Cut012
  Refine = true
  Tool = -> Extrude023
FEATURE [Part::Cut] Cut014
  Base = -> Cut013
  Refine = true
  Tool = -> Extrude032
FEATURE [Part::Cut] Cut015
  Base = -> Cut014
  Refine = true
  Tool = -> Extrude033
FEATURE [Part::Cut] Cut016
  Base = -> Cut015
  Refine = true
  Tool = -> Extrude034
FEATURE [Part::Cut] Cut017
  Base = -> Cut016
  Refine = true
  Tool = -> Extrude035
FEATURE [Part::Cut] Cut018
  Base = -> Cut017
  Refine = true
  Tool = -> Extrude036
FEATURE [Part::Cut] Cut019
  Base = -> Cut018
  Refine = true
  Tool = -> Extrude037
FEATURE [Part::Cut] Cut020
  Base = -> Cut019
  Refine = true
  Tool = -> Extrude030
FEATURE [Part::Cut] Cut022
  Base = -> Cut020
  Refine = true
  Tool = -> Extrude038
FEATURE [Part::Cut] Cut023
  Base = -> Cut022
  Refine = true
  Tool = -> Extrude041
FEATURE [Part::Cut] Cut024
  Base = -> Cut023
  Refine = true
  Tool = -> Extrude040
FEATURE [Part::Cut] Cut025
  Base = -> Cut024
  Refine = true
  Tool = -> Extrude042
FEATURE [Part::Cut] Cut026
  Base = -> Cut025
  Refine = true
  Tool = -> Extrude043
FEATURE [Part::Cut] Cut027
  Base = -> Cut026
  Refine = true
  Tool = -> Extrude044
FEATURE [Part::Cut] Cut028
  Base = -> Cut027
  Refine = true
  Tool = -> Extrude046
FEATURE [Part::Cut] Cut029
  Base = -> Cut028
  Refine = true
  Tool = -> Extrude047
FEATURE [Part::Cut] Cut033
  Base = -> Cut029
  Refine = true
  Tool = -> Extrude055
FEATURE [Part::Cut] Cut034
  Base = -> Cut033
  Refine = true
  Tool = -> Extrude056
FEATURE [Part::Cut] Cut035
  Base = -> Cut034
  Refine = true
  Tool = -> Extrude057
FEATURE [Part::Cut] Cut037
  Base = -> Cut035
  Refine = true
  Tool = -> Extrude060
FEATURE [Part::Cut] Cut038
  Base = -> Cut037
  Refine = true
  Tool = -> Extrude061
FEATURE [Part::Cut] Cut039
  Base = -> Cut038
  Refine = true
  Tool = -> Extrude063
FEATURE [Part::Cut] Cut040
  Base = -> Cut039
  Refine = true
  Tool = -> Extrude064
FEATURE [Part::Cut] Cut041
  Base = -> Cut040
  Refine = true
  Tool = -> Extrude062
FEATURE [Sketcher::SketchObject] Sketch068  label="base con smusso sopra neopixel"
  ArcFitTolerance = 1e-06
  AttachmentSupport = -> [YZ_Plane002]
  FullyConstrained = true
  MakeInternals = false
  MapMode = 5
  Placement = pos=(0,0,0) rot=(0.57735,0.57735,0.57735;2.0944rad)
  sketch-geometry (5):
    g0: LineSegment StartX=-9.5 StartY=-6.1 StartZ=0 EndX=9.5 EndY=-6.1 EndZ=0
    g1: LineSegment StartX=9.5 StartY=-6.1 StartZ=0 EndX=9.5 EndY=6.1 EndZ=0
    g2: LineSegment StartX=9.5 StartY=6.1 StartZ=0 EndX=-9.5 EndY=6.1 EndZ=0
    g3: LineSegment StartX=-9.5 StartY=6.1 StartZ=0 EndX=-9.5 EndY=-6.1 EndZ=0
    g4: GeomPoint [constr] X=0 Y=0 Z=0
  constraints (12):
    c: Coincident(g0,g1)
    c: Coincident(g1,g2)
    c: Coincident(g2,g3)
    c: Coincident(g3,g0)
    c: Horizontal(g0)
    c: Horizontal(g2)
    c: Vertical(g1)
    c: Vertical(g3)
    c: Symmetric(g2,g0,g4)
    c: Distance(g1,g3) = 19
    c: Distance(g0,g2) = 12.2
    c: Coincident(g4,g-1)
FEATURE [Sketcher::SketchObject] Sketch069  label="cilindro minore"
  ArcFitTolerance = 1e-06
  AttachmentSupport = -> [XZ_Plane004]
  FullyConstrained = true
  MakeInternals = false
  MapMode = 5
  Placement = pos=(0,0,0) rot=(1,0,0;1.5708rad)
  sketch-geometry (1):
    g0: Circle CenterX=0 CenterY=0 CenterZ=0 NormalX=0 NormalY=0 NormalZ=1 AngleXU=0 Radius=5.8
  constraints (2):
    c: Diameter(g0) = 11.6
    c: Coincident(g0,g-1)
FEATURE [Sketcher::SketchObject] Sketch070  label="cilindro maggiore"
  ArcFitTolerance = 1e-06
  AttachmentSupport = -> [XZ_Plane004]
  ExternalGeometry = -> [Sketch069]
  FullyConstrained = true
  MakeInternals = false
  MapMode = 5
  Placement = pos=(0,0,0) rot=(1,0,0;1.5708rad)
  sketch-geometry (1):
    g0: Circle CenterX=0 CenterY=0 CenterZ=0 NormalX=0 NormalY=0 NormalZ=1 AngleXU=0 Radius=6.5
  constraints (2):
    c: Coincident(g0,g-1)
    c: Diameter(g0) = 13
FEATURE [Sketcher::SketchObject] Sketch071  label="buco interno"
  ArcFitTolerance = 1e-06
  AttachmentSupport = -> [XZ_Plane004]
  ExternalGeometry = -> [Sketch069]
  FullyConstrained = true
  MakeInternals = false
  MapMode = 5
  Placement = pos=(0,0,0) rot=(1,0,0;1.5708rad)
  sketch-geometry (1):
    g0: Circle CenterX=0 CenterY=0 CenterZ=0 NormalX=0 NormalY=0 NormalZ=1 AngleXU=0 Radius=5
  constraints (2):
    c: Coincident(g0,g-1)
    c: Diameter(g0) = 10
FEATURE [PartDesign::Pad] Pad
  Direction = (0,-1,2e-16)
  Length = 1.2
  Length2 = 10
  Placement = pos=(0,0,0) rot=(1,0,0;1.5708rad)
  Profile = -> Sketch070
  ReferenceAxis = -> Sketch070 [N_Axis]
  Refine = true
  Suppressed = false
  Type = 0
FEATURE [PartDesign::Pad] Pad001
  BaseFeature = -> Pad
  Direction = (0,-1,2e-16)
  Length = 5.6
  Length2 = 10
  Placement = pos=(0,0,0) rot=(1,0,0;1.5708rad)
  Profile = -> Sketch069
  ReferenceAxis = -> Sketch069 [N_Axis]
  Refine = true
  Suppressed = false
  Type = 0
FEATURE [PartDesign::Pocket] Pocket
  BaseFeature = -> Pad001
  Direction = (0,1,-2e-16)
  Length = 7
  Length2 = 5
  Midplane = true
  Placement = pos=(0,0,0) rot=(1,0,0;1.5708rad)
  Profile = -> Sketch071
  ReferenceAxis = -> Sketch071 [N_Axis]
  Refine = true
  Suppressed = false
  Type = 0
FEATURE [PartDesign::Fillet] Fillet
  Base = -> Pocket [Face7]
  BaseFeature = -> Pocket
  Placement = pos=(0,0,0) rot=(1,0,0;1.5708rad)
  Radius = 1
  Refine = true
  SupportTransform = false
  Suppressed = false
  UseAllEdges = false
FEATURE [PartDesign::Body] Body004  label="pulsanti lato sinistro"
  AllowCompound = false
  Group = -> [Sketch069,Sketch070,Sketch071,Pad,Pad001,Pocket,Fillet]
  Origin = -> Origin004
  Tip = -> Fillet
FEATURE [Sketcher::SketchObject] Sketch072  label="buco per saldature e diodo driver solenoide"
  ArcFitTolerance = 1e-06
  AttachmentSupport = -> [XZ_Plane]
  ExternalGeometry = -> [Sketch038]
  FullyConstrained = true
  MakeInternals = false
  MapMode = 5
  Placement = pos=(0,0,0) rot=(1,0,0;1.5708rad)
  sketch-geometry (4):
    g0: LineSegment StartX=-212.269 StartY=-43.9083 StartZ=0 EndX=-207.197 EndY=-33.0326 EndZ=0
    g1: LineSegment StartX=-207.197 StartY=-33.0326 StartZ=0 EndX=-207.56 EndY=-32.8635 EndZ=0
    g2: LineSegment StartX=-207.56 StartY=-32.8635 StartZ=0 EndX=-212.631 EndY=-43.7392 EndZ=0
    g3: LineSegment StartX=-212.631 StartY=-43.7392 StartZ=0 EndX=-212.269 EndY=-43.9083 EndZ=0
  constraints (11):
    c: Coincident(g1,g0)
    c: Coincident(g2,g1)
    c: Coincident(g3,g2)
    c: Coincident(g3,g0)
    c: Parallel(g-3,g0)
    c: Parallel(g0,g2)
    c: Perpendicular(g0,g3)
    c: Perpendicular(g1,g0)
    c: Distance(g3) = 0.4
    c: Distance(g2) = 12
    c: Coincident(g0,g-3)
FEATURE [Part::Extrusion] Extrude074  label="Extrude buco per saldature e diodo driver solenoide"
  Base = -> Sketch072
  Dir = (0,-1,2e-16)
  DirMode = 2
  FaceMakerClass = Part::FaceMakerBullseye
  FaceMakerMode = 3
  LengthFwd = 14.6
  LengthRev = 0
  Solid = true
  Symmetric = true
FEATURE [Part::Cut] Cut042
  Base = -> Cut041
  Refine = true
  Tool = -> Extrude074
FEATURE [Sketcher::SketchObject] Sketch073  label="fori slargati blocco solenoide"
  ArcFitTolerance = 1e-06
  AttachmentSupport = -> [XY_Plane]
  ExternalGeometry = -> [Sketch030]
  FullyConstrained = true
  MakeInternals = false
  MapMode = 5
  sketch-geometry (2):
    g0: Circle CenterX=-152.209 CenterY=6.95 CenterZ=0 NormalX=0 NormalY=0 NormalZ=1 AngleXU=0 Radius=3.7
    g1: Circle CenterX=-130.41 CenterY=-6.95 CenterZ=0 NormalX=0 NormalY=0 NormalZ=1 AngleXU=0 Radius=3.7
  constraints (4):
    c: Diameter(g0) = 7.4
    c: Coincident(g0,g-3)
    c: Diameter(g1) = 7.4
    c: Coincident(g1,g-4)
FEATURE [Part::Extrusion] Extrude075  label="Extrude fori slargati blocco solenoide"
  Base = -> Sketch073
  Dir = (0,0,1)
  DirMode = 2
  FaceMakerClass = Part::FaceMakerBullseye
  FaceMakerMode = 3
  LengthFwd = 1.5
  LengthRev = 0
  Placement = pos=(0,0,36.4) rot=(0,0,1;0rad)
  Solid = true
  Symmetric = false
FEATURE [Part::Cut] Cut043
  Base = -> Cut042
  Refine = true
  Tool = -> Extrude075
FEATURE [Sketcher::SketchObject] Sketch074  label="lato sx pistola"
  ArcFitTolerance = 1e-06
  AttachmentSupport = -> [XZ_Plane]
  ExternalGeometry = -> [Sketch016,Sketch,Sketch058]
  FullyConstrained = true
  MakeInternals = false
  MapMode = 5
  Placement = pos=(0,0,0) rot=(1,0,0;1.5708rad)
  sketch-geometry (37):
    g0: LineSegment StartX=-82.8 StartY=3.2 StartZ=0 EndX=0 EndY=3.2 EndZ=0
    g1: LineSegment StartX=-82.8 StartY=3.2 StartZ=0 EndX=-82.8 EndY=6.2 EndZ=0
    g2: LineSegment [constr] StartX=-107.6 StartY=18 StartZ=0 EndX=-107.6 EndY=20 EndZ=0
    g3: LineSegment [constr] StartX=-132.428 StartY=18 StartZ=0 EndX=-132.428 EndY=20 EndZ=0
    g4: LineSegment StartX=-132.428 StartY=20 StartZ=0 EndX=-107.6 EndY=20 EndZ=0
    g5: ArcOfCircle CenterX=-107.6 CenterY=4 CenterZ=0 NormalX=0 NormalY=0 NormalZ=1 AngleXU=0 Radius=16 StartAngle=0.137937 EndAngle=1.5708
    g6: LineSegment StartX=-82.8 StartY=6.2 StartZ=0 EndX=-91.752 EndY=6.2 EndZ=0
    g7: LineSegment [constr] StartX=-145.743 StartY=8.32624 StartZ=0 EndX=-147.645 EndY=8.94427 EndZ=0
    g8: ArcOfCircle CenterX=-132.428 CenterY=4 CenterZ=0 NormalX=0 NormalY=0 NormalZ=1 AngleXU=0 Radius=16 StartAngle=1.5708 EndAngle=2.82743
    g9: LineSegment StartX=-215.932 StartY=-80.4316 StartZ=0 EndX=-176.685 EndY=-80.4316 EndZ=0
    g10: LineSegment StartX=-147.645 StartY=8.94427 StartZ=0 EndX=-176.685 EndY=-80.4316 EndZ=0
    g11: LineSegment [constr] StartX=-193.988 StartY=-2.33927 StartZ=0 EndX=-192.176 EndY=-3.18451 EndZ=0
    g12: LineSegment [constr] StartX=-217.232 StartY=-52.1862 StartZ=0 EndX=-215.42 EndY=-53.0314 EndZ=0
    g13: LineSegment StartX=-192.176 StartY=-3.18451 StartZ=0 EndX=-215.42 EndY=-53.0314 EndZ=0
    g14: ArcOfCircle CenterX=-184.801 CenterY=-67.3089 CenterZ=0 NormalX=0 NormalY=0 NormalZ=1 AngleXU=0 Radius=33.7833 StartAngle=2.70526 EndAngle=3.54053
    g15: ArcOfCircle CenterX=-207.583 CenterY=4 CenterZ=0 NormalX=0 NormalY=0 NormalZ=1 AngleXU=0 Radius=17 StartAngle=5.84685 EndAngle=7.56663
    g16: LineSegment StartX=-202.765 StartY=20.303 StartZ=0 EndX=-195.887 EndY=39.2 EndZ=0
    g17: LineSegment [constr] StartX=-193.885 StartY=33.0037 StartZ=0 EndX=-197.644 EndY=34.3718 EndZ=0
    g18: LineSegment StartX=-195.887 StartY=39.2 StartZ=0 EndX=0 EndY=39.2 EndZ=0
    g19: LineSegment StartX=0 StartY=3.2 StartZ=0 EndX=0 EndY=39.2 EndZ=0
    g20: LineSegment StartX=-189.939 StartY=31.5672 StartZ=0 EndX=-192.333 EndY=24.9893 EndZ=0
    g21: LineSegment StartX=-196.467 StartY=26.4942 StartZ=0 EndX=-194.073 EndY=33.0721 EndZ=0
    g22: Circle CenterX=-213.443 CenterY=-76.8316 CenterZ=0 NormalX=0 NormalY=0 NormalZ=1 AngleXU=0 Radius=1.8
    g23: Circle CenterX=-179.305 CenterY=-76.8316 CenterZ=0 NormalX=0 NormalY=0 NormalZ=1 AngleXU=0 Radius=1.8
    g24: Circle CenterX=-184.08 CenterY=34.8 CenterZ=0 NormalX=0 NormalY=0 NormalZ=1 AngleXU=0 Radius=1.8
    g25: Circle CenterX=-78.51 CenterY=34.8 CenterZ=0 NormalX=0 NormalY=0 NormalZ=1 AngleXU=0 Radius=1.8
    g26: Circle CenterX=-78.51 CenterY=7.6 CenterZ=0 NormalX=0 NormalY=0 NormalZ=1 AngleXU=0 Radius=1.8
    g27: Circle CenterX=-5.6 CenterY=34.8 CenterZ=0 NormalX=0 NormalY=0 NormalZ=1 AngleXU=0 Radius=1.8
    g28: Circle CenterX=-5.6 CenterY=7.6 CenterZ=0 NormalX=0 NormalY=0 NormalZ=1 AngleXU=0 Radius=1.8
    g29: LineSegment StartX=-190.127 StartY=31.6356 StartZ=0 EndX=-189.939 EndY=31.5672 EndZ=0
    g30: LineSegment StartX=-194.073 StartY=33.0721 StartZ=0 EndX=-193.885 EndY=33.0037 EndZ=0
    g31: LineSegment StartX=-193.885 StartY=33.0037 StartZ=0 EndX=-190.127 EndY=31.6356 EndZ=0
    g32: LineSegment StartX=-196.467 StartY=26.4942 StartZ=0 EndX=-192.333 EndY=24.9893 EndZ=0
    g33: Circle CenterX=-19 CenterY=21.2 CenterZ=0 NormalX=0 NormalY=0 NormalZ=1 AngleXU=0 Radius=6.3
    g34: Circle CenterX=-42 CenterY=21.2 CenterZ=0 NormalX=0 NormalY=0 NormalZ=1 AngleXU=0 Radius=6.3
    g35: Circle CenterX=-65 CenterY=21.2 CenterZ=0 NormalX=0 NormalY=0 NormalZ=1 AngleXU=0 Radius=6.3
    g36: LineSegment [constr] StartX=-4 StartY=21.2 StartZ=0 EndX=-65 EndY=21.2 EndZ=0
  constraints (96):
    c: Coincident(g0,g-41)
    c: Horizontal(g0)
    c: PointOnObject(g0,g-39)
    c: Coincident(g1,g0)
    c: Vertical(g1)
    c: DistanceY(g1,g1) = 3
    c: Coincident(g2,g-17)
    c: Vertical(g2)
    c: Coincident(g3,g-16)
    c: Vertical(g3)
    c: DistanceY(g2,g2) = 2
    c: DistanceY(g3,g3) = 2
    c: Coincident(g4,g3)
    c: Coincident(g4,g2)
    c: Coincident(g5,g-17)
    c: Coincident(g5,g2)
    c: Coincident(g6,g1)
    c: Horizontal(g6)
    c: Coincident(g6,g5)
    c: Coincident(g7,g-15)
    c: Coincident(g8,g7)
    c: Coincident(g8,g3)
    c: Coincident(g8,g-15)
    c: Horizontal(g9)
    c: DistanceY(g-13,g9) = 2
    c: Coincident(g10,g7)
    c: Parallel(g10,g-14)
    c: Coincident(g9,g10)
    c: Distance(g11) = 2
    c: Coincident(g11,g-11)
    c: Perpendicular(g-11,g11)
    c: Distance(g12) = 2
    c: Coincident(g12,g-12)
    c: Perpendicular(g-11,g12)
    c: Coincident(g13,g11)
    c: Coincident(g13,g12)
    c: Coincident(g14,g-32)
    c: Coincident(g14,g12)
    c: Coincident(g14,g9)
    c: Coincident(g15,g-10)
    c: Coincident(g15,g11)
    c: Parallel(g16,g-22)
    c: Distance(g17) = 4
    c: PointOnObject(g17,g16)
    c: Coincident(g15,g16)
    c: Horizontal(g18)
    c: Coincident(g18,g16)
    c: Coincident(g19,g0)
    c: PointOnObject(g19,g-39)
    c: DistanceY(g19,g-36) = 2
    c: Coincident(g18,g19)
    c: Diameter(g22) = 3.6
    c: Coincident(g22,g-9)
    c: Diameter(g23) = 3.6
    c: Coincident(g23,g-8)
    c: Diameter(g24) = 3.6
    c: Diameter(g25) = 3.6
    c: Diameter(g26) = 3.6
    c: Diameter(g27) = 3.6
    c: Diameter(g28) = 3.6
    c: Coincident(g27,g-4)
    c: Coincident(g28,g-3)
    c: Coincident(g25,g-6)
    c: Coincident(g26,g-5)
    c: Coincident(g24,g-7)
    c: Parallel(g20,g-21)
    c: Equal(g20,g-21)
    c: Parallel(g21,g-19)
    c: Equal(g21,g-19)
    c: Distance(g29) = 0.2
    c: Distance(g30) = 0.2
    c: Parallel(g29,g-20)
    c: Parallel(g31,g-20)
    c: Equal(g31,g-20)
    c: Coincident(g30,g31)
    c: Coincident(g31,g29)
    c: Coincident(g29,g-21)
    c: Parallel(g30,g31)
    c: Coincident(g17,g30)
    c: Coincident(g20,g29)
    c: Coincident(g21,g30)
    c: Perpendicular(g16,g17)
    c: Coincident(g32,g21)
    c: Coincident(g32,g20)
    c: Perpendicular(g10,g7)
    c: Diameter(g33) = 12.6
    c: Diameter(g34) = 12.6
    c: Diameter(g35) = 12.6
    c: Horizontal(g36)
    c: PointOnObject(g33,g36)
    c: PointOnObject(g34,g36)
    c: DistanceX(g34,g33) = 23
    c: DistanceX(g35,g34) = 23
    c: DistanceX(g33,g36) = 15
    c: Symmetric(g-24,g-24,g36)
    c: Coincident(g36,g35)
FEATURE [Sketcher::SketchObject] Sketch075  label="lato dx pistola"
  ArcFitTolerance = 1e-06
  AttachmentSupport = -> [XZ_Plane]
  ExternalGeometry = -> [Sketch016,Sketch,Sketch058,Sketch074]
  FullyConstrained = true
  MakeInternals = false
  MapMode = 5
  Placement = pos=(0,0,0) rot=(1,0,0;1.5708rad)
  sketch-geometry (61):
    g0: LineSegment StartX=-82.8 StartY=3.2 StartZ=0 EndX=0 EndY=3.2 EndZ=0
    g1: LineSegment StartX=-82.8 StartY=3.2 StartZ=0 EndX=-82.8 EndY=6.2 EndZ=0
    g2: LineSegment [constr] StartX=-107.6 StartY=18 StartZ=0 EndX=-107.6 EndY=20 EndZ=0
    g3: LineSegment [constr] StartX=-132.428 StartY=18 StartZ=0 EndX=-132.428 EndY=20 EndZ=0
    g4: LineSegment StartX=-132.428 StartY=20 StartZ=0 EndX=-107.6 EndY=20 EndZ=0
    g5: ArcOfCircle CenterX=-107.6 CenterY=4 CenterZ=0 NormalX=0 NormalY=0 NormalZ=1 AngleXU=0 Radius=16 StartAngle=0.137937 EndAngle=1.5708
    g6: LineSegment StartX=-82.8 StartY=6.2 StartZ=0 EndX=-91.752 EndY=6.2 EndZ=0
    g7: LineSegment [constr] StartX=-145.743 StartY=8.32624 StartZ=0 EndX=-147.645 EndY=8.94427 EndZ=0
    g8: ArcOfCircle CenterX=-132.428 CenterY=4 CenterZ=0 NormalX=0 NormalY=0 NormalZ=1 AngleXU=0 Radius=16 StartAngle=1.5708 EndAngle=2.82743
    g9: LineSegment StartX=-215.932 StartY=-80.4316 StartZ=0 EndX=-176.685 EndY=-80.4316 EndZ=0
    g10: LineSegment StartX=-147.645 StartY=8.94427 StartZ=0 EndX=-176.685 EndY=-80.4316 EndZ=0
    g11: LineSegment [constr] StartX=-193.988 StartY=-2.33927 StartZ=0 EndX=-192.176 EndY=-3.18451 EndZ=0
    g12: LineSegment [constr] StartX=-217.232 StartY=-52.1862 StartZ=0 EndX=-215.42 EndY=-53.0314 EndZ=0
    g13: LineSegment StartX=-192.176 StartY=-3.18451 StartZ=0 EndX=-215.42 EndY=-53.0314 EndZ=0
    g14: ArcOfCircle CenterX=-184.801 CenterY=-67.3089 CenterZ=0 NormalX=0 NormalY=0 NormalZ=1 AngleXU=0 Radius=33.7833 StartAngle=2.70526 EndAngle=3.54053
    g15: ArcOfCircle CenterX=-207.583 CenterY=4 CenterZ=0 NormalX=0 NormalY=0 NormalZ=1 AngleXU=0 Radius=17 StartAngle=5.84685 EndAngle=7.56663
    g16: LineSegment StartX=-202.765 StartY=20.303 StartZ=0 EndX=-195.887 EndY=39.2 EndZ=0
    g17: LineSegment [constr] StartX=-193.885 StartY=33.0037 StartZ=0 EndX=-197.644 EndY=34.3718 EndZ=0
    g18: LineSegment StartX=-195.887 StartY=39.2 StartZ=0 EndX=0 EndY=39.2 EndZ=0
    g19: LineSegment StartX=0 StartY=3.2 StartZ=0 EndX=0 EndY=39.2 EndZ=0
    g20: LineSegment StartX=-189.939 StartY=31.5672 StartZ=0 EndX=-192.333 EndY=24.9893 EndZ=0
    g21: LineSegment StartX=-196.467 StartY=26.4942 StartZ=0 EndX=-194.073 EndY=33.0721 EndZ=0
    g22: Circle CenterX=-213.443 CenterY=-76.8316 CenterZ=0 NormalX=0 NormalY=0 NormalZ=1 AngleXU=0 Radius=1.8
    g23: Circle CenterX=-179.305 CenterY=-76.8316 CenterZ=0 NormalX=0 NormalY=0 NormalZ=1 AngleXU=0 Radius=1.8
    g24: Circle CenterX=-184.08 CenterY=34.8 CenterZ=0 NormalX=0 NormalY=0 NormalZ=1 AngleXU=0 Radius=1.8
    g25: Circle CenterX=-78.51 CenterY=34.8 CenterZ=0 NormalX=0 NormalY=0 NormalZ=1 AngleXU=0 Radius=1.8
    g26: Circle CenterX=-78.51 CenterY=7.6 CenterZ=0 NormalX=0 NormalY=0 NormalZ=1 AngleXU=0 Radius=1.8
    g27: Circle CenterX=-5.6 CenterY=34.8 CenterZ=0 NormalX=0 NormalY=0 NormalZ=1 AngleXU=0 Radius=1.8
    g28: Circle CenterX=-5.6 CenterY=7.6 CenterZ=0 NormalX=0 NormalY=0 NormalZ=1 AngleXU=0 Radius=1.8
    g29: LineSegment StartX=-190.127 StartY=31.6356 StartZ=0 EndX=-189.939 EndY=31.5672 EndZ=0
    g30: LineSegment StartX=-194.073 StartY=33.0721 StartZ=0 EndX=-193.885 EndY=33.0037 EndZ=0
    g31: LineSegment StartX=-193.885 StartY=33.0037 StartZ=0 EndX=-190.127 EndY=31.6356 EndZ=0
    g32: LineSegment StartX=-196.467 StartY=26.4942 StartZ=0 EndX=-192.333 EndY=24.9893 EndZ=0
    g33: LineSegment [constr] StartX=-4 StartY=21.2 StartZ=0 EndX=-87.91 EndY=21.2 EndZ=0
    g34: GeomPoint [constr] X=-4 Y=21.2 Z=0
    g35: LineSegment [constr] StartX=-15.2 StartY=33.7 StartZ=0 EndX=-15.2 EndY=8.7 EndZ=0
    g36: LineSegment [constr] StartX=-15.2 StartY=33.7 StartZ=0 EndX=-56.2 EndY=33.7 EndZ=0
    g37: LineSegment [constr] StartX=-15.2 StartY=8.7 StartZ=0 EndX=-56.2 EndY=8.7 EndZ=0
    g38: LineSegment [constr] StartX=-56.2 StartY=33.7 StartZ=0 EndX=-56.2 EndY=8.7 EndZ=0
    g39: Circle CenterX=-18.6 CenterY=30.3 CenterZ=0 NormalX=0 NormalY=0 NormalZ=1 AngleXU=0 Radius=3.4
    g40: Circle CenterX=-18.6 CenterY=12.1 CenterZ=0 NormalX=0 NormalY=0 NormalZ=1 AngleXU=0 Radius=3.4
    g41: Circle CenterX=-43.2 CenterY=30.3 CenterZ=0 NormalX=0 NormalY=0 NormalZ=1 AngleXU=0 Radius=3.4
    g42: Circle CenterX=-43.2 CenterY=12.1 CenterZ=0 NormalX=0 NormalY=0 NormalZ=1 AngleXU=0 Radius=3.4
    g43: LineSegment [constr] StartX=-4 StartY=21.2 StartZ=0 EndX=-15.2 EndY=21.2 EndZ=0
    g44: LineSegment [constr] StartX=-15.2 StartY=21.2 StartZ=0 EndX=-36.2 EndY=21.2 EndZ=0
    g45: LineSegment [constr] StartX=-41.5 StartY=16.2 StartZ=0 EndX=-30.9 EndY=16.2 EndZ=0
    g46: LineSegment [constr] StartX=-30.9 StartY=16.2 StartZ=0 EndX=-30.9 EndY=26.2 EndZ=0
    g47: LineSegment [constr] StartX=-30.9 StartY=26.2 StartZ=0 EndX=-41.5 EndY=26.2 EndZ=0
    g48: LineSegment [constr] StartX=-41.5 StartY=26.2 StartZ=0 EndX=-41.5 EndY=16.2 EndZ=0
    g49: GeomPoint [constr] X=-36.2 Y=21.2 Z=0
    g50: Circle CenterX=-36.2 CenterY=21.2 CenterZ=0 NormalX=0 NormalY=0 NormalZ=1 AngleXU=0 Radius=2.8
    g51: LineSegment [constr] StartX=-24.2 StartY=26.7 StartZ=0 EndX=-24.2 EndY=15.7 EndZ=0
    g52: Circle CenterX=-24.2 CenterY=26.7 CenterZ=0 NormalX=0 NormalY=0 NormalZ=1 AngleXU=0 Radius=3
    g53: Circle CenterX=-24.2 CenterY=15.7 CenterZ=0 NormalX=0 NormalY=0 NormalZ=1 AngleXU=0 Radius=3
    g54: GeomPoint X=-18.6 Y=30.3 Z=0
    g55: GeomPoint X=-18.6 Y=12.1 Z=0
    g56: GeomPoint X=-43.2 Y=12.1 Z=0
    g57: GeomPoint X=-43.2 Y=30.3 Z=0
    g58: Circle CenterX=-65 CenterY=21.2 CenterZ=0 NormalX=0 NormalY=0 NormalZ=1 AngleXU=0 Radius=1.5
    g59: Circle CenterX=-42 CenterY=21.2 CenterZ=0 NormalX=0 NormalY=0 NormalZ=1 AngleXU=0 Radius=1.5
    g60: Circle CenterX=-19 CenterY=21.2 CenterZ=0 NormalX=0 NormalY=0 NormalZ=1 AngleXU=0 Radius=1.5
  constraints (149):
    c: Coincident(g0,g-41)
    c: Horizontal(g0)
    c: PointOnObject(g0,g-39)
    c: Coincident(g1,g0)
    c: Vertical(g1)
    c: DistanceY(g1,g1) = 3
    c: Coincident(g2,g-17)
    c: Vertical(g2)
    c: Coincident(g3,g-16)
    c: Vertical(g3)
    c: DistanceY(g2,g2) = 2
    c: DistanceY(g3,g3) = 2
    c: Coincident(g4,g3)
    c: Coincident(g4,g2)
    c: Coincident(g5,g-17)
    c: Coincident(g5,g2)
    c: Coincident(g6,g1)
    c: Horizontal(g6)
    c: Coincident(g6,g5)
    c: Coincident(g7,g-15)
    c: Coincident(g8,g7)
    c: Coincident(g8,g3)
    c: Coincident(g8,g-15)
    c: Horizontal(g9)
    c: DistanceY(g-13,g9) = 2
    c: Coincident(g10,g7)
    c: Parallel(g10,g-14)
    c: Coincident(g9,g10)
    c: Distance(g11) = 2
    c: Coincident(g11,g-11)
    c: Perpendicular(g-11,g11)
    c: Distance(g12) = 2
    c: Coincident(g12,g-12)
    c: Perpendicular(g-11,g12)
    c: Coincident(g13,g11)
    c: Coincident(g13,g12)
    c: Coincident(g14,g-32)
    c: Coincident(g14,g12)
    c: Coincident(g14,g9)
    c: Coincident(g15,g-10)
    c: Coincident(g15,g11)
    c: Parallel(g16,g-22)
    c: Distance(g17) = 4
    c: PointOnObject(g17,g16)
    c: Coincident(g15,g16)
    c: Horizontal(g18)
    c: Coincident(g18,g16)
    c: Coincident(g19,g0)
    c: PointOnObject(g19,g-39)
    c: DistanceY(g19,g-36) = 2
    c: Coincident(g18,g19)
    c: Diameter(g22) = 3.6
    c: Coincident(g22,g-9)
    c: Diameter(g23) = 3.6
    c: Coincident(g23,g-8)
    c: Diameter(g24) = 3.6
    c: Diameter(g25) = 3.6
    c: Diameter(g26) = 3.6
    c: Diameter(g27) = 3.6
    c: Diameter(g28) = 3.6
    c: Coincident(g27,g-4)
    c: Coincident(g28,g-3)
    c: Coincident(g25,g-6)
    c: Coincident(g26,g-5)
    c: Coincident(g24,g-7)
    c: Parallel(g20,g-21)
    c: Equal(g20,g-21)
    c: Parallel(g21,g-19)
    c: Equal(g21,g-19)
    c: Distance(g29) = 0.2
    c: Distance(g30) = 0.2
    c: Parallel(g29,g-20)
    c: Parallel(g31,g-20)
    c: Equal(g31,g-20)
    c: Coincident(g30,g31)
    c: Coincident(g31,g29)
    c: Coincident(g29,g-21)
    c: Parallel(g30,g31)
    c: Coincident(g17,g30)
    c: Coincident(g20,g29)
    c: Coincident(g21,g30)
    c: Perpendicular(g16,g17)
    c: Coincident(g32,g21)
    c: Coincident(g32,g20)
    c: Perpendicular(g10,g7)
    c: Horizontal(g33)
    c: Symmetric(g-24,g-24,g33)
    c: PointOnObject(g33,g-28)
    c: Symmetric(g-24,g-24,g34)
    c: DistanceY(g35,g35) = 25
    c: Symmetric(g35,g35,g33)
    c: Distance(g36) = 41
    c: Coincident(g36,g35)
    c: Horizontal(g36)
    c: Coincident(g37,g35)
    c: Horizontal(g37)
    c: Coincident(g38,g36)
    c: Vertical(g38)
    c: Coincident(g37,g38)
    c: Diameter(g39) = 6.8
    c: Diameter(g40) = 6.8
    c: Tangent(g39,g36)
    c: Tangent(g40,g37)
    c: Tangent(g39,g35)
    c: Tangent(g40,g35)
    c: Diameter(g41) = 6.8
    c: Diameter(g42) = 6.8
    c: Tangent(g41,g36)
    c: Tangent(g42,g37)
    c: DistanceX(g41,g39) = 24.6
    c: DistanceX(g42,g40) = 24.6
    c: Distance(g43) = 11.2
    c: Coincident(g43,g33)
    c: PointOnObject(g43,g33)
    c: PointOnObject(g43,g35)
    c: Distance(g44) = 21
    c: Coincident(g44,g43)
    c: PointOnObject(g44,g33)
    c: Coincident(g45,g46)
    c: Coincident(g46,g47)
    c: Coincident(g47,g48)
    c: Coincident(g48,g45)
    c: Horizontal(g45)
    c: Horizontal(g47)
    c: Vertical(g46)
    c: Vertical(g48)
    c: Symmetric(g47,g45,g49)
    c: Distance(g46,g48) = 10.6
    c: Distance(g45,g47) = 10
    c: Coincident(g49,g44)
    c: Diameter(g50) = 5.6
    c: Coincident(g50,g44)
    c: Distance(g51) = 11
    c: Symmetric(g51,g51,g33)
    c: DistanceX(g51,g43) = 9
    c: Diameter(g52) = 6
    c: Coincident(g52,g51)
    c: Diameter(g53) = 6
    c: Coincident(g53,g51)
    c: Coincident(g40,g55)
    c: Coincident(g39,g54)
    c: Coincident(g41,g57)
    c: Coincident(g42,g56)
    c: Diameter(g58) = 3
    c: Diameter(g59) = 3
    c: Diameter(g60) = 3
    c: Coincident(g58,g-44)
    c: Coincident(g59,g-46)
    c: Coincident(g60,g-45)
FEATURE [Sketcher::SketchObject] Sketch078
  ArcFitTolerance = 1e-06
  AttachmentSupport = -> [XZ_Plane005]
  FullyConstrained = true
  MakeInternals = false
  MapMode = 5
  Placement = pos=(0,0,0) rot=(1,0,0;1.5708rad)
  sketch-geometry (5):
    g0: LineSegment [constr] StartX=0 StartY=5.5 StartZ=0 EndX=0 EndY=-5.5 EndZ=0
    g1: ArcOfCircle CenterX=0 CenterY=5.5 CenterZ=0 NormalX=0 NormalY=0 NormalZ=1 AngleXU=0 Radius=2.7 StartAngle=0 EndAngle=3.14159
    g2: ArcOfCircle CenterX=0 CenterY=-5.5 CenterZ=0 NormalX=0 NormalY=0 NormalZ=1 AngleXU=0 Radius=2.7 StartAngle=3.1416 EndAngle=6.28318
    g3: LineSegment StartX=-2.7 StartY=5.5 StartZ=0 EndX=-2.7 EndY=-5.50001 EndZ=0
    g4: LineSegment StartX=2.7 StartY=5.5 StartZ=0 EndX=2.7 EndY=-5.50001 EndZ=0
  constraints (13):
    c: Distance(g0) = 11
    c: Vertical(g0)
    c: Symmetric(g0,g0,g-1)
    c: Radius(g1) = 2.7
    c: Coincident(g1,g0)
    c: Radius(g2) = 2.7
    c: Coincident(g2,g0)
    c: Vertical(g3)
    c: Vertical(g4)
    c: Coincident(g2,g4)
    c: Coincident(g2,g3)
    c: Tangent(g3,g1) = -1.5708
    c: Tangent(g4,g1) = 1.5708
FEATURE [PartDesign::Pad] Pad002
  Direction = (0,-1,2e-16)
  Length = 0.8
  Length2 = 10
  Placement = pos=(0,0,0) rot=(1,0,0;1.5708rad)
  Profile = -> Sketch078
  ReferenceAxis = -> Sketch078 [N_Axis]
  Refine = true
  Suppressed = false
  Type = 0
FEATURE [Sketcher::SketchObject] Sketch079
  ArcFitTolerance = 1e-06
  AttachmentSupport = -> [XZ_Plane005]
  ExternalGeometry = -> [Sketch078]
  FullyConstrained = true
  MakeInternals = false
  MapMode = 5
  Placement = pos=(0,0,0) rot=(1,0,0;1.5708rad)
  sketch-geometry (2):
    g0: Circle CenterX=-1e-16 CenterY=5.5 CenterZ=0 NormalX=0 NormalY=0 NormalZ=1 AngleXU=0 Radius=2.7
    g1: Circle CenterX=0 CenterY=-5.5 CenterZ=0 NormalX=0 NormalY=0 NormalZ=1 AngleXU=0 Radius=2.7
  constraints (4):
    c: Coincident(g0,g-3)
    c: PointOnObject(g-3,g0)
    c: Coincident(g1,g-4)
    c: Equal(g1,g-4)
FEATURE [PartDesign::Pad] Pad003
  BaseFeature = -> Pad002
  Direction = (0,-1,2e-16)
  Length = 5
  Length2 = 10
  Placement = pos=(0,0,0) rot=(1,0,0;1.5708rad)
  Profile = -> Sketch079
  ReferenceAxis = -> Sketch079 [N_Axis]
  Refine = true
  Suppressed = false
  Type = 0
FEATURE [PartDesign::Fillet] Fillet001
  Base = -> Pad003 [Edge16,Edge14]
  BaseFeature = -> Pad003
  Placement = pos=(0,0,0) rot=(1,0,0;1.5708rad)
  Radius = 0.4
  Refine = true
  SupportTransform = false
  Suppressed = false
  UseAllEdges = false
FEATURE [PartDesign::Body] Body005  label="pulsanti lato destro"
  AllowCompound = false
  Group = -> [Sketch078,Pad002,Sketch079,Pad003,Fillet001]
  Origin = -> Origin005
  Tip = -> Fillet001
FEATURE [PartDesign::SubShapeBinder] Binder
  BindCopyOnChange = 0
  BindMode = 0
  ClaimChildren = false
  Context = -> Body006 [Binder.]
  Fuse = false
  MakeFace = true
  OffsetFill = false
  OffsetIntersection = false
  OffsetJoinType = 0
  OffsetOpenResult = false
  PartialLoad = false
  Refine = true
  Relative = true
  Support = -> [Body[Sketch074.]]
  _Version = 2
FEATURE [PartDesign::SubShapeBinder] Binder001
  BindCopyOnChange = 0
  BindMode = 0
  ClaimChildren = false
  Context = -> Body007 [Binder001.]
  Fuse = false
  MakeFace = true
  OffsetFill = false
  OffsetIntersection = false
  OffsetJoinType = 0
  OffsetOpenResult = false
  PartialLoad = false
  Refine = true
  Relative = true
  Support = -> [Body[Sketch075.]]
  _Version = 2
FEATURE [Mesh::Feature] logo_per_PCB_definitivo_positivo
  Placement = pos=(-191,17,-66) rot=(0,1,1;0rad)
FEATURE [Sketcher::SketchObject] Sketch114  label="Sketch114 - base lato DX"
  ArcFitTolerance = 1e-06
  AttachmentSupport = -> [Binder001]
  ExternalGeometry = -> [Binder001]
  FullyConstrained = true
  MakeInternals = false
  MapMode = 5
  Placement = pos=(0,1e-15,0) rot=(0,0.707107,0.707107;3.14159rad)
  sketch-geometry (30):
    g0: Circle CenterX=5.6 CenterY=34.8 CenterZ=0 NormalX=0 NormalY=0 NormalZ=1 AngleXU=0 Radius=1.8
    g1: Circle CenterX=5.6 CenterY=7.6 CenterZ=0 NormalX=0 NormalY=0 NormalZ=1 AngleXU=0 Radius=1.8
    g2: Circle CenterX=24.2 CenterY=26.7 CenterZ=0 NormalX=0 NormalY=0 NormalZ=1 AngleXU=0 Radius=3
    g3: Circle CenterX=24.2 CenterY=15.7 CenterZ=0 NormalX=0 NormalY=0 NormalZ=1 AngleXU=0 Radius=3
    g4: Circle CenterX=36.2 CenterY=21.2 CenterZ=0 NormalX=0 NormalY=0 NormalZ=1 AngleXU=0 Radius=2.8
    g5: Circle CenterX=78.51 CenterY=34.8 CenterZ=0 NormalX=0 NormalY=0 NormalZ=1 AngleXU=0 Radius=1.8
    g6: Circle CenterX=78.51 CenterY=7.6 CenterZ=0 NormalX=0 NormalY=0 NormalZ=1 AngleXU=0 Radius=1.8
    g7: Circle CenterX=184.08 CenterY=34.8 CenterZ=0 NormalX=0 NormalY=0 NormalZ=1 AngleXU=0 Radius=1.8
    g8: Circle CenterX=213.443 CenterY=-76.8316 CenterZ=0 NormalX=0 NormalY=0 NormalZ=1 AngleXU=0 Radius=1.8
    g9: Circle CenterX=179.305 CenterY=-76.8316 CenterZ=0 NormalX=0 NormalY=0 NormalZ=1 AngleXU=0 Radius=1.8
    g10: ArcOfCircle [constr] CenterX=132.428 CenterY=4 CenterZ=0 NormalX=0 NormalY=0 NormalZ=1 AngleXU=0 Radius=16 StartAngle=0.314159 EndAngle=1.5708
    g11: ArcOfCircle CenterX=107.6 CenterY=4 CenterZ=0 NormalX=0 NormalY=0 NormalZ=1 AngleXU=0 Radius=16 StartAngle=1.5708 EndAngle=3.00366
    g12: ArcOfCircle CenterX=207.583 CenterY=4 CenterZ=0 NormalX=0 NormalY=0 NormalZ=1 AngleXU=0 Radius=17 StartAngle=1.85815 EndAngle=3.57792
    g13: ArcOfCircle CenterX=184.801 CenterY=-67.3089 CenterZ=0 NormalX=0 NormalY=0 NormalZ=1 AngleXU=0 Radius=33.7833 StartAngle=5.88425 EndAngle=6.71952
    g14: LineSegment StartX=0 StartY=39.2 StartZ=0 EndX=0 EndY=3.2 EndZ=0
    g15: LineSegment StartX=0 StartY=3.2 StartZ=0 EndX=82.8 EndY=3.2 EndZ=0
    g16: LineSegment StartX=82.8 StartY=3.2 StartZ=0 EndX=82.8 EndY=6.2 EndZ=0
    g17: LineSegment StartX=82.8 StartY=6.2 StartZ=0 EndX=91.752 EndY=6.2 EndZ=0
    g18: LineSegment StartX=107.6 StartY=20 StartZ=0 EndX=132.428 EndY=20 EndZ=0
    g19: LineSegment StartX=147.645 StartY=8.94427 StartZ=0 EndX=176.685 EndY=-80.4316 EndZ=0
    g20: LineSegment StartX=176.685 StartY=-80.4316 StartZ=0 EndX=215.932 EndY=-80.4316 EndZ=0
    g21: LineSegment StartX=215.42 StartY=-53.0314 StartZ=0 EndX=192.176 EndY=-3.18451 EndZ=0
    g22: LineSegment StartX=202.765 StartY=20.303 StartZ=0 EndX=195.887 EndY=39.2 EndZ=0
    g23: LineSegment StartX=195.887 StartY=39.2 StartZ=0 EndX=0 EndY=39.2 EndZ=0
    g24: LineSegment StartX=196.467 StartY=26.4942 StartZ=0 EndX=194.073 EndY=33.0721 EndZ=0
    g25: LineSegment StartX=194.073 StartY=33.0721 StartZ=0 EndX=189.939 EndY=31.5672 EndZ=0
    g26: LineSegment StartX=189.939 StartY=31.5672 StartZ=0 EndX=192.333 EndY=24.9893 EndZ=0
    g27: LineSegment StartX=192.333 StartY=24.9893 StartZ=0 EndX=196.467 EndY=26.4942 EndZ=0
    g28: LineSegment StartX=132.428 StartY=20 StartZ=0 EndX=144.053 EndY=20 EndZ=0
    g29: LineSegment StartX=144.053 StartY=20 StartZ=0 EndX=147.645 EndY=8.94427 EndZ=0
  constraints (65):
    c: Equal(g0,g-25)
    c: Equal(g2,g-29)
    c: Equal(g3,g-30)
    c: Equal(g4,g-28)
    c: Equal(g1,g-26)
    c: Coincident(g0,g-25)
    c: Coincident(g1,g-26)
    c: Coincident(g2,g-29)
    c: Coincident(g3,g-30)
    c: Coincident(g4,g-28)
    c: Equal(g5,g-23)
    c: Equal(g6,g-24)
    c: Coincident(g5,g-23)
    c: Coincident(g6,g-24)
    c: Equal(g7,g-20)
    c: Coincident(g7,g-20)
    c: Equal(g9,g-22)
    c: Coincident(g9,g-22)
    c: Equal(g8,g-21)
    c: Coincident(g8,g-21)
    c: Equal(g13,g-12)
    c: Equal(g12,g-14)
    c: Equal(g10,g-9)
    c: Equal(g11,g-7)
    c: Coincident(g14,g-27)
    c: Coincident(g14,g-27)
    c: Coincident(g15,g14)
    c: Coincident(g15,g-5)
    c: Coincident(g16,g15)
    c: Coincident(g16,g-6)
    c: Coincident(g17,g16)
    c: Coincident(g17,g-7)
    c: Coincident(g11,g17)
    c: Coincident(g11,g-8)
    c: Coincident(g18,g11)
    c: Coincident(g18,g-9)
    c: Coincident(g10,g18)
    c: Coincident(g10,g-10)
    c: Coincident(g19,g10)
    c: Coincident(g19,g-11)
    c: Coincident(g20,g19)
    c: Coincident(g20,g-12)
    c: Coincident(g13,g20)
    c: Coincident(g13,g-13)
    c: Coincident(g21,g13)
    c: Coincident(g21,g-14)
    c: Coincident(g12,g21)
    c: Coincident(g12,g-15)
    c: Coincident(g22,g12)
    c: Coincident(g22,g-15)
    c: Coincident(g23,g22)
    c: Coincident(g23,g14)
    c: Coincident(g24,g-18)
    c: Coincident(g24,g-16)
    c: Coincident(g25,g24)
    c: Coincident(g25,g-19)
    c: Coincident(g26,g25)
    c: Coincident(g26,g-19)
    c: Coincident(g27,g26)
    c: Coincident(g27,g24)
    c: Coincident(g29,g10)
    c: Coincident(g28,g10)
    c: Coincident(g29,g28)
    c: Parallel(g28,g18)
    c: Parallel(g29,g19)
FEATURE [PartDesign::Pad] Pad011
  Direction = (0,1,-2e-16)
  Length = 2
  Length2 = 10
  Profile = -> Sketch114
  ReferenceAxis = -> Sketch114 [N_Axis]
  Refine = true
  Reversed = true
  Suppressed = false
  Type = 0
FEATURE [Sketcher::SketchObject] Sketch115
  ArcFitTolerance = 1e-06
  AttachmentSupport = -> [Pad011]
  ExternalGeometry = -> [Binder001]
  FullyConstrained = true
  MakeInternals = false
  MapMode = 5
  Placement = pos=(0,1.7e-15,0) rot=(0,0.707107,0.707107;3.14159rad)
  sketch-geometry (4):
    g0: ArcOfCircle CenterX=24.2 CenterY=26.7 CenterZ=0 NormalX=0 NormalY=0 NormalZ=1 AngleXU=0 Radius=3 StartAngle=4.48384e-08 EndAngle=3.14159
    g1: ArcOfCircle CenterX=24.2 CenterY=15.7 CenterZ=0 NormalX=0 NormalY=0 NormalZ=1 AngleXU=0 Radius=3 StartAngle=3.14159 EndAngle=6.28318
    g2: LineSegment StartX=21.2 StartY=26.7 StartZ=0 EndX=21.2 EndY=15.7 EndZ=0
    g3: LineSegment StartX=27.2 StartY=26.7 StartZ=0 EndX=27.2 EndY=15.7 EndZ=0
  constraints (12):
    c: Equal(g1,g-4)
    c: Equal(g0,g-3)
    c: Coincident(g0,g-3)
    c: Coincident(g1,g-4)
    c: Vertical(g2)
    c: Vertical(g3)
    c: Tangent(g3,g-3)
    c: Tangent(g2,g-3)
    c: Coincident(g0,g2)
    c: Coincident(g0,g3)
    c: Coincident(g1,g2)
    c: Coincident(g3,g1)
FEATURE [Sketcher::SketchObject] Sketch117  label="Sketch117 - fori per inserto M3 x 3 x 4.5"
  ArcFitTolerance = 1e-06
  AttachmentSupport = -> [Pad011]
  ExternalGeometry = -> [Binder001]
  FullyConstrained = true
  MakeInternals = false
  MapMode = 5
  Placement = pos=(0,1.7e-15,0) rot=(0,0.707107,0.707107;3.14159rad)
  sketch-geometry (4):
    g0: Circle CenterX=43.2 CenterY=30.3 CenterZ=0 NormalX=0 NormalY=0 NormalZ=1 AngleXU=0 Radius=2.25
    g1: Circle CenterX=43.2 CenterY=12.1 CenterZ=0 NormalX=0 NormalY=0 NormalZ=1 AngleXU=0 Radius=2.25
    g2: Circle CenterX=18.6 CenterY=30.3 CenterZ=0 NormalX=0 NormalY=0 NormalZ=1 AngleXU=0 Radius=2.25
    g3: Circle CenterX=18.6 CenterY=12.1 CenterZ=0 NormalX=0 NormalY=0 NormalZ=1 AngleXU=0 Radius=2.25
  constraints (8):
    c: Diameter(g0) = 4.5
    c: Diameter(g1) = 4.5
    c: Diameter(g2) = 4.5
    c: Diameter(g3) = 4.5
    c: Coincident(g2,g-3)
    c: Coincident(g3,g-6)
    c: Coincident(g0,g-4)
    c: Coincident(g1,g-5)
FEATURE [Sketcher::SketchObject] Sketch118
  ArcFitTolerance = 1e-06
  AttachmentSupport = -> [Pad011]
  ExternalGeometry = -> [Binder001]
  FullyConstrained = true
  MakeInternals = false
  MapMode = 5
  Placement = pos=(0,-2,0) rot=(1,0,0;1.5708rad)
  sketch-geometry (12):
    g0: Circle CenterX=-78.51 CenterY=34.8 CenterZ=0 NormalX=0 NormalY=0 NormalZ=1 AngleXU=0 Radius=1.8
    g1: Circle CenterX=-78.51 CenterY=7.6 CenterZ=0 NormalX=0 NormalY=0 NormalZ=1 AngleXU=0 Radius=1.8
    g2: Circle CenterX=-5.6 CenterY=34.8 CenterZ=0 NormalX=0 NormalY=0 NormalZ=1 AngleXU=0 Radius=1.8
    g3: Circle CenterX=-5.6 CenterY=7.6 CenterZ=0 NormalX=0 NormalY=0 NormalZ=1 AngleXU=0 Radius=1.8
    g4: LineSegment StartX=0 StartY=39.2 StartZ=0 EndX=0 EndY=3.2 EndZ=0
    g5: LineSegment StartX=0 StartY=3.2 StartZ=0 EndX=-82.8 EndY=3.2 EndZ=0
    g6: LineSegment StartX=-82.8 StartY=3.2 StartZ=0 EndX=-82.8 EndY=39.2 EndZ=0
    g7: LineSegment StartX=-82.8 StartY=39.2 StartZ=0 EndX=0 EndY=39.2 EndZ=0
    g8: ArcOfCircle CenterX=-65 CenterY=21.2 CenterZ=0 NormalX=0 NormalY=0 NormalZ=1 AngleXU=0 Radius=10 StartAngle=1.5708 EndAngle=4.71239
    g9: ArcOfCircle CenterX=-19 CenterY=21.2 CenterZ=0 NormalX=0 NormalY=0 NormalZ=1 AngleXU=0 Radius=10 StartAngle=4.71239 EndAngle=7.85398
    g10: LineSegment StartX=-65 StartY=31.2 StartZ=0 EndX=-19 EndY=31.2 EndZ=0
    g11: LineSegment StartX=-65 StartY=11.2 StartZ=0 EndX=-19 EndY=11.2 EndZ=0
  constraints (25):
    c: Equal(g2,g-5)
    c: Equal(g3,g-7)
    c: Equal(g1,g-6)
    c: Equal(g0,g-4)
    c: Coincident(g0,g-4)
    c: Coincident(g1,g-6)
    c: Coincident(g3,g-7)
    c: Coincident(g2,g-5)
    c: Coincident(g4,g-8)
    c: Coincident(g4,g-9)
    c: Coincident(g5,g4)
    c: Coincident(g5,g-10)
    c: Coincident(g6,g5)
    c: PointOnObject(g6,g-3)
    c: Vertical(g6)
    c: Coincident(g7,g6)
    c: Coincident(g7,g4)
    c: Tangent(g8,g10) = 1.5708
    c: Tangent(g8,g11) = -1.5708
    c: Tangent(g9,g10) = 1.5708
    c: Tangent(g9,g11) = -1.5708
    c: Equal(g8,g9)
    c: Radius(g8) = 10
    c: Coincident(g8,g-11)
    c: Coincident(g9,g-12)
FEATURE [Sketcher::SketchObject] Sketch120
  ArcFitTolerance = 1e-06
  AttachmentSupport = -> [Pad011]
  ExternalGeometry = -> [Binder001]
  FullyConstrained = true
  MakeInternals = false
  MapMode = 5
  Placement = pos=(0,-2,0) rot=(1,0,0;1.5708rad)
  sketch-geometry (4):
    g0: LineSegment StartX=-137.815 StartY=39.2 StartZ=0 EndX=-142.655 EndY=24.303 EndZ=0
    g1: LineSegment StartX=-137.815 StartY=39.2 StartZ=0 EndX=-110.815 EndY=39.2 EndZ=0
    g2: LineSegment StartX=-142.655 StartY=24.303 StartZ=0 EndX=-110.815 EndY=24.303 EndZ=0
    g3: ArcOfCircle CenterX=-92.2534 CenterY=31.7515 CenterZ=0 NormalX=0 NormalY=0 NormalZ=1 AngleXU=0 Radius=20 StartAngle=2.75997 EndAngle=3.52321
  constraints (12):
    c: PointOnObject(g0,g-3)
    c: Coincident(g1,g0)
    c: PointOnObject(g1,g-3)
    c: Coincident(g2,g0)
    c: Horizontal(g2)
    c: Tangent(g0,g-4)
    c: Vertical(g2,g1)
    c: DistanceX(g1,g1) = 27
    c: DistanceY(g-6,g0) = 4
    c: Radius(g3) = 20
    c: Coincident(g3,g1)
    c: Coincident(g3,g2)
FEATURE [Sketcher::SketchObject] Sketch121
  ArcFitTolerance = 1e-06
  AttachmentSupport = -> [Pad011]
  ExternalGeometry = -> [Binder001]
  FullyConstrained = true
  MakeInternals = false
  MapMode = 5
  Placement = pos=(0,-2,0) rot=(1,0,0;1.5708rad)
  sketch-geometry (15):
    g0: LineSegment StartX=-137.815 StartY=39.2 StartZ=0 EndX=-143.955 EndY=20.303 EndZ=0
    g1: LineSegment StartX=-143.955 StartY=20.303 StartZ=0 EndX=-190.141 EndY=20.303 EndZ=0
    g2: LineSegment StartX=-190.141 StartY=20.303 StartZ=0 EndX=-186.139 EndY=31.3 EndZ=0
    g3: LineSegment StartX=-178.754 StartY=39.2 StartZ=0 EndX=-180.791 EndY=33.6029 EndZ=0
    g4: ArcOfCircle CenterX=-184.08 CenterY=34.8 CenterZ=0 NormalX=0 NormalY=0 NormalZ=1 AngleXU=0 Radius=3.5 StartAngle=4.71239 EndAngle=5.93412
    g5: LineSegment StartX=-184.08 StartY=31.3 StartZ=0 EndX=-186.139 EndY=31.3 EndZ=0
    g6: LineSegment StartX=-137.815 StartY=39.2 StartZ=0 EndX=-156.815 EndY=39.2 EndZ=0
    g7: LineSegment StartX=-168.815 StartY=39.2 StartZ=0 EndX=-178.754 EndY=39.2 EndZ=0
    g8: LineSegment StartX=-157.815 StartY=39.2 StartZ=0 EndX=-167.815 EndY=39.2 EndZ=0
    g9: LineSegment StartX=-168.815 StartY=31.2 StartZ=0 EndX=-156.815 EndY=31.2 EndZ=0
    g10: LineSegment StartX=-167.436 StartY=36.2 StartZ=0 EndX=-157.436 EndY=36.2 EndZ=0
    g11: ArcOfCircle CenterX=-176.411 CenterY=35.2 CenterZ=0 NormalX=0 NormalY=0 NormalZ=1 AngleXU=0 Radius=20 StartAngle=6.08183 EndAngle=6.48454
    g12: ArcOfCircle CenterX=-188.411 CenterY=35.2 CenterZ=0 NormalX=0 NormalY=0 NormalZ=1 AngleXU=0 Radius=20 StartAngle=6.08183 EndAngle=6.48454
    g13: ArcOfCircle CenterX=-177.411 CenterY=35.2 CenterZ=0 NormalX=0 NormalY=0 NormalZ=1 AngleXU=0 Radius=20 StartAngle=0.0500209 EndAngle=0.201358
    g14: ArcOfCircle CenterX=-187.411 CenterY=35.2 CenterZ=0 NormalX=0 NormalY=0 NormalZ=1 AngleXU=0 Radius=20 StartAngle=0.0500209 EndAngle=0.201358
  constraints (46):
    c: PointOnObject(g0,g-3)
    c: Tangent(g0,g-5)
    c: Coincident(g1,g0)
    c: Horizontal(g1)
    c: Coincident(g2,g1)
    c: PointOnObject(g3,g-3)
    c: Parallel(g3,g-6)
    c: Parallel(g2,g-6)
    c: Radius(g4) = 3.5
    c: Coincident(g4,g-7)
    c: Tangent(g3,g4) = 1.5708
    c: Horizontal(g5)
    c: Tangent(g5,g4) = 1.5708
    c: DistanceX(g-8,g5) = 3.8
    c: Coincident(g2,g5)
    c: Coincident(g6,g0)
    c: PointOnObject(g6,g-3)
    c: DistanceX(g6,g6) = 19
    c: PointOnObject(g7,g-3)
    c: DistanceX(g7,g6) = 12
    c: Coincident(g7,g3)
    c: PointOnObject(g8,g-3)
    c: PointOnObject(g8,g-3)
    c: DistanceX(g8,g8) = 10
    c: DistanceX(g8,g6) = 1
    c: Horizontal(g9)
    c: Vertical(g7,g9)
    c: Vertical(g6,g9)
    c: DistanceY(g9,g7) = 8
    c: Horizontal(g10)
    c: Equal(g8,g10)
    c: DistanceY(g10,g8) = 3
    c: Radius(g11) = 20
    c: Coincident(g11,g6)
    c: Coincident(g11,g9)
    c: Radius(g12) = 20
    c: Coincident(g12,g7)
    c: Coincident(g12,g9)
    c: Equal(g13,g11)
    c: Coincident(g13,g8)
    c: Coincident(g13,g10)
    c: Horizontal(g13,g11)
    c: Equal(g14,g12)
    c: Coincident(g14,g8)
    c: Coincident(g14,g10)
    c: Horizontal(g1,g-6)
FEATURE [Sketcher::SketchObject] Sketch122
  ArcFitTolerance = 1e-06
  AttachmentSupport = -> [Pad011]
  ExternalGeometry = -> [Binder001]
  FullyConstrained = true
  MakeInternals = false
  MapMode = 5
  Placement = pos=(0,-2,0) rot=(1,0,0;1.5708rad)
  sketch-geometry (8):
    g0: LineSegment StartX=-202.765 StartY=20.303 StartZ=0 EndX=-143.955 EndY=20.303 EndZ=0
    g1: ArcOfCircle CenterX=-184.801 CenterY=-67.3089 CenterZ=0 NormalX=0 NormalY=0 NormalZ=1 AngleXU=0 Radius=33.7833 StartAngle=2.70526 EndAngle=3.54053
    g2: LineSegment StartX=-176.685 StartY=-80.4316 StartZ=0 EndX=-215.932 EndY=-80.4316 EndZ=0
    g3: LineSegment StartX=-215.42 StartY=-53.0315 StartZ=0 EndX=-192.176 EndY=-3.18454 EndZ=0
    g4: ArcOfCircle CenterX=-207.583 CenterY=4 CenterZ=0 NormalX=0 NormalY=0 NormalZ=1 AngleXU=0 Radius=17 StartAngle=5.84685 EndAngle=7.56663
    g5: Circle CenterX=-213.443 CenterY=-76.8316 CenterZ=0 NormalX=0 NormalY=0 NormalZ=1 AngleXU=0 Radius=3
    g6: Circle CenterX=-179.305 CenterY=-76.8316 CenterZ=0 NormalX=0 NormalY=0 NormalZ=1 AngleXU=0 Radius=3
    g7: LineSegment StartX=-143.955 StartY=20.303 StartZ=0 EndX=-176.685 EndY=-80.4316 EndZ=0
  constraints (18):
    c: Coincident(g0,g-6)
    c: Coincident(g1,g-7)
    c: Coincident(g1,g-8)
    c: Coincident(g2,g1)
    c: Tangent(g3,g-5)
    c: Coincident(g4,g-6)
    c: Coincident(g4,g0)
    c: Coincident(g3,g4)
    c: Coincident(g1,g3)
    c: Diameter(g5) = 6
    c: Diameter(g6) = 6
    c: Coincident(g5,g-9)
    c: Coincident(g6,g-10)
    c: Horizontal(g0)
    c: Horizontal(g2)
    c: Coincident(g7,g0)
    c: Coincident(g7,g2)
    c: Tangent(g7,g-4)
FEATURE [Sketcher::SketchObject] Sketch123
  ArcFitTolerance = 1e-06
  AttachmentSupport = -> [Pad011]
  ExternalGeometry = -> [Binder001]
  FullyConstrained = true
  MakeInternals = false
  MapMode = 5
  Placement = pos=(0,-2,0) rot=(1,0,0;1.5708rad)
  sketch-geometry (4):
    g0: LineSegment StartX=-108 StartY=36.8 StartZ=0 EndX=-90 EndY=36.8 EndZ=0
    g1: LineSegment StartX=-108 StartY=36.8 StartZ=0 EndX=-108 EndY=26.8 EndZ=0
    g2: LineSegment StartX=-108 StartY=26.8 StartZ=0 EndX=-90 EndY=26.8 EndZ=0
    g3: ArcOfCircle CenterX=-94 CenterY=31.8 CenterZ=0 NormalX=0 NormalY=0 NormalZ=1 AngleXU=0 Radius=6.40312 StartAngle=5.38713 EndAngle=7.17924
  constraints (13):
    c: Horizontal(g0)
    c: Coincident(g1,g0)
    c: Vertical(g1)
    c: Coincident(g2,g1)
    c: Horizontal(g2)
    c: DistanceX(g0,g0) = 18
    c: DistanceY(g1,g1) = 10
    c: Equal(g0,g2)
    c: DistanceX(g0,g-3) = 90
    c: DistanceY(g0,g-3) = 2.4
    c: Coincident(g3,g0)
    c: Coincident(g3,g2)
    c: DistanceX(g3,g0) = 4
FEATURE [PartDesign::Chamfer] Chamfer014
  Angle = 45
  Base = -> Pad011 [Edge80,Edge4,Edge7]
  BaseFeature = -> Pad011
  ChamferType = 0
  FlipDirection = false
  Refine = true
  Size = 1.9
  Size2 = 1
  SupportTransform = false
  Suppressed = false
  UseAllEdges = false
FEATURE [PartDesign::Pocket] Pocket006
  BaseFeature = -> Chamfer014
  Direction = (0,-1,2e-16)
  Length = 1.2
  Length2 = 5
  Profile = -> Sketch115
  ReferenceAxis = -> Sketch115 [N_Axis]
  Refine = true
  Suppressed = false
  Type = 0
FEATURE [Sketcher::SketchObject] Sketch116  label="Sketch116 - pieno per inserto M3 x 3 x 4,5"
  ArcFitTolerance = 1e-06
  AttachmentSupport = -> [Pocket006]
  ExternalGeometry = -> [Binder001]
  FullyConstrained = true
  MakeInternals = false
  MapMode = 5
  Placement = pos=(0,1.7e-15,0) rot=(0,0.707107,0.707107;3.14159rad)
  sketch-geometry (4):
    g0: Circle CenterX=43.2 CenterY=30.3 CenterZ=0 NormalX=0 NormalY=0 NormalZ=1 AngleXU=0 Radius=3.4
    g1: Circle CenterX=43.2 CenterY=12.1 CenterZ=0 NormalX=0 NormalY=0 NormalZ=1 AngleXU=0 Radius=3.4
    g2: Circle CenterX=18.6 CenterY=30.3 CenterZ=0 NormalX=0 NormalY=0 NormalZ=1 AngleXU=0 Radius=3.4
    g3: Circle CenterX=18.6 CenterY=12.1 CenterZ=0 NormalX=0 NormalY=0 NormalZ=1 AngleXU=0 Radius=3.4
  constraints (8):
    c: Diameter(g0) = 6.8
    c: Diameter(g1) = 6.8
    c: Diameter(g2) = 6.8
    c: Diameter(g3) = 6.8
    c: Coincident(g2,g-3)
    c: Coincident(g0,g-4)
    c: Coincident(g3,g-6)
    c: Coincident(g1,g-5)
FEATURE [PartDesign::Pad] Pad012
  BaseFeature = -> Pocket006
  Direction = (0,1,-2e-16)
  Length = 2.4
  Length2 = 10
  Profile = -> Sketch116
  ReferenceAxis = -> Sketch116 [N_Axis]
  Refine = true
  Suppressed = false
  Type = 0
FEATURE [PartDesign::Pocket] Pocket007
  BaseFeature = -> Pad012
  Direction = (0,-1,2e-16)
  Length = 0.6
  Length2 = 2.4
  Profile = -> Sketch117
  ReferenceAxis = -> Sketch117 [N_Axis]
  Refine = true
  Suppressed = false
  Type = 4
FEATURE [PartDesign::Pad] Pad013
  BaseFeature = -> Pocket007
  Direction = (0,-1,2e-16)
  Length = 1.6
  Length2 = 10
  Profile = -> Sketch118
  ReferenceAxis = -> Sketch118 [N_Axis]
  Refine = true
  Suppressed = false
  Type = 0
FEATURE [Sketcher::SketchObject] Sketch119
  ArcFitTolerance = 1e-06
  AttachmentSupport = -> [Pad013]
  ExternalGeometry = -> [Binder001]
  FullyConstrained = true
  MakeInternals = false
  MapMode = 5
  Placement = pos=(0,-3.6,0) rot=(1,0,0;1.5708rad)
  sketch-geometry (21):
    g0: LineSegment [constr] StartX=-82.8 StartY=3.2 StartZ=0 EndX=-82.8 EndY=39.2 EndZ=0
    g1: ArcOfCircle CenterX=-78.51 CenterY=34.8 CenterZ=0 NormalX=0 NormalY=0 NormalZ=1 AngleXU=0 Radius=3.5 StartAngle=4.71239 EndAngle=6.28319
    g2: ArcOfCircle CenterX=-78.51 CenterY=7.6 CenterZ=0 NormalX=0 NormalY=0 NormalZ=1 AngleXU=0 Radius=3.5 StartAngle=0 EndAngle=1.5708
    g3: ArcOfCircle CenterX=-5.6 CenterY=34.8 CenterZ=0 NormalX=0 NormalY=0 NormalZ=1 AngleXU=0 Radius=3.5 StartAngle=3.14159 EndAngle=4.71239
    g4: ArcOfCircle CenterX=-5.6 CenterY=7.6 CenterZ=0 NormalX=0 NormalY=0 NormalZ=1 AngleXU=0 Radius=3.5 StartAngle=1.5708 EndAngle=3.14159
    g5: LineSegment StartX=0 StartY=39.2 StartZ=0 EndX=0 EndY=31.3 EndZ=0
    g6: LineSegment StartX=0 StartY=39.2 StartZ=0 EndX=-9.1 EndY=39.2 EndZ=0
    g7: LineSegment StartX=0 StartY=3.2 StartZ=0 EndX=0 EndY=11.1 EndZ=0
    g8: LineSegment StartX=0 StartY=3.2 StartZ=0 EndX=-9.1 EndY=3.2 EndZ=0
    g9: LineSegment StartX=-82.8 StartY=3.2 StartZ=0 EndX=-75.01 EndY=3.2 EndZ=0
    g10: LineSegment StartX=-82.8 StartY=3.2 StartZ=0 EndX=-82.8 EndY=11.1 EndZ=0
    g11: LineSegment StartX=-82.8 StartY=39.2 StartZ=0 EndX=-82.8 EndY=31.3 EndZ=0
    g12: LineSegment StartX=-82.8 StartY=39.2 StartZ=0 EndX=-75.01 EndY=39.2 EndZ=0
    g13: LineSegment StartX=-82.8 StartY=31.3 StartZ=0 EndX=-78.51 EndY=31.3 EndZ=0
    g14: LineSegment StartX=-75.01 StartY=39.2 StartZ=0 EndX=-75.01 EndY=34.8 EndZ=0
    g15: LineSegment StartX=-82.8 StartY=11.1 StartZ=0 EndX=-78.51 EndY=11.1 EndZ=0
    g16: LineSegment StartX=-75.01 StartY=3.2 StartZ=0 EndX=-75.01 EndY=7.6 EndZ=0
    g17: LineSegment StartX=-9.1 StartY=39.2 StartZ=0 EndX=-9.1 EndY=34.8 EndZ=0
    g18: LineSegment StartX=0 StartY=31.3 StartZ=0 EndX=-5.6 EndY=31.3 EndZ=0
    g19: LineSegment StartX=0 StartY=11.1 StartZ=0 EndX=-5.6 EndY=11.1 EndZ=0
    g20: LineSegment StartX=-9.1 StartY=3.2 StartZ=0 EndX=-9.1 EndY=7.6 EndZ=0
  constraints (51):
    c: Coincident(g0,g-10)
    c: PointOnObject(g0,g-8)
    c: Vertical(g0)
    c: Coincident(g1,g-3)
    c: Coincident(g2,g-4)
    c: Coincident(g3,g-5)
    c: Coincident(g4,g-6)
    c: Radius(g4) = 3.5
    c: Radius(g3) = 3.5
    c: Radius(g1) = 3.5
    c: Radius(g2) = 3.5
    c: Coincident(g5,g-9)
    c: PointOnObject(g5,g-9)
    c: Coincident(g6,g5)
    c: PointOnObject(g6,g-8)
    c: Coincident(g7,g-9)
    c: PointOnObject(g7,g-9)
    c: Coincident(g8,g7)
    c: PointOnObject(g8,g-7)
    c: Coincident(g9,g0)
    c: PointOnObject(g9,g-7)
    c: Coincident(g10,g0)
    c: PointOnObject(g10,g0)
    c: Coincident(g11,g0)
    c: PointOnObject(g11,g0)
    c: Coincident(g12,g0)
    c: PointOnObject(g12,g-8)
    c: Coincident(g13,g11)
    c: Horizontal(g13)
    c: Coincident(g14,g12)
    c: Vertical(g14)
    c: Coincident(g15,g10)
    c: Horizontal(g15)
    c: Coincident(g16,g9)
    c: Vertical(g16)
    c: Coincident(g17,g6)
    c: Vertical(g17)
    c: Coincident(g18,g5)
    c: Horizontal(g18)
    c: Coincident(g19,g7)
    c: Horizontal(g19)
    c: Coincident(g20,g8)
    c: Vertical(g20)
    c: Tangent(g20,g4) = 1.5708
    c: Tangent(g4,g19) = -1.5708
    c: Tangent(g18,g3) = 1.5708
    c: Tangent(g3,g17) = -1.5708
    c: Tangent(g13,g1) = -1.5708
    c: Tangent(g1,g14) = 1.5708
    c: Tangent(g16,g2) = -1.5708
    c: Tangent(g2,g15) = 1.5708
FEATURE [PartDesign::Pocket] Pocket008
  BaseFeature = -> Pad013
  Direction = (0,1,-2e-16)
  Length = 1.6
  Length2 = 5
  Profile = -> Sketch119
  ReferenceAxis = -> Sketch119 [N_Axis]
  Refine = true
  Suppressed = false
  Type = 0
FEATURE [PartDesign::Pad] Pad017
  BaseFeature = -> Pocket008
  Direction = (0,-1,2e-16)
  Length = 1.6
  Length2 = 10
  Profile = -> Sketch123
  ReferenceAxis = -> Sketch123 [N_Axis]
  Refine = true
  Suppressed = false
  Type = 0
FEATURE [Sketcher::SketchObject] Sketch125
  ArcFitTolerance = 1e-06
  AttachmentSupport = -> [Pad017]
  ExternalGeometry = -> [Pad017]
  FullyConstrained = true
  MakeInternals = false
  MapMode = 5
  Placement = pos=(0,-3.6,8e-16) rot=(1,0,0;1.5708rad)
  sketch-geometry (20):
    g0: LineSegment StartX=-108 StartY=35.8 StartZ=0 EndX=-108 EndY=35 EndZ=0
    g1: LineSegment StartX=-108 StartY=35 StartZ=0 EndX=-97 EndY=35 EndZ=0
    g2: LineSegment StartX=-97 StartY=35 StartZ=0 EndX=-97 EndY=35.8 EndZ=0
    g3: LineSegment StartX=-97 StartY=35.8 StartZ=0 EndX=-108 EndY=35.8 EndZ=0
    g4: LineSegment StartX=-108 StartY=28.6 StartZ=0 EndX=-108 EndY=27.8 EndZ=0
    g5: LineSegment StartX=-108 StartY=27.8 StartZ=0 EndX=-97 EndY=27.8 EndZ=0
    g6: LineSegment StartX=-97 StartY=27.8 StartZ=0 EndX=-97 EndY=28.6 EndZ=0
    g7: LineSegment StartX=-97 StartY=28.6 StartZ=0 EndX=-108 EndY=28.6 EndZ=0
    g8: LineSegment StartX=-108 StartY=30.4 StartZ=0 EndX=-108 EndY=29.6 EndZ=0
    g9: LineSegment StartX=-108 StartY=29.6 StartZ=0 EndX=-97 EndY=29.6 EndZ=0
    g10: LineSegment StartX=-97 StartY=29.6 StartZ=0 EndX=-97 EndY=30.4 EndZ=0
    g11: LineSegment StartX=-97 StartY=30.4 StartZ=0 EndX=-108 EndY=30.4 EndZ=0
    g12: LineSegment StartX=-108 StartY=32.2 StartZ=0 EndX=-108 EndY=31.4 EndZ=0
    g13: LineSegment StartX=-108 StartY=31.4 StartZ=0 EndX=-97 EndY=31.4 EndZ=0
    g14: LineSegment StartX=-97 StartY=31.4 StartZ=0 EndX=-97 EndY=32.2 EndZ=0
    g15: LineSegment StartX=-97 StartY=32.2 StartZ=0 EndX=-108 EndY=32.2 EndZ=0
    g16: LineSegment StartX=-108 StartY=34 StartZ=0 EndX=-108 EndY=33.2 EndZ=0
    g17: LineSegment StartX=-108 StartY=33.2 StartZ=0 EndX=-97 EndY=33.2 EndZ=0
    g18: LineSegment StartX=-97 StartY=33.2 StartZ=0 EndX=-97 EndY=34 EndZ=0
    g19: LineSegment StartX=-97 StartY=34 StartZ=0 EndX=-108 EndY=34 EndZ=0
  constraints (55):
    c: Coincident(g1,g0)
    c: Horizontal(g1)
    c: Coincident(g2,g1)
    c: Vertical(g2)
    c: Coincident(g3,g2)
    c: Horizontal(g3)
    c: Coincident(g3,g0)
    c: DistanceX(g1,g1) = 11
    c: DistanceY(g2,g2) = 0.8
    c: Coincident(g5,g4)
    c: Horizontal(g5)
    c: Coincident(g6,g5)
    c: Vertical(g6)
    c: Coincident(g7,g6)
    c: Horizontal(g7)
    c: Coincident(g7,g4)
    c: Coincident(g9,g8)
    c: Horizontal(g9)
    c: Coincident(g10,g9)
    c: Vertical(g10)
    c: Coincident(g11,g10)
    c: Horizontal(g11)
    c: Coincident(g11,g8)
    c: Coincident(g13,g12)
    c: Horizontal(g13)
    c: Coincident(g14,g13)
    c: Vertical(g14)
    c: Coincident(g15,g14)
    c: Horizontal(g15)
    c: Coincident(g15,g12)
    c: Coincident(g17,g16)
    c: Horizontal(g17)
    c: Coincident(g18,g17)
    c: Vertical(g18)
    c: Coincident(g19,g18)
    c: Horizontal(g19)
    c: Coincident(g19,g16)
    c: Equal(g3,g19)
    c: Equal(g3,g15)
    c: Equal(g3,g11)
    c: Equal(g3,g7)
    c: Equal(g2,g18)
    c: Equal(g2,g14)
    c: Equal(g2,g10)
    c: Equal(g2,g6)
    c: DistanceY(g-4,g4) = 1
    c: DistanceY(g4,g8) = 1
    c: DistanceY(g8,g12) = 1
    c: DistanceY(g12,g16) = 1
    c: DistanceY(g16,g0) = 1
    c: Tangent(g0,g-5)
    c: Tangent(g16,g-5)
    c: Tangent(g12,g-5)
    c: Tangent(g8,g-5)
    c: Tangent(g4,g-5)
FEATURE [PartDesign::Chamfer] Chamfer009
  Angle = 45
  Base = -> Pad017 [Edge151,Edge154]
  BaseFeature = -> Pad017
  ChamferType = 1
  FlipDirection = false
  Refine = true
  Size = 1.5
  Size2 = 2.8
  SupportTransform = false
  Suppressed = false
  UseAllEdges = false
FEATURE [PartDesign::Pocket] Pocket009
  BaseFeature = -> Chamfer009
  Direction = (0,1,-2e-16)
  Length = 1
  Length2 = 5
  Profile = -> Sketch125
  ReferenceAxis = -> Sketch125 [N_Axis]
  Refine = true
  Suppressed = false
  Type = 0
FEATURE [PartDesign::Pad] Pad014
  BaseFeature = -> Pocket009
  Direction = (0,-1,2e-16)
  Length = 0.8
  Length2 = 10
  Profile = -> Sketch120
  ReferenceAxis = -> Sketch120 [N_Axis]
  Refine = true
  Suppressed = false
  Type = 0
FEATURE [Sketcher::SketchObject] Sketch124
  ArcFitTolerance = 1e-06
  AttachmentSupport = -> [Pad014]
  ExternalGeometry = -> [Binder001]
  FullyConstrained = true
  MakeInternals = false
  MapMode = 5
  Placement = pos=(0,-2.8,6e-16) rot=(1,0,0;1.5708rad)
  sketch-geometry (4):
    g0: LineSegment StartX=-129 StartY=39.2 StartZ=0 EndX=-131.599 EndY=31.2 EndZ=0
    g1: LineSegment StartX=-118 StartY=39.2 StartZ=0 EndX=-120.599 EndY=31.2 EndZ=0
    g2: LineSegment StartX=-129 StartY=39.2 StartZ=0 EndX=-118 EndY=39.2 EndZ=0
    g3: LineSegment StartX=-120.599 StartY=31.2 StartZ=0 EndX=-131.599 EndY=31.2 EndZ=0
  constraints (12):
    c: PointOnObject(g0,g-3)
    c: PointOnObject(g1,g-3)
    c: Parallel(g-4,g0)
    c: Parallel(g-4,g1)
    c: Coincident(g2,g0)
    c: Coincident(g2,g1)
    c: DistanceX(g2,g2) = 11
    c: DistanceY(g1,g1) = 8
    c: Coincident(g3,g1)
    c: Horizontal(g3)
    c: Coincident(g3,g0)
    c: DistanceX(g1,g-3) = 118
FEATURE [PartDesign::Pad] Pad018
  BaseFeature = -> Pad014
  Direction = (0,-1,2e-16)
  Length = 1.2
  Length2 = 10
  Profile = -> Sketch124
  ReferenceAxis = -> Sketch124 [N_Axis]
  Refine = true
  Suppressed = false
  Type = 0
FEATURE [Sketcher::SketchObject] Sketch126
  ArcFitTolerance = 1e-06
  AttachmentSupport = -> [Pad018]
  ExternalGeometry = -> [Pad018]
  FullyConstrained = true
  MakeInternals = false
  MapMode = 5
  Placement = pos=(0,-4,0) rot=(1,0,0;1.5708rad)
  sketch-geometry (8):
    g0: LineSegment StartX=-129.877 StartY=36.5 StartZ=0 EndX=-130.137 EndY=35.7 EndZ=0
    g1: LineSegment StartX=-130.69 StartY=34 StartZ=0 EndX=-130.95 EndY=33.2 EndZ=0
    g2: LineSegment StartX=-129.877 StartY=36.5 StartZ=0 EndX=-118.877 EndY=36.5 EndZ=0
    g3: LineSegment StartX=-130.137 StartY=35.7 StartZ=0 EndX=-119.137 EndY=35.7 EndZ=0
    g4: LineSegment StartX=-130.69 StartY=34 StartZ=0 EndX=-119.69 EndY=34 EndZ=0
    g5: LineSegment StartX=-130.95 StartY=33.2 StartZ=0 EndX=-119.95 EndY=33.2 EndZ=0
    g6: LineSegment StartX=-118.877 StartY=36.5 StartZ=0 EndX=-119.137 EndY=35.7 EndZ=0
    g7: LineSegment StartX=-119.69 StartY=34 StartZ=0 EndX=-119.95 EndY=33.2 EndZ=0
  constraints (20):
    c: Coincident(g2,g0)
    c: Horizontal(g2)
    c: Coincident(g3,g0)
    c: Horizontal(g3)
    c: Coincident(g4,g1)
    c: Horizontal(g4)
    c: Coincident(g5,g1)
    c: Horizontal(g5)
    c: Coincident(g6,g2)
    c: Coincident(g6,g3)
    c: Coincident(g7,g4)
    c: Coincident(g7,g5)
    c: Tangent(g0,g-4)
    c: Tangent(g6,g-5)
    c: Tangent(g1,g-4)
    c: Tangent(g7,g-5)
    c: DistanceY(g3,g2) = 0.8
    c: DistanceY(g5,g4) = 0.8
    c: DistanceY(g-6,g1) = 2
    c: DistanceY(g-6,g0) = 4.5
FEATURE [PartDesign::Chamfer] Chamfer008
  Angle = 45
  Base = -> Pad018 [Edge257]
  BaseFeature = -> Pad018
  ChamferType = 1
  FlipDirection = false
  Refine = true
  Size = 1
  Size2 = 6
  SupportTransform = false
  Suppressed = false
  UseAllEdges = false
FEATURE [PartDesign::Pocket] Pocket010
  BaseFeature = -> Chamfer008
  Direction = (0,1,-2e-16)
  Length = 1
  Length2 = 5
  Profile = -> Sketch126
  ReferenceAxis = -> Sketch126 [N_Axis]
  Refine = true
  Suppressed = false
  Type = 0
FEATURE [PartDesign::Pad] Pad015
  BaseFeature = -> Pocket010
  Direction = (0,-1,2e-16)
  Length = 2
  Length2 = 10
  Profile = -> Sketch121
  ReferenceAxis = -> Sketch121 [N_Axis]
  Refine = true
  Suppressed = false
  Type = 0
FEATURE [PartDesign::Pad] Pad016
  BaseFeature = -> Pad015
  Direction = (0,-1,2e-16)
  Length = 1.6
  Length2 = 10
  Profile = -> Sketch122
  ReferenceAxis = -> Sketch122 [N_Axis]
  Refine = true
  Suppressed = false
  Type = 0
FEATURE [Sketcher::SketchObject] Sketch127
  ArcFitTolerance = 1e-06
  AttachmentSupport = -> [Pad016]
  ExternalGeometry = -> [Pad016]
  FullyConstrained = true
  MakeInternals = false
  MapMode = 5
  Placement = pos=(0,0,-80.4316) rot=(1,0,0;3.14159rad)
  sketch-geometry (8):
    g0: LineSegment StartX=-176.685 StartY=3.6 StartZ=0 EndX=-186.685 EndY=3.6 EndZ=0
    g1: LineSegment [constr] StartX=-186.685 StartY=3.6 StartZ=0 EndX=-186.685 EndY=-9e-16 EndZ=0
    g2: LineSegment StartX=-176.685 StartY=3.6 StartZ=0 EndX=-176.685 EndY=0 EndZ=0
    g3: ArcOfEllipse CenterX=-186.685 CenterY=-9e-16 CenterZ=0 NormalX=0 NormalY=0 NormalZ=1 MajorRadius=10 MinorRadius=3.6 AngleXU=1e-16 StartAngle=0 EndAngle=1.5708
    g4: LineSegment [constr] StartX=-176.685 StartY=-2e-15 StartZ=0 EndX=-196.685 EndY=-2e-15 EndZ=0
    g5: LineSegment [constr] StartX=-186.685 StartY=3.6 StartZ=0 EndX=-186.685 EndY=-3.6 EndZ=0
    g6: GeomPoint [constr] X=-177.356 Y=0 Z=0
    g7: GeomPoint [constr] X=-196.015 Y=-1.9e-15 Z=0
  constraints (13):
    c: Coincident(g0,g-4)
    c: PointOnObject(g0,g-4)
    c: DistanceX(g0,g0) = 10
    c: Coincident(g1,g0)
    c: PointOnObject(g1,g-5)
    c: Vertical(g1)
    c: Coincident(g2,g0)
    c: Coincident(g2,g-5)
    c: InternalAlignment(g4-g7 -> g3) x4
    c: Coincident(g3,g1)
    c: Coincident(g3,g0)
    c: Coincident(g3,g2)
    c: Horizontal(g4)
FEATURE [Sketcher::SketchObject] Sketch128
  ArcFitTolerance = 1e-06
  AttachmentSupport = -> [Pad016]
  ExternalGeometry = -> [Pad016]
  FullyConstrained = true
  MakeInternals = false
  MapMode = 5
  Placement = pos=(0,0,-80.4316) rot=(1,0,0;3.14159rad)
  sketch-geometry (8):
    g0: LineSegment StartX=-215.932 StartY=3.6 StartZ=0 EndX=-215.932 EndY=-1.3e-15 EndZ=0
    g1: LineSegment StartX=-215.932 StartY=3.6 StartZ=0 EndX=-205.932 EndY=3.6 EndZ=0
    g2: LineSegment [constr] StartX=-205.932 StartY=3.6 StartZ=0 EndX=-205.932 EndY=-9e-16 EndZ=0
    g3: ArcOfEllipse CenterX=-205.932 CenterY=-9e-16 CenterZ=0 NormalX=0 NormalY=0 NormalZ=1 MajorRadius=10 MinorRadius=3.6 AngleXU=-3.14159 StartAngle=4.71239 EndAngle=6.28319
    g4: LineSegment [constr] StartX=-215.932 StartY=-1e-15 StartZ=0 EndX=-195.932 EndY=-1e-15 EndZ=0
    g5: LineSegment [constr] StartX=-205.932 StartY=-3.6 StartZ=0 EndX=-205.932 EndY=3.6 EndZ=0
    g6: GeomPoint [constr] X=-215.262 Y=-2e-15 Z=0
    g7: GeomPoint [constr] X=-196.602 Y=-1e-15 Z=0
  constraints (13):
    c: Coincident(g0,g-4)
    c: Coincident(g0,g-5)
    c: Coincident(g1,g0)
    c: PointOnObject(g1,g-3)
    c: DistanceX(g1,g1) = 10
    c: Coincident(g2,g1)
    c: Vertical(g2)
    c: PointOnObject(g2,g-5)
    c: InternalAlignment(g4-g7 -> g3) x4
    c: Coincident(g3,g2)
    c: Coincident(g3,g1)
    c: Coincident(g3,g0)
    c: Horizontal(g4)
FEATURE [PartDesign::SubtractivePipe] SubtractivePipe002
  AuxilleryCurvelinear = true
  AuxillerySpineTangent = false
  BaseFeature = -> Pad016
  Binormal = (0,0,0)
  Mode = 0
  Profile = -> Sketch127
  Refine = true
  Spine = -> Pad016 [Edge254]
  SpineTangent = false
  Suppressed = false
  Transformation = 0
  Transition = 0
FEATURE [PartDesign::SubtractivePipe] SubtractivePipe003
  AuxilleryCurvelinear = true
  AuxillerySpineTangent = false
  BaseFeature = -> SubtractivePipe002
  Binormal = (0,0,0)
  Mode = 0
  Profile = -> Sketch128
  Refine = true
  Spine = -> Pad016 [Edge256,Edge251,Edge252]
  SpineTangent = false
  Suppressed = false
  Transformation = 0
  Transition = 0
FEATURE [Sketcher::SketchObject] Sketch129
  ArcFitTolerance = 1e-06
  AttachmentSupport = -> [Pad016]
  ExternalGeometry = -> [Binder001]
  FullyConstrained = true
  MakeInternals = false
  MapMode = 5
  Placement = pos=(0,-3.6,0) rot=(1,0,0;1.5708rad)
  sketch-geometry (12):
    g0: LineSegment [constr] StartX=-192.176 StartY=-3.18451 StartZ=0 EndX=-181.223 EndY=20.303 EndZ=0
    g1: LineSegment [constr] StartX=-202.765 StartY=20.303 StartZ=0 EndX=-181.223 EndY=20.303 EndZ=0
    g2: LineSegment StartX=-202.765 StartY=20.303 StartZ=0 EndX=-181.223 EndY=20.303 EndZ=0
    g3: LineSegment StartX=-192.176 StartY=-3.18451 StartZ=0 EndX=-196.804 EndY=-13.1107 EndZ=0
    g4: ArcOfCircle CenterX=-207.583 CenterY=4 CenterZ=0 NormalX=0 NormalY=0 NormalZ=1 AngleXU=0 Radius=17 StartAngle=5.84685 EndAngle=7.56663
    g5: ArcOfEllipse CenterX=-181.223 CenterY=8.55923 CenterZ=0 NormalX=0 NormalY=0 NormalZ=1 MajorRadius=23.4779 MinorRadius=11.7437 AngleXU=2e-16 StartAngle=4.71239 EndAngle=7.85398
    g6: LineSegment [constr] StartX=-157.745 StartY=8.55923 StartZ=0 EndX=-204.701 EndY=8.55923 EndZ=0
    g7: LineSegment [constr] StartX=-181.223 StartY=20.303 StartZ=0 EndX=-181.223 EndY=-3.18451 EndZ=0
    g8: GeomPoint [constr] X=-160.894 Y=8.55923 Z=0
    g9: GeomPoint [constr] X=-201.553 Y=8.55923 Z=0
    g10: ArcOfCircle CenterX=-181.223 CenterY=-20.3763 CenterZ=0 NormalX=0 NormalY=0 NormalZ=1 AngleXU=0 Radius=17.1918 StartAngle=1.57079 EndAngle=2.70526
    g11: GeomPoint [constr] X=-181.223 Y=-3.18451 Z=0
  constraints (23):
    c: Coincident(g0,g-5)
    c: Coincident(g1,g-6)
    c: Horizontal(g1)
    c: Coincident(g1,g0)
    c: Parallel(g0,g-4)
    c: Coincident(g2,g1)
    c: Coincident(g2,g0)
    c: Coincident(g3,g0)
    c: Equal(g4,g-5)
    c: Coincident(g4,g1)
    c: Coincident(g4,g0)
    c: InternalAlignment(g6-g9 -> g5) x4
    c: Vertical(g5,g0)
    c: Horizontal(g6)
    c: Coincident(g5,g0)
    c: DistanceX(g6,g-3) = 10.1
    c: Tangent(g10,g3) = -1.5708
    c: PointOnObject(g11,g10)
    c: Tangent(g5,g10,g11) = 1.5708
    c: Coincident(g10,g5)
    c: Coincident(g11,g7)
    c: Parallel(g3,g-4)
    c: Horizontal(g5,g0)
FEATURE [Sketcher::SketchObject] Sketch130
  ArcFitTolerance = 1e-06
  AttachmentOffset = pos=(0,0,-1.6) rot=(0,0,1;0rad)
  AttachmentSupport = -> [Pad016]
  ExternalGeometry = -> [Binder001]
  FullyConstrained = true
  MakeInternals = false
  MapMode = 5
  Placement = pos=(0,-2,-4e-16) rot=(1,0,0;1.5708rad)
  sketch-geometry (12):
    g0: LineSegment [constr] StartX=-192.176 StartY=-3.18451 StartZ=0 EndX=-181.223 EndY=20.303 EndZ=0
    g1: LineSegment [constr] StartX=-202.765 StartY=20.303 StartZ=0 EndX=-181.223 EndY=20.303 EndZ=0
    g2: LineSegment StartX=-202.765 StartY=20.303 StartZ=0 EndX=-181.223 EndY=20.303 EndZ=0
    g3: LineSegment StartX=-192.176 StartY=-3.18451 StartZ=0 EndX=-193.827 EndY=-6.72678 EndZ=0
    g4: ArcOfCircle CenterX=-207.583 CenterY=4 CenterZ=0 NormalX=0 NormalY=0 NormalZ=1 AngleXU=0 Radius=17 StartAngle=5.84685 EndAngle=7.56663
    g5: ArcOfEllipse CenterX=-181.223 CenterY=10.803 CenterZ=0 NormalX=0 NormalY=0 NormalZ=1 MajorRadius=14.4779 MinorRadius=9.5 AngleXU=0 StartAngle=4.71239 EndAngle=7.85398
    g6: LineSegment [constr] StartX=-166.745 StartY=10.803 StartZ=0 EndX=-195.701 EndY=10.803 EndZ=0
    g7: LineSegment [constr] StartX=-181.223 StartY=20.303 StartZ=0 EndX=-181.223 EndY=1.30297 EndZ=0
    g8: GeomPoint [constr] X=-170.298 Y=10.803 Z=0
    g9: GeomPoint [constr] X=-192.148 Y=10.803 Z=0
    g10: ArcOfCircle CenterX=-181.223 CenterY=-12.6042 CenterZ=0 NormalX=0 NormalY=0 NormalZ=1 AngleXU=0 Radius=13.9072 StartAngle=1.5708 EndAngle=2.70526
    g11: GeomPoint [constr] X=-181.223 Y=1.30297 Z=0
  constraints (23):
    c: Coincident(g0,g-5)
    c: Coincident(g1,g-6)
    c: Horizontal(g1)
    c: Coincident(g1,g0)
    c: Parallel(g0,g-4)
    c: Coincident(g2,g1)
    c: Coincident(g2,g0)
    c: Coincident(g3,g0)
    c: Equal(g4,g-5)
    c: Coincident(g4,g1)
    c: Coincident(g4,g0)
    c: InternalAlignment(g6-g9 -> g5) x4
    c: Vertical(g5,g0)
    c: Horizontal(g6)
    c: Coincident(g5,g0)
    c: DistanceX(g6,g-3) = 19.1
    c: Tangent(g10,g3) = -1.5708
    c: PointOnObject(g11,g10)
    c: Tangent(g5,g10,g11) = 1.5708
    c: Coincident(g10,g5)
    c: Coincident(g11,g7)
    c: Parallel(g3,g-4)
    c: DistanceY(g5,g0) = 19
FEATURE [Part::Part2DObjectPython] Clone2D001  label="Sketch130 (2D)"  # Draft 2D object (typed FeaturePython)
  Fuse = false
  Objects = -> [Sketch130]
  Placement = pos=(0,-2,-4e-16) rot=(1,0,0;1.5708rad)
  Scale = (1,1,1)
FEATURE [Sketcher::SketchObject] Sketch131
  ArcFitTolerance = 1e-06
  AttachmentOffset = pos=(0,0,-3.5) rot=(0,0,1;0rad)
  AttachmentSupport = -> [Pad016]
  ExternalGeometry = -> [Binder001]
  FullyConstrained = true
  MakeInternals = false
  MapMode = 5
  Placement = pos=(0,-0.1,-8e-16) rot=(1,0,0;1.5708rad)
  sketch-geometry (1):
    g0: GeomPoint X=-197.47 Y=8.55923 Z=0
  constraints (1):
    c: Symmetric(g-6,g-4,g0)
FEATURE [PartDesign::SubtractiveLoft] SubtractiveLoft002
  BaseFeature = -> SubtractivePipe003
  Closed = false
  Profile = -> Sketch129
  Refine = true
  Ruled = false
  Sections = -> [Sketch130]
  Suppressed = false
FEATURE [PartDesign::SubtractiveLoft] SubtractiveLoft003
  BaseFeature = -> SubtractiveLoft002
  Closed = false
  Profile = -> Clone2D001
  Refine = true
  Ruled = false
  Sections = -> [Sketch131]
  Suppressed = false
FEATURE [PartDesign::Chamfer] Chamfer010
  Angle = 45
  Base = -> SubtractiveLoft003 [Edge200,Edge201,Edge203,Edge202,Edge194]
  BaseFeature = -> SubtractiveLoft003
  ChamferType = 0
  FlipDirection = false
  Refine = true
  Size = 1.5
  Size2 = 1
  SupportTransform = false
  Suppressed = false
  UseAllEdges = false
FEATURE [PartDesign::Chamfer] Chamfer011
  Angle = 45
  Base = -> Chamfer010 [Edge15]
  BaseFeature = -> Chamfer010
  ChamferType = 0
  FlipDirection = false
  Refine = true
  Size = 1.6
  Size2 = 1
  SupportTransform = false
  Suppressed = false
  UseAllEdges = false
FEATURE [PartDesign::Chamfer] Chamfer012
  Angle = 45
  Base = -> Chamfer011 [Edge10]
  BaseFeature = -> Chamfer011
  ChamferType = 0
  FlipDirection = false
  Refine = true
  Size = 3.5
  Size2 = 1
  SupportTransform = false
  Suppressed = false
  UseAllEdges = false
FEATURE [PartDesign::Chamfer] Chamfer013
  Angle = 45
  Base = -> Chamfer012 [Edge145,Edge94]
  BaseFeature = -> Chamfer012
  ChamferType = 0
  FlipDirection = false
  Refine = true
  Size = 1.9
  Size2 = 1
  SupportTransform = false
  Suppressed = false
  UseAllEdges = false
FEATURE [Sketcher::SketchObject] Sketch132
  ArcFitTolerance = 1e-06
  AttachmentSupport = -> [Pad016]
  ExternalGeometry = -> [Binder001]
  FullyConstrained = true
  MakeInternals = false
  MapMode = 5
  Placement = pos=(0,-3.6,0) rot=(1,0,0;1.5708rad)
  sketch-geometry (3):
    g0: LineSegment [constr] StartX=-215.42 StartY=-53.0314 StartZ=0 EndX=-167.782 EndY=-53.0314 EndZ=0
    g1: Circle CenterX=-191.282 CenterY=-53.0314 CenterZ=0 NormalX=0 NormalY=0 NormalZ=1 AngleXU=0 Radius=11.5
    g2: Circle CenterX=-191.282 CenterY=-53.0314 CenterZ=0 NormalX=0 NormalY=0 NormalZ=1 AngleXU=0 Radius=10.7
  constraints (8):
    c: Coincident(g0,g-3)
    c: PointOnObject(g0,g-4)
    c: Horizontal(g0)
    c: Diameter(g1) = 23
    c: PointOnObject(g1,g0)
    c: DistanceX(g1,g0) = 23.5
    c: Diameter(g2) = 21.4
    c: Coincident(g2,g1)
FEATURE [PartDesign::Fillet] Fillet007
  Base = -> Chamfer013 [Edge83]
  BaseFeature = -> Chamfer013
  Radius = 1.1
  Refine = true
  SupportTransform = false
  Suppressed = false
  UseAllEdges = false
FEATURE [PartDesign::Fillet] Fillet008
  Base = -> Fillet007 [Edge76]
  BaseFeature = -> Fillet007
  Radius = 1.9
  Refine = true
  SupportTransform = false
  Suppressed = false
  UseAllEdges = false
FEATURE [PartDesign::Pocket] Pocket011
  BaseFeature = -> Fillet008
  Direction = (0,1,-2e-16)
  Length = 0.8
  Length2 = 5
  Profile = -> Sketch132
  ReferenceAxis = -> Sketch132 [N_Axis]
  Refine = true
  Suppressed = false
  Type = 0
FEATURE [Part::Part2DObjectPython] ShapeString  # Draft 2D object (typed FeaturePython)
  FontFile = <path>
  Fuse = false
  Justification = 6
  JustificationReference = 0
  KeepLeftMargin = false
  MakeFace = true
  ObliqueAngle = 0
  Placement = pos=(-199,-3.6,-57.5) rot=(1,0,0;1.5708rad)
  ScaleToSize = true
  Size = 10
  String = AS
  Tracking = 0
FEATURE [PartDesign::Pocket] Pocket012
  BaseFeature = -> Pocket011
  Direction = (0,1,0)
  Length = 1
  Length2 = 5
  Profile = -> ShapeString
  ReferenceAxis = -> ShapeString [N_Axis]
  Refine = true
  Suppressed = false
  Type = 0
FEATURE [PartDesign::Body] Body007  label="lato DX"
  AllowCompound = false
  Group = -> [Binder001,Sketch114,Pad011,Chamfer014,Sketch115,Pocket006,Sketch116,Pad012,Sketch117,Pocket007,Sketch118,Pad013,Sketch119,Pocket008,Pad017,Chamfer009,Pocket009,Sketch123,Sketch120,Pad014,Pad018,Chamfer008,Pocket010,Sketch121,Pad015,Sketch122,Pad016,Sketch124,Sketch125,Sketch126,Sketch127,Sketch128,SubtractivePipe002,SubtractivePipe003,Sketch129,Sketch130,Clone2D001,Sketch131,SubtractiveLoft002,+11 more]
  Origin = -> Origin007
  Tip = -> Pocket012
FEATURE [Sketcher::SketchObject] Sketch133
  ArcFitTolerance = 1e-06
  AttachmentSupport = -> [Binder]
  ExternalGeometry = -> [Binder]
  FullyConstrained = true
  MakeInternals = false
  MapMode = 5
  Placement = pos=(0,9e-16,0) rot=(0,0.707107,0.707107;3.14159rad)
  sketch-geometry (30):
    g0: LineSegment StartX=0 StartY=39.2 StartZ=0 EndX=0 EndY=3.2 EndZ=0
    g1: LineSegment StartX=0 StartY=3.2 StartZ=0 EndX=82.8 EndY=3.2 EndZ=0
    g2: LineSegment StartX=82.8 StartY=3.2 StartZ=0 EndX=82.8 EndY=6.2 EndZ=0
    g3: LineSegment StartX=82.8 StartY=6.2 StartZ=0 EndX=91.752 EndY=6.2 EndZ=0
    g4: LineSegment StartX=0 StartY=39.2 StartZ=0 EndX=195.887 EndY=39.2 EndZ=0
    g5: LineSegment StartX=195.887 StartY=39.2 StartZ=0 EndX=202.765 EndY=20.303 EndZ=0
    g6: LineSegment StartX=192.333 StartY=24.9893 StartZ=0 EndX=196.467 EndY=26.4942 EndZ=0
    g7: LineSegment StartX=196.467 StartY=26.4942 StartZ=0 EndX=194.073 EndY=33.0721 EndZ=0
    g8: LineSegment StartX=194.073 StartY=33.0721 StartZ=0 EndX=189.939 EndY=31.5672 EndZ=0
    g9: LineSegment StartX=189.939 StartY=31.5672 StartZ=0 EndX=192.333 EndY=24.9893 EndZ=0
    g10: ArcOfCircle CenterX=107.6 CenterY=4 CenterZ=0 NormalX=0 NormalY=0 NormalZ=1 AngleXU=0 Radius=16 StartAngle=1.5708 EndAngle=3.00366
    g11: LineSegment StartX=107.6 StartY=20 StartZ=0 EndX=132.428 EndY=20 EndZ=0
    g12: ArcOfCircle [constr] CenterX=132.428 CenterY=4 CenterZ=0 NormalX=0 NormalY=0 NormalZ=1 AngleXU=0 Radius=16 StartAngle=0.314159 EndAngle=1.5708
    g13: LineSegment StartX=147.645 StartY=8.94427 StartZ=0 EndX=176.685 EndY=-80.4316 EndZ=0
    g14: LineSegment StartX=176.685 StartY=-80.4316 StartZ=0 EndX=215.932 EndY=-80.4316 EndZ=0
    g15: ArcOfCircle CenterX=207.583 CenterY=4 CenterZ=0 NormalX=0 NormalY=0 NormalZ=1 AngleXU=0 Radius=17 StartAngle=1.85815 EndAngle=3.57792
    g16: ArcOfCircle CenterX=184.801 CenterY=-67.3089 CenterZ=0 NormalX=0 NormalY=0 NormalZ=1 AngleXU=0 Radius=33.7833 StartAngle=5.88425 EndAngle=6.71952
    g17: LineSegment StartX=192.176 StartY=-3.18451 StartZ=0 EndX=215.42 EndY=-53.0314 EndZ=0
    g18: Circle CenterX=5.6 CenterY=34.8 CenterZ=0 NormalX=0 NormalY=0 NormalZ=1 AngleXU=0 Radius=1.8
    g19: Circle CenterX=5.6 CenterY=7.6 CenterZ=0 NormalX=0 NormalY=0 NormalZ=1 AngleXU=0 Radius=1.8
    g20: Circle CenterX=78.51 CenterY=34.8 CenterZ=0 NormalX=0 NormalY=0 NormalZ=1 AngleXU=0 Radius=1.8
    g21: Circle CenterX=78.51 CenterY=7.6 CenterZ=0 NormalX=0 NormalY=0 NormalZ=1 AngleXU=0 Radius=1.8
    g22: Circle CenterX=184.08 CenterY=34.8 CenterZ=0 NormalX=0 NormalY=0 NormalZ=1 AngleXU=0 Radius=1.8
    g23: Circle CenterX=179.305 CenterY=-76.8316 CenterZ=0 NormalX=0 NormalY=0 NormalZ=1 AngleXU=0 Radius=1.8
    g24: Circle CenterX=213.443 CenterY=-76.8316 CenterZ=0 NormalX=0 NormalY=0 NormalZ=1 AngleXU=0 Radius=1.8
    g25: Circle CenterX=19 CenterY=21.2 CenterZ=0 NormalX=0 NormalY=0 NormalZ=1 AngleXU=0 Radius=6.3
    g26: Circle CenterX=42 CenterY=21.2 CenterZ=0 NormalX=0 NormalY=0 NormalZ=1 AngleXU=0 Radius=6.3
    g27: Circle CenterX=65 CenterY=21.2 CenterZ=0 NormalX=0 NormalY=0 NormalZ=1 AngleXU=0 Radius=6.3
    g28: LineSegment StartX=132.428 StartY=20 StartZ=0 EndX=144.053 EndY=20 EndZ=0
    g29: LineSegment StartX=147.645 StartY=8.94427 StartZ=0 EndX=144.053 EndY=20 EndZ=0
  constraints (65):
    c: Coincident(g0,g-4)
    c: Coincident(g0,g-5)
    c: Coincident(g1,g0)
    c: Coincident(g1,g-6)
    c: Coincident(g2,g1)
    c: Coincident(g2,g-7)
    c: Coincident(g3,g2)
    c: Coincident(g3,g-8)
    c: Coincident(g4,g0)
    c: Coincident(g4,g-16)
    c: Coincident(g5,g4)
    c: Coincident(g5,g-16)
    c: Coincident(g6,g-20)
    c: Coincident(g6,g-21)
    c: Coincident(g7,g6)
    c: Coincident(g7,g-23)
    c: Coincident(g8,g7)
    c: Coincident(g8,g-22)
    c: Coincident(g9,g8)
    c: Coincident(g9,g6)
    c: Equal(g10,g-8)
    c: Coincident(g10,g3)
    c: Coincident(g10,g-9)
    c: Coincident(g11,g10)
    c: Coincident(g11,g-10)
    c: Equal(g12,g-10)
    c: Coincident(g12,g11)
    c: Coincident(g12,g-11)
    c: Coincident(g13,g12)
    c: Coincident(g13,g-12)
    c: Coincident(g14,g13)
    c: Coincident(g14,g-13)
    c: Equal(g15,g-15)
    c: Coincident(g15,g5)
    c: Coincident(g15,g-15)
    c: Equal(g16,g-13)
    c: Coincident(g16,g14)
    c: Coincident(g16,g-14)
    c: Coincident(g17,g15)
    c: Coincident(g17,g16)
    c: Equal(g18,g-28)
    c: Equal(g19,g-29)
    c: Equal(g20,g-26)
    c: Equal(g21,g-27)
    c: Equal(g22,g-17)
    c: Equal(g24,g-25)
    c: Equal(g23,g-24)
    c: Coincident(g23,g-24)
    c: Coincident(g24,g-25)
    c: Coincident(g22,g-17)
    c: Coincident(g20,g-26)
    c: Coincident(g21,g-27)
    c: Coincident(g18,g-28)
    c: Coincident(g19,g-29)
    c: Equal(g25,g-30)
    c: Equal(g26,g-31)
    c: Equal(g27,g-32)
    c: Coincident(g25,g-30)
    c: Coincident(g26,g-31)
    c: Coincident(g27,g-32)
    c: Parallel(g28,g11)
    c: Parallel(g29,g13)
    c: Coincident(g28,g11)
    c: Coincident(g29,g12)
    c: Coincident(g29,g28)
FEATURE [PartDesign::Pad] Pad019
  Direction = (0,1,-2e-16)
  Length = 2
  Length2 = 10
  Profile = -> Sketch133
  ReferenceAxis = -> Sketch133 [N_Axis]
  Refine = true
  Suppressed = false
  Type = 0
FEATURE [Sketcher::SketchObject] Sketch091  label="Sketch091 - forma anteriore"
  ArcFitTolerance = 1e-06
  AttachmentSupport = -> [Pad019]
  ExternalGeometry = -> [Binder]
  FullyConstrained = true
  MakeInternals = false
  MapMode = 5
  Placement = pos=(0,2,0) rot=(0,0.707107,0.707107;3.14159rad)
  sketch-geometry (12):
    g0: Circle CenterX=5.6 CenterY=34.8 CenterZ=0 NormalX=0 NormalY=0 NormalZ=1 AngleXU=0 Radius=1.8
    g1: Circle CenterX=5.6 CenterY=7.6 CenterZ=0 NormalX=0 NormalY=0 NormalZ=1 AngleXU=0 Radius=1.8
    g2: Circle CenterX=78.51 CenterY=34.8 CenterZ=0 NormalX=0 NormalY=0 NormalZ=1 AngleXU=0 Radius=1.8
    g3: Circle CenterX=78.51 CenterY=7.6 CenterZ=0 NormalX=0 NormalY=0 NormalZ=1 AngleXU=0 Radius=1.8
    g4: LineSegment StartX=0 StartY=39.2 StartZ=0 EndX=0 EndY=3.2 EndZ=0
    g5: LineSegment StartX=0 StartY=3.2 StartZ=0 EndX=82.8 EndY=3.2 EndZ=0
    g6: LineSegment StartX=82.8 StartY=3.2 StartZ=0 EndX=82.8 EndY=39.2 EndZ=0
    g7: LineSegment StartX=82.8 StartY=39.2 StartZ=0 EndX=0 EndY=39.2 EndZ=0
    g8: ArcOfCircle CenterX=19 CenterY=21.2 CenterZ=0 NormalX=0 NormalY=0 NormalZ=1 AngleXU=0 Radius=10 StartAngle=1.5708 EndAngle=4.71239
    g9: ArcOfCircle CenterX=65 CenterY=21.2 CenterZ=0 NormalX=0 NormalY=0 NormalZ=1 AngleXU=0 Radius=10 StartAngle=4.71239 EndAngle=7.85398
    g10: LineSegment StartX=19 StartY=31.2 StartZ=0 EndX=65 EndY=31.2 EndZ=0
    g11: LineSegment StartX=19 StartY=11.2 StartZ=0 EndX=65 EndY=11.2 EndZ=0
  constraints (25):
    c: Equal(g2,g-7)
    c: Equal(g3,g-8)
    c: Equal(g1,g-13)
    c: Equal(g0,g-12)
    c: Coincident(g0,g-12)
    c: Coincident(g1,g-13)
    c: Coincident(g3,g-8)
    c: Coincident(g2,g-7)
    c: Coincident(g4,g-4)
    c: Coincident(g4,g-5)
    c: Coincident(g5,g4)
    c: Coincident(g5,g-6)
    c: Coincident(g6,g5)
    c: PointOnObject(g6,g-3)
    c: Vertical(g6)
    c: Coincident(g7,g6)
    c: Coincident(g7,g4)
    c: Tangent(g8,g10) = 1.5708
    c: Tangent(g8,g11) = -1.5708
    c: Tangent(g9,g10) = 1.5708
    c: Tangent(g9,g11) = -1.5708
    c: Equal(g8,g9)
    c: Radius(g8) = 10
    c: Coincident(g8,g-11)
    c: Coincident(g9,g-9)
FEATURE [Sketcher::SketchObject] Sketch093  label="Sketch093 - scavi interni pulsanti"
  ArcFitTolerance = 1e-06
  AttachmentSupport = -> [Pad019]
  ExternalGeometry = -> [Binder]
  FullyConstrained = true
  MakeInternals = false
  MapMode = 5
  Placement = pos=(0,1.8e-15,0) rot=(1,0,0;1.5708rad)
  sketch-geometry (3):
    g0: Circle CenterX=-65 CenterY=21.2 CenterZ=0 NormalX=0 NormalY=0 NormalZ=1 AngleXU=0 Radius=7.3
    g1: Circle CenterX=-42 CenterY=21.2 CenterZ=0 NormalX=0 NormalY=0 NormalZ=1 AngleXU=0 Radius=7.3
    g2: Circle CenterX=-19 CenterY=21.2 CenterZ=0 NormalX=0 NormalY=0 NormalZ=1 AngleXU=0 Radius=7.3
  constraints (6):
    c: Coincident(g0,g-3)
    c: Coincident(g1,g-4)
    c: Coincident(g2,g-5)
    c: Diameter(g0) = 14.6
    c: Diameter(g1) = 14.6
    c: Diameter(g2) = 14.6
FEATURE [Sketcher::SketchObject] Sketch094  label="Sketch094 - forma centrale"
  ArcFitTolerance = 1e-06
  AttachmentSupport = -> [Pad019]
  ExternalGeometry = -> [Binder]
  FullyConstrained = true
  MakeInternals = false
  MapMode = 5
  Placement = pos=(0,2,0) rot=(0,0.707107,0.707107;3.14159rad)
  sketch-geometry (4):
    g0: LineSegment StartX=137.815 StartY=39.2 StartZ=0 EndX=142.655 EndY=24.303 EndZ=0
    g1: LineSegment StartX=110.815 StartY=24.303 StartZ=0 EndX=142.655 EndY=24.303 EndZ=0
    g2: LineSegment StartX=137.815 StartY=39.2 StartZ=0 EndX=110.815 EndY=39.2 EndZ=0
    g3: ArcOfCircle CenterX=92.2534 CenterY=31.7515 CenterZ=0 NormalX=0 NormalY=0 NormalZ=1 AngleXU=0 Radius=20 StartAngle=5.90156 EndAngle=6.66481
  constraints (12):
    c: PointOnObject(g0,g-3)
    c: Tangent(g0,g-5)
    c: Horizontal(g1)
    c: Coincident(g1,g0)
    c: Coincident(g2,g0)
    c: PointOnObject(g2,g-3)
    c: DistanceX(g2,g2) = 27
    c: Vertical(g1,g2)
    c: Coincident(g3,g2)
    c: Radius(g3) = 20
    c: Coincident(g3,g1)
    c: DistanceY(g-6,g0) = 4
FEATURE [Sketcher::SketchObject] Sketch095  label="Sketch095 - forma posteriore"
  ArcFitTolerance = 1e-06
  AttachmentSupport = -> [Pad019]
  ExternalGeometry = -> [Binder]
  FullyConstrained = true
  MakeInternals = false
  MapMode = 5
  Placement = pos=(0,2,0) rot=(0,0.707107,0.707107;3.14159rad)
  sketch-geometry (15):
    g0: LineSegment StartX=137.815 StartY=39.2 StartZ=0 EndX=143.955 EndY=20.303 EndZ=0
    g1: LineSegment StartX=143.955 StartY=20.303 StartZ=0 EndX=190.141 EndY=20.303 EndZ=0
    g2: ArcOfCircle CenterX=184.08 CenterY=34.8 CenterZ=0 NormalX=0 NormalY=0 NormalZ=1 AngleXU=0 Radius=3.5 StartAngle=3.49066 EndAngle=4.71239
    g3: LineSegment StartX=180.791 StartY=33.6029 StartZ=0 EndX=178.754 EndY=39.2 EndZ=0
    g4: LineSegment StartX=184.08 StartY=31.3 StartZ=0 EndX=186.139 EndY=31.3 EndZ=0
    g5: LineSegment StartX=190.141 StartY=20.303 StartZ=0 EndX=186.139 EndY=31.3 EndZ=0
    g6: LineSegment StartX=137.815 StartY=39.2 StartZ=0 EndX=156.815 EndY=39.2 EndZ=0
    g7: LineSegment StartX=178.754 StartY=39.2 StartZ=0 EndX=168.815 EndY=39.2 EndZ=0
    g8: LineSegment StartX=156.815 StartY=31.2 StartZ=0 EndX=168.815 EndY=31.2 EndZ=0
    g9: ArcOfCircle CenterX=176.411 CenterY=35.2 CenterZ=0 NormalX=0 NormalY=0 NormalZ=1 AngleXU=0 Radius=20 StartAngle=2.94023 EndAngle=3.34295
    g10: ArcOfCircle CenterX=188.411 CenterY=35.2 CenterZ=0 NormalX=0 NormalY=0 NormalZ=1 AngleXU=0 Radius=20 StartAngle=2.94023 EndAngle=3.34295
    g11: LineSegment StartX=157.815 StartY=39.2 StartZ=0 EndX=167.815 EndY=39.2 EndZ=0
    g12: LineSegment StartX=157.436 StartY=36.2 StartZ=0 EndX=167.436 EndY=36.2 EndZ=0
    g13: ArcOfCircle CenterX=177.411 CenterY=35.2 CenterZ=0 NormalX=0 NormalY=0 NormalZ=1 AngleXU=0 Radius=20 StartAngle=2.94023 EndAngle=3.09157
    g14: ArcOfCircle CenterX=187.411 CenterY=35.2 CenterZ=0 NormalX=0 NormalY=0 NormalZ=1 AngleXU=0 Radius=20 StartAngle=2.94023 EndAngle=3.09157
  constraints (46):
    c: PointOnObject(g0,g-3)
    c: Tangent(g0,g-6)
    c: Coincident(g1,g0)
    c: Horizontal(g1)
    c: Radius(g2) = 3.5
    c: Coincident(g2,g-5)
    c: PointOnObject(g3,g-3)
    c: Parallel(g3,g-4)
    c: Tangent(g3,g2) = 1.5708
    c: Horizontal(g4)
    c: Tangent(g4,g2) = -1.5708
    c: Coincident(g5,g1)
    c: Parallel(g5,g-4)
    c: Coincident(g5,g4)
    c: DistanceX(g4,g-8) = 3.8
    c: Coincident(g6,g0)
    c: PointOnObject(g6,g-3)
    c: Coincident(g7,g3)
    c: PointOnObject(g7,g-3)
    c: Horizontal(g8)
    c: DistanceX(g6,g7) = 12
    c: Vertical(g8,g6)
    c: Vertical(g7,g8)
    c: DistanceY(g8,g6) = 8
    c: Coincident(g9,g8)
    c: Coincident(g9,g6)
    c: Coincident(g10,g7)
    c: Coincident(g10,g8)
    c: Radius(g9) = 20
    c: Radius(g10) = 20
    c: PointOnObject(g11,g-3)
    c: PointOnObject(g11,g-3)
    c: DistanceX(g11,g11) = 10
    c: DistanceX(g6,g11) = 1
    c: Horizontal(g12)
    c: Equal(g12,g11)
    c: DistanceY(g12,g11) = 3
    c: Coincident(g13,g11)
    c: Coincident(g13,g12)
    c: Radius(g13) = 20
    c: Coincident(g14,g11)
    c: Coincident(g14,g12)
    c: Radius(g14) = 20
    c: DistanceX(g0,g6) = 19
    c: Horizontal(g9,g13)
    c: Horizontal(g0,g-4)
FEATURE [Sketcher::SketchObject] Sketch096  label="Sketch096 - forma impugnatura"
  ArcFitTolerance = 1e-06
  AttachmentSupport = -> [Pad019]
  ExternalGeometry = -> [Binder]
  FullyConstrained = true
  MakeInternals = false
  MapMode = 5
  Placement = pos=(0,2,0) rot=(0,0.707107,0.707107;3.14159rad)
  sketch-geometry (8):
    g0: LineSegment StartX=176.685 StartY=-80.4316 StartZ=0 EndX=143.955 EndY=20.303 EndZ=0
    g1: LineSegment StartX=176.685 StartY=-80.4316 StartZ=0 EndX=215.932 EndY=-80.4316 EndZ=0
    g2: Circle CenterX=179.305 CenterY=-76.8316 CenterZ=0 NormalX=0 NormalY=0 NormalZ=1 AngleXU=0 Radius=3
    g3: Circle CenterX=213.443 CenterY=-76.8316 CenterZ=0 NormalX=0 NormalY=0 NormalZ=1 AngleXU=0 Radius=3
    g4: LineSegment StartX=143.955 StartY=20.303 StartZ=0 EndX=202.765 EndY=20.303 EndZ=0
    g5: LineSegment StartX=215.42 StartY=-53.0314 StartZ=0 EndX=192.176 EndY=-3.18451 EndZ=0
    g6: ArcOfCircle CenterX=184.801 CenterY=-67.3089 CenterZ=0 NormalX=0 NormalY=0 NormalZ=1 AngleXU=0 Radius=33.7833 StartAngle=5.88425 EndAngle=6.71952
    g7: ArcOfCircle CenterX=207.583 CenterY=4 CenterZ=0 NormalX=0 NormalY=0 NormalZ=1 AngleXU=0 Radius=17 StartAngle=1.85815 EndAngle=3.57792
  constraints (19):
    c: Coincident(g0,g-4)
    c: PointOnObject(g0,g-3)
    c: Horizontal(g0,g-7)
    c: Coincident(g1,g0)
    c: Coincident(g1,g-5)
    c: Diameter(g2) = 6
    c: Diameter(g3) = 6
    c: Coincident(g2,g-9)
    c: Coincident(g3,g-10)
    c: Coincident(g4,g0)
    c: Coincident(g5,g-6)
    c: Coincident(g6,g1)
    c: Coincident(g6,g5)
    c: Equal(g-5,g6)
    c: Coincident(g5,g-7)
    c: Coincident(g4,g-7)
    c: Tangent(g7,g-7)
    c: Coincident(g7,g4)
    c: Coincident(g7,g5)
FEATURE [Sketcher::SketchObject] Sketch097
  ArcFitTolerance = 1e-06
  AttachmentSupport = -> [Pad019]
  ExternalGeometry = -> [Binder]
  FullyConstrained = true
  MakeInternals = false
  MapMode = 5
  Placement = pos=(0,2,0) rot=(0,0.707107,0.707107;3.14159rad)
  sketch-geometry (4):
    g0: LineSegment StartX=90 StartY=36.8 StartZ=0 EndX=108 EndY=36.8 EndZ=0
    g1: LineSegment StartX=108 StartY=36.8 StartZ=0 EndX=108 EndY=26.8 EndZ=0
    g2: LineSegment StartX=108 StartY=26.8 StartZ=0 EndX=90 EndY=26.8 EndZ=0
    g3: ArcOfCircle CenterX=94 CenterY=31.8 CenterZ=0 NormalX=0 NormalY=0 NormalZ=1 AngleXU=0 Radius=6.40312 StartAngle=2.24554 EndAngle=4.03765
  constraints (13):
    c: Horizontal(g0)
    c: Coincident(g1,g0)
    c: Vertical(g1)
    c: DistanceX(g0,g0) = 18
    c: DistanceY(g1,g1) = 10
    c: Coincident(g2,g1)
    c: Horizontal(g2)
    c: Equal(g2,g0)
    c: DistanceY(g0,g-3) = 2.4
    c: Coincident(g3,g0)
    c: Coincident(g3,g2)
    c: DistanceX(g2,g3) = 4
    c: DistanceX(g-3,g0) = 90
FEATURE [PartDesign::Chamfer] Chamfer015
  Angle = 45
  Base = -> Pad019 [Edge19,Edge22,Edge79]
  BaseFeature = -> Pad019
  ChamferType = 0
  FlipDirection = false
  Refine = true
  Size = 1.9
  Size2 = 1
  SupportTransform = false
  Suppressed = false
  UseAllEdges = false
FEATURE [PartDesign::Pocket] Pocket002
  BaseFeature = -> Chamfer015
  Direction = (0,1,-2e-16)
  Length = 1.2
  Length2 = 5
  Profile = -> Sketch093
  ReferenceAxis = -> Sketch093 [N_Axis]
  Refine = true
  Suppressed = false
  Type = 0
FEATURE [PartDesign::Pad] Pad005
  BaseFeature = -> Pocket002
  Direction = (0,1,-2e-16)
  Length = 1.6
  Length2 = 10
  Profile = -> Sketch091
  ReferenceAxis = -> Sketch091 [N_Axis]
  Refine = true
  Suppressed = false
  Type = 0
FEATURE [Sketcher::SketchObject] Sketch092  label="Sketch092 - scavi per viti anteriori"
  ArcFitTolerance = 1e-06
  AttachmentSupport = -> [Pad005]
  ExternalGeometry = -> [Binder]
  FullyConstrained = true
  MakeInternals = false
  MapMode = 5
  Placement = pos=(0,3.6,0) rot=(0,0.707107,0.707107;3.14159rad)
  sketch-geometry (20):
    g0: ArcOfCircle CenterX=5.6 CenterY=7.6 CenterZ=0 NormalX=0 NormalY=0 NormalZ=1 AngleXU=0 Radius=3.5 StartAngle=0 EndAngle=1.5708
    g1: ArcOfCircle CenterX=5.6 CenterY=34.8 CenterZ=0 NormalX=0 NormalY=0 NormalZ=1 AngleXU=0 Radius=3.5 StartAngle=4.71239 EndAngle=6.28319
    g2: ArcOfCircle CenterX=78.51 CenterY=34.8 CenterZ=0 NormalX=0 NormalY=0 NormalZ=1 AngleXU=0 Radius=3.5 StartAngle=3.14159 EndAngle=4.71239
    g3: ArcOfCircle CenterX=78.51 CenterY=7.6 CenterZ=0 NormalX=0 NormalY=0 NormalZ=1 AngleXU=0 Radius=3.5 StartAngle=1.5708 EndAngle=3.14159
    g4: LineSegment StartX=0 StartY=3.2 StartZ=0 EndX=0 EndY=11.1 EndZ=0
    g5: LineSegment StartX=0 StartY=11.1 StartZ=0 EndX=5.6 EndY=11.1 EndZ=0
    g6: LineSegment StartX=0 StartY=3.2 StartZ=0 EndX=9.1 EndY=3.2 EndZ=0
    g7: LineSegment StartX=9.1 StartY=3.2 StartZ=0 EndX=9.1 EndY=7.6 EndZ=0
    g8: LineSegment StartX=0 StartY=39.2 StartZ=0 EndX=0 EndY=31.3 EndZ=0
    g9: LineSegment StartX=0 StartY=31.3 StartZ=0 EndX=5.6 EndY=31.3 EndZ=0
    g10: LineSegment StartX=0 StartY=39.2 StartZ=0 EndX=9.1 EndY=39.2 EndZ=0
    g11: LineSegment StartX=9.1 StartY=39.2 StartZ=0 EndX=9.1 EndY=34.8 EndZ=0
    g12: LineSegment StartX=82.8 StartY=39.2 StartZ=0 EndX=75.01 EndY=39.2 EndZ=0
    g13: LineSegment StartX=82.8 StartY=39.2 StartZ=0 EndX=82.8 EndY=31.3 EndZ=0
    g14: LineSegment StartX=82.8 StartY=31.3 StartZ=0 EndX=78.51 EndY=31.3 EndZ=0
    g15: LineSegment StartX=82.8 StartY=3.2 StartZ=0 EndX=75.01 EndY=3.2 EndZ=0
    g16: LineSegment StartX=75.01 StartY=3.2 StartZ=0 EndX=75.01 EndY=7.6 EndZ=0
    g17: LineSegment StartX=82.8 StartY=3.2 StartZ=0 EndX=82.8 EndY=11.1 EndZ=0
    g18: LineSegment StartX=82.8 StartY=11.1 StartZ=0 EndX=78.51 EndY=11.1 EndZ=0
    g19: LineSegment StartX=75.01 StartY=39.2 StartZ=0 EndX=75.01 EndY=34.8 EndZ=0
  constraints (48):
    c: Radius(g0) = 3.5
    c: Coincident(g0,g-10)
    c: Radius(g1) = 3.5
    c: Coincident(g1,g-9)
    c: Radius(g2) = 3.5
    c: Coincident(g2,g-8)
    c: Radius(g3) = 3.5
    c: Coincident(g3,g-7)
    c: Coincident(g4,g-5)
    c: PointOnObject(g4,g-4)
    c: Coincident(g5,g4)
    c: Horizontal(g5)
    c: Coincident(g6,g4)
    c: PointOnObject(g6,g-5)
    c: Coincident(g7,g6)
    c: Vertical(g7)
    c: Coincident(g8,g-4)
    c: PointOnObject(g8,g-4)
    c: Coincident(g9,g8)
    c: Horizontal(g9)
    c: Coincident(g10,g8)
    c: PointOnObject(g10,g-3)
    c: Coincident(g11,g10)
    c: Vertical(g11)
    c: PointOnObject(g12,g-3)
    c: PointOnObject(g12,g-3)
    c: Coincident(g13,g12)
    c: Vertical(g13)
    c: Coincident(g14,g13)
    c: Horizontal(g14)
    c: Coincident(g15,g-6)
    c: PointOnObject(g15,g-5)
    c: Coincident(g16,g15)
    c: Vertical(g16)
    c: Coincident(g17,g15)
    c: Coincident(g18,g17)
    c: Horizontal(g18)
    c: Tangent(g3,g18) = -1.5708
    c: Tangent(g16,g3) = 1.5708
    c: Coincident(g19,g12)
    c: Vertical(g19)
    c: Tangent(g2,g19) = -1.5708
    c: Tangent(g2,g14) = 1.5708
    c: Tangent(g0,g7) = -1.5708
    c: Tangent(g0,g5) = 1.5708
    c: Tangent(g9,g1) = -1.5708
    c: Tangent(g1,g11) = 1.5708
    c: Tangent(g17,g13)
FEATURE [PartDesign::Pocket] Pocket001
  BaseFeature = -> Pad005
  Direction = (0,-1,2e-16)
  Length = 1.6
  Length2 = 5
  Profile = -> Sketch092
  ReferenceAxis = -> Sketch092 [N_Axis]
  Refine = true
  Suppressed = false
  Type = 0
FEATURE [PartDesign::Pad] Pad006
  BaseFeature = -> Pocket001
  Direction = (0,1,-2e-16)
  Length = 0.8
  Length2 = 10
  Profile = -> Sketch094
  ReferenceAxis = -> Sketch094 [N_Axis]
  Refine = true
  Suppressed = false
  Type = 0
FEATURE [PartDesign::Pad] Pad007
  BaseFeature = -> Pad006
  Direction = (0,1,-2e-16)
  Length = 2
  Length2 = 10
  Profile = -> Sketch095
  ReferenceAxis = -> Sketch095 [N_Axis]
  Refine = true
  Suppressed = false
  Type = 0
FEATURE [PartDesign::Pad] Pad008  label="Pad008 - forma impugnatura"
  BaseFeature = -> Pad007
  Direction = (0,1,-2e-16)
  Length = 1.6
  Length2 = 10
  Profile = -> Sketch096
  ReferenceAxis = -> Sketch096 [N_Axis]
  Refine = true
  Suppressed = false
  Type = 0
FEATURE [PartDesign::Pad] Pad009
  BaseFeature = -> Pad008
  Direction = (0,1,-2e-16)
  Length = 1.6
  Length2 = 10
  Profile = -> Sketch097
  ReferenceAxis = -> Sketch097 [N_Axis]
  Refine = true
  Suppressed = false
  Type = 0
FEATURE [Sketcher::SketchObject] Sketch098
  ArcFitTolerance = 1e-06
  AttachmentSupport = -> [Pad006]
  ExternalGeometry = -> [Binder]
  FullyConstrained = true
  MakeInternals = false
  MapMode = 5
  Placement = pos=(0,2.8,-7e-16) rot=(0,0.707107,0.707107;3.14159rad)
  sketch-geometry (4):
    g0: LineSegment StartX=118 StartY=39.2 StartZ=0 EndX=129 EndY=39.2 EndZ=0
    g1: LineSegment StartX=120.599 StartY=31.2 StartZ=0 EndX=131.599 EndY=31.2 EndZ=0
    g2: LineSegment StartX=129 StartY=39.2 StartZ=0 EndX=131.599 EndY=31.2 EndZ=0
    g3: LineSegment StartX=118 StartY=39.2 StartZ=0 EndX=120.599 EndY=31.2 EndZ=0
  constraints (12):
    c: PointOnObject(g0,g-3)
    c: PointOnObject(g0,g-3)
    c: DistanceX(g0,g0) = 11
    c: Horizontal(g1)
    c: Equal(g1,g0)
    c: Coincident(g2,g0)
    c: Coincident(g3,g0)
    c: Parallel(g-4,g2)
    c: Coincident(g1,g2)
    c: Coincident(g1,g3)
    c: DistanceY(g1,g0) = 8
    c: DistanceX(g-3,g0) = 118
FEATURE [Sketcher::SketchObject] Sketch099
  ArcFitTolerance = 1e-06
  AttachmentSupport = -> [Pad008]
  ExternalGeometry = -> [Binder]
  FullyConstrained = true
  MakeInternals = false
  MapMode = 5
  Placement = pos=(0,3.6,0) rot=(0,0.707107,0.707107;3.14159rad)
  sketch-geometry (13):
    g0: LineSegment StartX=192.176 StartY=-3.18451 StartZ=0 EndX=196.804 EndY=-13.1108 EndZ=0
    g1: LineSegment [constr] StartX=202.765 StartY=20.303 StartZ=0 EndX=181.223 EndY=20.303 EndZ=0
    g2: LineSegment [constr] StartX=181.223 StartY=20.303 StartZ=0 EndX=181.223 EndY=-3.18451 EndZ=0
    g3: ArcOfCircle CenterX=181.223 CenterY=-20.3764 CenterZ=0 NormalX=0 NormalY=0 NormalZ=1 AngleXU=0 Radius=17.1918 StartAngle=0.436332 EndAngle=1.57079
    g4: ArcOfEllipse CenterX=181.223 CenterY=8.55923 CenterZ=0 NormalX=0 NormalY=0 NormalZ=1 MajorRadius=23.4779 MinorRadius=11.7437 AngleXU=0 StartAngle=1.5708 EndAngle=4.71239
    g5: LineSegment [constr] StartX=204.701 StartY=8.55923 StartZ=0 EndX=157.745 EndY=8.55923 EndZ=0
    g6: LineSegment [constr] StartX=181.223 StartY=20.303 StartZ=0 EndX=181.223 EndY=-3.18451 EndZ=0
    g7: GeomPoint [constr] X=201.553 Y=8.55923 Z=0
    g8: GeomPoint [constr] X=160.894 Y=8.55923 Z=0
    g9: GeomPoint [constr] X=181.223 Y=-3.18451 Z=0
    g10: LineSegment StartX=181.223 StartY=20.303 StartZ=0 EndX=202.765 EndY=20.303 EndZ=0
    g11: ArcOfCircle CenterX=207.583 CenterY=4 CenterZ=0 NormalX=0 NormalY=0 NormalZ=1 AngleXU=0 Radius=17 StartAngle=1.85815 EndAngle=3.57792
    g12: LineSegment [constr] StartX=172.411 StartY=39.2 StartZ=0 EndX=192.176 EndY=-3.18451 EndZ=0
  constraints (27):
    c: Coincident(g1,g-7)
    c: Horizontal(g1)
    c: Coincident(g2,g1)
    c: Vertical(g2)
    c: Horizontal(g2,g0)
    c: Coincident(g3,g0)
    c: Coincident(g3,g2)
    c: InternalAlignment(g5-g8 -> g4) x4
    c: Horizontal(g5)
    c: PointOnObject(g4,g2)
    c: Coincident(g4,g1)
    c: DistanceX(g-3,g5) = 10.1
    c: Coincident(g4,g2)
    c: Tangent(g3,g-5)
    c: PointOnObject(g9,g4)
    c: PointOnObject(g9,g3)
    c: Tangent(g4,g3,g9) = 1.5708
    c: Coincident(g10,g1)
    c: Coincident(g10,g1)
    c: Equal(g11,g-4)
    c: Coincident(g11,g1)
    c: Coincident(g11,g0)
    c: PointOnObject(g12,g-6)
    c: PointOnObject(g1,g12)
    c: Tangent(g12,g-5) = -1.5708
    c: Tangent(g0,g-5) = -1.5708
    c: Horizontal(g9,g12)
FEATURE [Sketcher::SketchObject] Sketch106  label="Sketch106 - smusso impuniatura interno"
  ArcFitTolerance = 1e-06
  AttachmentSupport = -> [Pad008]
  ExternalGeometry = -> [Pad008]
  FullyConstrained = true
  MakeInternals = false
  MapMode = 5
  Placement = pos=(0,-1.586e-13,-80.4316) rot=(1,0,0;3.14159rad)
  sketch-geometry (9):
    g0: LineSegment StartX=-176.685 StartY=-3.6 StartZ=0 EndX=-176.685 EndY=-1.43e-13 EndZ=0
    g1: LineSegment [constr] StartX=-176.685 StartY=-1.416e-13 StartZ=0 EndX=-176.685 EndY=-1.429e-13 EndZ=0
    g2: LineSegment [constr] StartX=-186.685 StartY=-3.6 StartZ=0 EndX=-186.685 EndY=-1.43e-13 EndZ=0
    g3: ArcOfEllipse CenterX=-186.685 CenterY=-1.429e-13 CenterZ=0 NormalX=0 NormalY=0 NormalZ=1 MajorRadius=10 MinorRadius=3.6 AngleXU=3.14159 StartAngle=1.5708 EndAngle=3.14159
    g4: LineSegment [constr] StartX=-196.685 StartY=-1.416e-13 StartZ=0 EndX=-176.685 EndY=-1.416e-13 EndZ=0
    g5: LineSegment [constr] StartX=-186.685 StartY=-3.6 StartZ=0 EndX=-186.685 EndY=3.6 EndZ=0
    g6: GeomPoint [constr] X=-196.015 Y=-1.416e-13 Z=0
    g7: GeomPoint [constr] X=-177.356 Y=-1.416e-13 Z=0
    g8: LineSegment StartX=-176.685 StartY=-3.6 StartZ=0 EndX=-186.685 EndY=-3.6 EndZ=0
  constraints (15):
    c: PointOnObject(g2,g-3)
    c: Coincident(g1,g-5)
    c: DistanceY(g1,g1) = 0
    c: Coincident(g0,g1)
    c: DistanceX(g2,g-5) = 10
    c: Vertical(g2)
    c: Horizontal(g2,g0)
    c: InternalAlignment(g4-g7 -> g3) x4
    c: Coincident(g3,g2)
    c: Horizontal(g4)
    c: Coincident(g3,g0)
    c: Tangent(g0,g-5) = 1.5708
    c: Coincident(g3,g2)
    c: Coincident(g8,g0)
    c: Coincident(g8,g2)
FEATURE [Sketcher::SketchObject] Sketch107  label="Sketch107 - smusso impugnatura esterno"
  ArcFitTolerance = 1e-06
  AttachmentSupport = -> [Pad008]
  ExternalGeometry = -> [Pad008]
  FullyConstrained = true
  MakeInternals = false
  MapMode = 5
  Placement = pos=(0,-1.586e-13,-80.4316) rot=(1,0,0;3.14159rad)
  sketch-geometry (9):
    g0: LineSegment [constr] StartX=-215.932 StartY=1.79e-14 StartZ=0 EndX=-215.932 EndY=2.57e-14 EndZ=0
    g1: LineSegment StartX=-215.932 StartY=-3.6 StartZ=0 EndX=-215.932 EndY=2.58e-14 EndZ=0
    g2: LineSegment StartX=-215.932 StartY=-3.6 StartZ=0 EndX=-205.932 EndY=-3.6 EndZ=0
    g3: LineSegment [constr] StartX=-205.932 StartY=-3.6 StartZ=0 EndX=-205.932 EndY=2.58e-14 EndZ=0
    g4: ArcOfEllipse CenterX=-205.932 CenterY=2.57e-14 CenterZ=0 NormalX=0 NormalY=0 NormalZ=1 MajorRadius=10 MinorRadius=3.6 AngleXU=3.14159 StartAngle=1e-16 EndAngle=1.5708
    g5: LineSegment [constr] StartX=-215.932 StartY=1.79e-14 StartZ=0 EndX=-195.932 EndY=1.79e-14 EndZ=0
    g6: LineSegment [constr] StartX=-205.932 StartY=-3.6 StartZ=0 EndX=-205.932 EndY=3.6 EndZ=0
    g7: GeomPoint [constr] X=-215.262 Y=2.6e-14 Z=0
    g8: GeomPoint [constr] X=-196.602 Y=1.78e-14 Z=0
  constraints (16):
    c: Coincident(g0,g-6)
    c: PointOnObject(g0,g-6)
    c: DistanceY(g0,g0) = 0
    c: Coincident(g1,g-6)
    c: Coincident(g1,g0)
    c: Tangent(g2,g-3)
    c: DistanceX(g2,g2) = 10
    c: Coincident(g3,g2)
    c: Vertical(g3)
    c: Horizontal(g3,g0)
    c: InternalAlignment(g5-g8 -> g4) x4
    c: Coincident(g4,g3)
    c: Horizontal(g5)
    c: Coincident(g4,g0)
    c: Coincident(g4,g2)
    c: PointOnObject(g2,g1)
FEATURE [Sketcher::SketchObject] Sketch108
  ArcFitTolerance = 1e-06
  AttachmentOffset = pos=(0,0,-1.6) rot=(0,0,1;0rad)
  AttachmentSupport = -> [Pad008]
  ExternalGeometry = -> [Binder]
  FullyConstrained = true
  MakeInternals = false
  MapMode = 5
  Placement = pos=(0,2,4e-16) rot=(0,0.707107,0.707107;3.14159rad)
  sketch-geometry (14):
    g0: LineSegment StartX=192.176 StartY=-3.18451 StartZ=0 EndX=193.827 EndY=-6.72678 EndZ=0
    g1: LineSegment [constr] StartX=202.765 StartY=20.303 StartZ=0 EndX=181.223 EndY=20.303 EndZ=0
    g2: LineSegment [constr] StartX=181.223 StartY=20.303 StartZ=0 EndX=181.223 EndY=1.30297 EndZ=0
    g3: ArcOfCircle CenterX=181.223 CenterY=-12.6042 CenterZ=0 NormalX=0 NormalY=0 NormalZ=1 AngleXU=0 Radius=13.9072 StartAngle=0.436332 EndAngle=1.5708
    g4: ArcOfEllipse CenterX=181.223 CenterY=10.803 CenterZ=0 NormalX=0 NormalY=0 NormalZ=1 MajorRadius=14.4779 MinorRadius=9.5 AngleXU=0 StartAngle=1.5708 EndAngle=4.71239
    g5: LineSegment [constr] StartX=195.701 StartY=10.803 StartZ=0 EndX=166.745 EndY=10.803 EndZ=0
    g6: LineSegment [constr] StartX=181.223 StartY=20.303 StartZ=0 EndX=181.223 EndY=1.30297 EndZ=0
    g7: GeomPoint [constr] X=192.148 Y=10.803 Z=0
    g8: GeomPoint [constr] X=170.298 Y=10.803 Z=0
    g9: LineSegment StartX=181.223 StartY=20.303 StartZ=0 EndX=202.765 EndY=20.303 EndZ=0
    g10: ArcOfCircle CenterX=207.583 CenterY=4 CenterZ=0 NormalX=0 NormalY=0 NormalZ=1 AngleXU=0 Radius=17 StartAngle=1.85815 EndAngle=3.57792
    g11: LineSegment [constr] StartX=172.411 StartY=39.2 StartZ=0 EndX=192.176 EndY=-3.18451 EndZ=0
    g12: GeomPoint [constr] X=181.223 Y=1.30297 Z=0
    g13: GeomPoint [constr] X=181.223 Y=1.30297 Z=0
  constraints (28):
    c: Coincident(g1,g-7)
    c: Horizontal(g1)
    c: Coincident(g2,g1)
    c: Vertical(g2)
    c: Coincident(g3,g2)
    c: InternalAlignment(g5-g8 -> g4) x4
    c: Horizontal(g5)
    c: PointOnObject(g4,g2)
    c: Coincident(g4,g1)
    c: DistanceX(g-3,g5) = 19.1
    c: Coincident(g4,g2)
    c: Coincident(g9,g1)
    c: Coincident(g9,g1)
    c: Coincident(g10,g1)
    c: Coincident(g10,g0)
    c: PointOnObject(g11,g-6)
    c: PointOnObject(g1,g11)
    c: DistanceY(g2,g1) = 19
    c: Coincident(g10,g-4)
    c: PointOnObject(g12,g4)
    c: PointOnObject(g12,g3)
    c: Tangent(g11,g-5) = -1.5708
    c: Tangent(g0,g-5) = -1.5708
    c: Tangent(g3,g0) = 1.5708
    c: PointOnObject(g13,g4)
    c: PointOnObject(g13,g3)
    c: Tangent(g4,g3,g13) = 1.5708
    c: Horizontal(g11,g0)
FEATURE [Part::Part2DObjectPython] Clone2D  label="Sketch108 (2D)"  # Draft 2D object (typed FeaturePython)
  Fuse = false
  Objects = -> [Sketch108]
  Placement = pos=(0,2,4e-16) rot=(0,0.707107,0.707107;3.14159rad)
  Scale = (1,1,1)
FEATURE [Sketcher::SketchObject] Sketch109
  ArcFitTolerance = 1e-06
  AttachmentOffset = pos=(0,0,-3.5) rot=(0,0,1;0rad)
  AttachmentSupport = -> [Pad008]
  ExternalGeometry = -> [Binder]
  FullyConstrained = true
  MakeInternals = false
  MapMode = 5
  Placement = pos=(0,0.1,8e-16) rot=(0,0.707107,0.707107;3.14159rad)
  sketch-geometry (1):
    g0: GeomPoint X=197.47 Y=8.55923 Z=0
  constraints (1):
    c: Symmetric(g-7,g-5,g0)
FEATURE [PartDesign::Chamfer] Chamfer005
  Angle = 45
  Base = -> Pad009 [Edge215,Edge212]
  BaseFeature = -> Pad009
  ChamferType = 1
  FlipDirection = false
  Refine = true
  Size = 1.5
  Size2 = 2.8
  SupportTransform = false
  Suppressed = false
  UseAllEdges = false
FEATURE [Sketcher::SketchObject] Sketch111
  ArcFitTolerance = 1e-06
  AttachmentSupport = -> [Pad009]
  ExternalGeometry = -> [Pad009]
  FullyConstrained = true
  MakeInternals = false
  MapMode = 5
  Placement = pos=(0,3.6,-8e-16) rot=(0,0.707107,0.707107;3.14159rad)
  sketch-geometry (21):
    g0: LineSegment [constr] StartX=97 StartY=36.8 StartZ=0 EndX=97 EndY=26.8 EndZ=0
    g1: LineSegment StartX=97 StartY=28.6 StartZ=0 EndX=97 EndY=27.8 EndZ=0
    g2: LineSegment StartX=97 StartY=27.8 StartZ=0 EndX=108 EndY=27.8 EndZ=0
    g3: LineSegment StartX=108 StartY=27.8 StartZ=0 EndX=108 EndY=28.6 EndZ=0
    g4: LineSegment StartX=108 StartY=28.6 StartZ=0 EndX=97 EndY=28.6 EndZ=0
    g5: LineSegment StartX=97 StartY=35.8 StartZ=0 EndX=97 EndY=35 EndZ=0
    g6: LineSegment StartX=97 StartY=35 StartZ=0 EndX=108 EndY=35 EndZ=0
    g7: LineSegment StartX=108 StartY=35 StartZ=0 EndX=108 EndY=35.8 EndZ=0
    g8: LineSegment StartX=108 StartY=35.8 StartZ=0 EndX=97 EndY=35.8 EndZ=0
    g9: LineSegment StartX=97 StartY=30.4 StartZ=0 EndX=97 EndY=29.6 EndZ=0
    g10: LineSegment StartX=97 StartY=29.6 StartZ=0 EndX=108 EndY=29.6 EndZ=0
    g11: LineSegment StartX=108 StartY=29.6 StartZ=0 EndX=108 EndY=30.4 EndZ=0
    g12: LineSegment StartX=108 StartY=30.4 StartZ=0 EndX=97 EndY=30.4 EndZ=0
    g13: LineSegment StartX=97 StartY=34 StartZ=0 EndX=97 EndY=33.2 EndZ=0
    g14: LineSegment StartX=97 StartY=33.2 StartZ=0 EndX=108 EndY=33.2 EndZ=0
    g15: LineSegment StartX=108 StartY=33.2 StartZ=0 EndX=108 EndY=34 EndZ=0
    g16: LineSegment StartX=108 StartY=34 StartZ=0 EndX=97 EndY=34 EndZ=0
    g17: LineSegment StartX=97 StartY=32.2 StartZ=0 EndX=97 EndY=31.4 EndZ=0
    g18: LineSegment StartX=97 StartY=31.4 StartZ=0 EndX=108 EndY=31.4 EndZ=0
    g19: LineSegment StartX=108 StartY=31.4 StartZ=0 EndX=108 EndY=32.2 EndZ=0
    g20: LineSegment StartX=108 StartY=32.2 StartZ=0 EndX=97 EndY=32.2 EndZ=0
  constraints (54):
    c: Vertical(g0)
    c: PointOnObject(g0,g-3)
    c: PointOnObject(g0,g-4)
    c: DistanceX(g0,g-5) = 11
    c: Coincident(g1,g2)
    c: Coincident(g2,g3)
    c: Coincident(g3,g4)
    c: Coincident(g4,g1)
    c: Horizontal(g2)
    c: Horizontal(g4)
    c: Tangent(g1,g0)
    c: Tangent(g3,g-5)
    c: DistanceY(g2,g3) = 0.8
    c: Coincident(g5,g6)
    c: Coincident(g6,g7)
    c: Coincident(g7,g8)
    c: Coincident(g8,g5)
    c: Horizontal(g6)
    c: Horizontal(g8)
    c: DistanceY(g6,g7) = 0.8
    c: Coincident(g9,g10)
    c: Coincident(g10,g11)
    c: Coincident(g11,g12)
    c: Coincident(g12,g9)
    c: Horizontal(g10)
    c: Horizontal(g12)
    c: DistanceY(g10,g11) = 0.8
    c: Tangent(g5,g0)
    c: Tangent(g7,g-5)
    c: Tangent(g9,g0)
    c: Tangent(g11,g-5)
    c: Coincident(g13,g14)
    c: Coincident(g14,g15)
    c: Coincident(g15,g16)
    c: Coincident(g16,g13)
    c: Horizontal(g14)
    c: Horizontal(g16)
    c: DistanceY(g14,g15) = 0.8
    c: Tangent(g13,g0)
    c: Tangent(g15,g-5)
    c: Coincident(g17,g18)
    c: Coincident(g18,g19)
    c: Coincident(g19,g20)
    c: Coincident(g20,g17)
    c: Horizontal(g18)
    c: Horizontal(g20)
    c: DistanceY(g18,g19) = 0.8
    c: Tangent(g17,g0)
    c: Tangent(g19,g-5)
    c: DistanceY(g1,g9) = 1
    c: DistanceY(g9,g17) = 1
    c: DistanceY(g17,g13) = 1
    c: DistanceY(g13,g5) = 1
    c: DistanceY(g0,g1) = 1
FEATURE [PartDesign::Pocket] Pocket004
  BaseFeature = -> Chamfer005
  Direction = (0,-1,2e-16)
  Length = 1
  Length2 = 5
  Profile = -> Sketch111
  ReferenceAxis = -> Sketch111 [N_Axis]
  Refine = true
  Suppressed = false
  Type = 0
FEATURE [PartDesign::Pad] Pad010
  BaseFeature = -> Pocket004
  Direction = (0,1,-2e-16)
  Length = 1.2
  Length2 = 10
  Profile = -> Sketch098
  ReferenceAxis = -> Sketch098 [N_Axis]
  Refine = true
  Suppressed = false
  Type = 0
FEATURE [PartDesign::Chamfer] Chamfer006
  Angle = 45
  Base = -> Pad010 [Edge291]
  BaseFeature = -> Pad010
  ChamferType = 1
  FlipDirection = false
  Refine = true
  Size = 1
  Size2 = 6
  SupportTransform = false
  Suppressed = false
  UseAllEdges = false
FEATURE [Sketcher::SketchObject] Sketch110
  ArcFitTolerance = 1e-06
  AttachmentSupport = -> [Pad010]
  ExternalGeometry = -> [Sketch098]
  FullyConstrained = true
  MakeInternals = false
  MapMode = 5
  Placement = pos=(0,4,-9e-16) rot=(0,0.707107,0.707107;3.14159rad)
  sketch-geometry (8):
    g0: LineSegment StartX=119.69 StartY=34 StartZ=0 EndX=130.69 EndY=34 EndZ=0
    g1: LineSegment StartX=119.95 StartY=33.2 StartZ=0 EndX=130.95 EndY=33.2 EndZ=0
    g2: LineSegment StartX=119.137 StartY=35.7 StartZ=0 EndX=130.137 EndY=35.7 EndZ=0
    g3: LineSegment StartX=118.877 StartY=36.5 StartZ=0 EndX=129.877 EndY=36.5 EndZ=0
    g4: LineSegment StartX=118.877 StartY=36.5 StartZ=0 EndX=119.137 EndY=35.7 EndZ=0
    g5: LineSegment StartX=129.877 StartY=36.5 StartZ=0 EndX=130.137 EndY=35.7 EndZ=0
    g6: LineSegment StartX=119.69 StartY=34 StartZ=0 EndX=119.95 EndY=33.2 EndZ=0
    g7: LineSegment StartX=130.69 StartY=34 StartZ=0 EndX=130.95 EndY=33.2 EndZ=0
  constraints (24):
    c: Horizontal(g0)
    c: Horizontal(g1)
    c: Horizontal(g2)
    c: Horizontal(g3)
    c: Equal(g1,g-5)
    c: Equal(g0,g-5)
    c: Equal(g2,g-5)
    c: Equal(g3,g-5)
    c: PointOnObject(g0,g-3)
    c: PointOnObject(g1,g-3)
    c: PointOnObject(g2,g-3)
    c: PointOnObject(g3,g-3)
    c: Coincident(g4,g3)
    c: Coincident(g4,g2)
    c: Coincident(g5,g3)
    c: Coincident(g5,g2)
    c: Coincident(g6,g0)
    c: Coincident(g6,g1)
    c: Coincident(g7,g0)
    c: Coincident(g7,g1)
    c: DistanceY(g1,g0) = 0.8
    c: DistanceY(g2,g3) = 0.8
    c: DistanceY(g-5,g1) = 2
    c: DistanceY(g-5,g2) = 4.5
FEATURE [PartDesign::Pocket] Pocket003
  BaseFeature = -> Chamfer006
  Direction = (0,-1,2e-16)
  Length = 1
  Length2 = 5
  Profile = -> Sketch110
  ReferenceAxis = -> Sketch110 [N_Axis]
  Refine = true
  Suppressed = false
  Type = 0
FEATURE [PartDesign::SubtractivePipe] SubtractivePipe
  AuxilleryCurvelinear = true
  AuxillerySpineTangent = false
  BaseFeature = -> Pocket003
  Binormal = (0,0,0)
  Mode = 0
  Profile = -> Sketch106
  Refine = true
  Spine = -> Pad008 [Edge215]
  SpineTangent = false
  Suppressed = false
  Transformation = 0
  Transition = 0
FEATURE [PartDesign::SubtractivePipe] SubtractivePipe001
  AuxilleryCurvelinear = true
  AuxillerySpineTangent = false
  BaseFeature = -> SubtractivePipe
  Binormal = (0,0,0)
  Mode = 0
  Profile = -> Sketch107
  Refine = true
  Spine = -> Pad008 [Edge213,Edge216,Edge210]
  SpineTangent = false
  Suppressed = false
  Transformation = 0
  Transition = 0
FEATURE [PartDesign::SubtractiveLoft] SubtractiveLoft
  BaseFeature = -> SubtractivePipe001
  Closed = false
  Profile = -> Sketch099
  Refine = true
  Ruled = false
  Sections = -> [Sketch108]
  Suppressed = false
FEATURE [PartDesign::SubtractiveLoft] SubtractiveLoft001
  BaseFeature = -> SubtractiveLoft
  Closed = false
  Profile = -> Clone2D
  Refine = true
  Ruled = false
  Sections = -> [Sketch109]
  Suppressed = false
FEATURE [Sketcher::SketchObject] Sketch112
  ArcFitTolerance = 1e-06
  AttachmentSupport = -> [Pad008]
  ExternalGeometry = -> [Binder]
  FullyConstrained = true
  MakeInternals = false
  MapMode = 5
  Placement = pos=(0,3.6,0) rot=(0,0.707107,0.707107;3.14159rad)
  sketch-geometry (4):
    g0: LineSegment [constr] StartX=167.782 StartY=-53.0314 StartZ=0 EndX=215.42 EndY=-53.0314 EndZ=0
    g1: GeomPoint [constr] X=191.282 Y=-53.0314 Z=0
    g2: Circle CenterX=191.282 CenterY=-53.0314 CenterZ=0 NormalX=0 NormalY=0 NormalZ=1 AngleXU=0 Radius=11.5
    g3: Circle CenterX=191.282 CenterY=-53.0314 CenterZ=0 NormalX=0 NormalY=0 NormalZ=1 AngleXU=0 Radius=10.7
  constraints (9):
    c: Horizontal(g0)
    c: PointOnObject(g0,g-3)
    c: Diameter(g2) = 23
    c: Coincident(g2,g1)
    c: Diameter(g3) = 21.4
    c: Coincident(g3,g1)
    c: DistanceX(g0,g1) = 23.5
    c: PointOnObject(g1,g0)
    c: Coincident(g0,g-4)
FEATURE [PartDesign::Chamfer] Chamfer016
  Angle = 45
  Base = -> SubtractiveLoft001 [Edge118,Edge117,Edge119,Edge120,Edge109]
  BaseFeature = -> SubtractiveLoft001
  ChamferType = 0
  FlipDirection = false
  Refine = true
  Size = 1.5
  Size2 = 1
  SupportTransform = false
  Suppressed = false
  UseAllEdges = false
FEATURE [PartDesign::Chamfer] Chamfer017
  Angle = 45
  Base = -> Chamfer016 [Edge15]
  BaseFeature = -> Chamfer016
  ChamferType = 0
  FlipDirection = false
  Refine = true
  Size = 1.6
  Size2 = 1
  SupportTransform = false
  Suppressed = false
  UseAllEdges = false
FEATURE [PartDesign::Chamfer] Chamfer018
  Angle = 45
  Base = -> Chamfer017 [Edge10]
  BaseFeature = -> Chamfer017
  ChamferType = 0
  FlipDirection = false
  Refine = true
  Size = 3.5
  Size2 = 1
  SupportTransform = false
  Suppressed = false
  UseAllEdges = false
FEATURE [PartDesign::Chamfer] Chamfer019
  Angle = 45
  Base = -> Chamfer018 [Edge94,Edge199]
  BaseFeature = -> Chamfer018
  ChamferType = 0
  FlipDirection = false
  Refine = true
  Size = 1.9
  Size2 = 1
  SupportTransform = false
  Suppressed = false
  UseAllEdges = false
FEATURE [PartDesign::Fillet] Fillet009
  Base = -> Chamfer019 [Edge83]
  BaseFeature = -> Chamfer019
  Radius = 1.1
  Refine = true
  SupportTransform = false
  Suppressed = false
  UseAllEdges = false
FEATURE [PartDesign::Fillet] Fillet010
  Base = -> Fillet009 [Edge77]
  BaseFeature = -> Fillet009
  Radius = 1.9
  Refine = true
  SupportTransform = false
  Suppressed = false
  UseAllEdges = false
FEATURE [PartDesign::Pocket] Pocket005
  BaseFeature = -> Fillet010
  Direction = (0,-1,2e-16)
  Length = 0.8
  Length2 = 5
  Profile = -> Sketch112
  ReferenceAxis = -> Sketch112 [N_Axis]
  Refine = true
  Suppressed = false
  Type = 0
FEATURE [Part::Part2DObjectPython] ShapeString001  # Draft 2D object (typed FeaturePython)
  FontFile = <path>
  Fuse = false
  Justification = 6
  JustificationReference = 0
  KeepLeftMargin = false
  MakeFace = true
  ObliqueAngle = 0
  Placement = pos=(-183.5,3.6,-57.5) rot=(0,0.707107,0.707107;3.14159rad)
  ScaleToSize = true
  Size = 10
  String = AS
  Tracking = 0
FEATURE [PartDesign::Pocket] Pocket013
  BaseFeature = -> Pocket005
  Direction = (-1e-16,-1,2e-16)
  Length = 1
  Length2 = 5
  Profile = -> ShapeString001
  ReferenceAxis = -> ShapeString001 [N_Axis]
  Refine = true
  Suppressed = false
  Type = 0
FEATURE [PartDesign::Body] Body006  label="lato SX"
  AllowCompound = false
  Group = -> [Binder,Pad019,Chamfer015,Pocket002,Sketch133,Sketch091,Pad005,Sketch092,Pocket001,Sketch093,Sketch094,Pad006,Sketch095,Pad007,Sketch096,Pad008,Sketch097,Pad009,Chamfer005,Pocket004,Sketch098,Pad010,Chamfer006,Pocket003,SubtractivePipe,SubtractivePipe001,Sketch099,Sketch106,Sketch107,Sketch108,Clone2D,Sketch109,SubtractiveLoft,SubtractiveLoft001,Sketch110,Sketch111,Sketch112,Chamfer016,Chamfer017,+7 more]
  Origin = -> Origin006
  Tip = -> Pocket013
FEATURE [PartDesign::Pad] Pad020
  Direction = (0,-1,2e-16)
  Length = 25.2
  Length2 = 10
  Midplane = true
  Placement = pos=(0,0,0) rot=(1,0,0;1.5708rad)
  Profile = -> Sketch021
  ReferenceAxis = -> Sketch021 [N_Axis]
  Refine = true
  Suppressed = false
  Type = 0
FEATURE [PartDesign::Body] Body001  label="perno fermo rumble e driver solenoide"
  AllowCompound = false
  Group = -> [Sketch021,Pad020]
  Origin = -> Origin001
  Tip = -> Pad020
FEATURE [PartDesign::Pad] Pad021
  Direction = (0,-1,2e-16)
  Length = 16.8
  Length2 = 10
  Midplane = true
  Placement = pos=(0,0,0) rot=(1,0,0;1.5708rad)
  Profile = -> Sketch061
  ReferenceAxis = -> Sketch061 [N_Axis]
  Refine = true
  Suppressed = false
  Type = 0
FEATURE [PartDesign::Pocket] Pocket014
  BaseFeature = -> Pad021
  Direction = (0,1,-2e-16)
  Length = 12.8
  Length2 = 5
  Midplane = true
  Placement = pos=(0,0,0) rot=(1,0,0;1.5708rad)
  Profile = -> Sketch062
  ReferenceAxis = -> Sketch062 [N_Axis]
  Refine = true
  Suppressed = false
  Type = 0
FEATURE [PartDesign::Pad] Pad022
  BaseFeature = -> Pocket014
  Direction = (0,-1,2e-16)
  Length = 7.6
  Length2 = 10
  Midplane = true
  Placement = pos=(0,0,0) rot=(1,0,0;1.5708rad)
  Profile = -> Sketch063
  ReferenceAxis = -> Sketch063 [N_Axis]
  Refine = true
  Suppressed = false
  Type = 0
FEATURE [PartDesign::Body] Body003  label="blocco switch"
  AllowCompound = false
  Group = -> [Sketch061,Sketch062,Sketch063,Pad021,Pocket014,Pad022]
  Origin = -> Origin003
  Tip = -> Pad022
FEATURE [PartDesign::Pad] Pad024
  Direction = (0,-1,2e-16)
  Length = 17
  Length2 = 10
  Midplane = true
  Placement = pos=(0,0,0) rot=(1,0,0;1.5708rad)
  Profile = -> Sketch045
  ReferenceAxis = -> Sketch045 [N_Axis]
  Refine = true
  Suppressed = false
  Type = 0
FEATURE [PartDesign::Pocket] Pocket015
  BaseFeature = -> Pad024
  Direction = (-1,0,0)
  Length = 8
  Length2 = 5
  Placement = pos=(0,0,0) rot=(1,0,0;1.5708rad)
  Profile = -> Sketch047
  ReferenceAxis = -> Sketch047 [N_Axis]
  Refine = true
  Reversed = true
  Suppressed = false
  Type = 0
FEATURE [PartDesign::Pocket] Pocket016
  BaseFeature = -> Pocket015
  Direction = (-1,0,0)
  Length = 1
  Length2 = 5
  Placement = pos=(0,0,0) rot=(1,0,0;1.5708rad)
  Profile = -> Sketch046
  ReferenceAxis = -> Sketch046 [N_Axis]
  Refine = true
  Reversed = true
  Suppressed = false
  Type = 0
FEATURE [PartDesign::Pocket] Pocket017
  BaseFeature = -> Pocket016
  Direction = (0,1,-2e-16)
  Length = 17
  Length2 = 5
  Midplane = true
  Placement = pos=(0,0,0) rot=(1,0,0;1.5708rad)
  Profile = -> Sketch048
  ReferenceAxis = -> Sketch048 [N_Axis]
  Refine = true
  Suppressed = false
  Type = 0
FEATURE [PartDesign::Pad] Pad025
  BaseFeature = -> Pocket017
  Direction = (0,-1,2e-16)
  Length = 17
  Length2 = 10
  Midplane = true
  Placement = pos=(0,0,0) rot=(1,0,0;1.5708rad)
  Profile = -> Sketch049
  ReferenceAxis = -> Sketch049 [N_Axis]
  Refine = true
  Suppressed = false
  Type = 0
FEATURE [PartDesign::Pad] Pad026
  BaseFeature = -> Pad025
  Direction = (0,-1,2e-16)
  Length = 17
  Length2 = 10
  Midplane = true
  Placement = pos=(0,0,0) rot=(1,0,0;1.5708rad)
  Profile = -> Sketch066
  ReferenceAxis = -> Sketch066 [N_Axis]
  Refine = true
  Suppressed = false
  Type = 0
FEATURE [PartDesign::Pad] Pad027
  BaseFeature = -> Pad026
  Direction = (0,-1,2e-16)
  Length = 5
  Length2 = 10
  Midplane = true
  Placement = pos=(0,0,0) rot=(1,0,0;1.5708rad)
  Profile = -> Sketch064
  ReferenceAxis = -> Sketch064 [N_Axis]
  Refine = true
  Suppressed = false
  Type = 0
FEATURE [PartDesign::Pad] Pad028
  BaseFeature = -> Pad027
  Direction = (1,0,0)
  Length = 1
  Length2 = 10
  Placement = pos=(0,0,0) rot=(1,0,0;1.5708rad)
  Profile = -> Sketch068
  ReferenceAxis = -> Sketch068 [N_Axis]
  Refine = true
  Reversed = true
  Suppressed = false
  Type = 0
FEATURE [PartDesign::Chamfer] Chamfer020
  Angle = 45
  Base = -> Pad028 [Edge73,Edge75,Edge78,Edge77]
  BaseFeature = -> Pad028
  ChamferType = 0
  FlipDirection = false
  Placement = pos=(0,0,0) rot=(1,0,0;1.5708rad)
  Refine = true
  Size = 0.5
  Size2 = 1
  SupportTransform = false
  Suppressed = false
  UseAllEdges = false
FEATURE [PartDesign::Body] Body002  label="supporto per neopixel"
  AllowCompound = false
  Group = -> [Sketch045,Sketch047,Sketch046,Sketch048,Sketch049,Sketch066,Sketch064,Sketch068,Pad024,Pocket015,Pocket016,Pocket017,Pad025,Pad026,Pad027,Pad028,Chamfer020]
  Origin = -> Origin002
  Tip = -> Chamfer020
FEATURE [Sketcher::SketchObject] Sketch134  label="perno fermo rumble002"
  ArcFitTolerance = 1e-06
  AttachmentSupport = -> [XZ_Plane008]
  FullyConstrained = true
  MakeInternals = false
  MapMode = 5
  Placement = pos=(0,0,0) rot=(1,0,0;1.5708rad)
  sketch-geometry (16):
    g0: LineSegment StartX=0 StartY=0.45 StartZ=0 EndX=0 EndY=1.55 EndZ=0
    g1: LineSegment StartX=0.45 StartY=2 StartZ=0 EndX=1.55 EndY=2 EndZ=0
    g2: LineSegment StartX=2 StartY=1.55 StartZ=0 EndX=2 EndY=0.45 EndZ=0
    g3: LineSegment StartX=1.55 StartY=0 StartZ=0 EndX=0.45 EndY=0 EndZ=0
    g4: ArcOfCircle [constr] CenterX=0.45 CenterY=1.55 CenterZ=0 NormalX=0 NormalY=0 NormalZ=1 AngleXU=0 Radius=0.45 StartAngle=1.5708 EndAngle=3.14159
    g5: GeomPoint [constr] X=0 Y=2 Z=0
    g6: LineSegment StartX=0.45 StartY=2 StartZ=0 EndX=0 EndY=1.55 EndZ=0
    g7: ArcOfCircle [constr] CenterX=1.55 CenterY=1.55 CenterZ=0 NormalX=0 NormalY=0 NormalZ=1 AngleXU=0 Radius=0.45 StartAngle=0 EndAngle=1.5708
    g8: GeomPoint [constr] X=2 Y=2 Z=0
    g9: LineSegment StartX=2 StartY=1.55 StartZ=0 EndX=1.55 EndY=2 EndZ=0
    g10: ArcOfCircle [constr] CenterX=1.55 CenterY=0.45 CenterZ=0 NormalX=0 NormalY=0 NormalZ=1 AngleXU=0 Radius=0.45 StartAngle=4.71239 EndAngle=6.28319
    g11: GeomPoint [constr] X=2 Y=0 Z=0
    g12: LineSegment StartX=1.55 StartY=0 StartZ=0 EndX=2 EndY=0.45 EndZ=0
    g13: ArcOfCircle [constr] CenterX=0.45 CenterY=0.45 CenterZ=0 NormalX=0 NormalY=0 NormalZ=1 AngleXU=0 Radius=0.45 StartAngle=3.14159 EndAngle=4.71239
    g14: GeomPoint [constr] X=0 Y=0 Z=0
    g15: LineSegment StartX=0 StartY=0.45 StartZ=0 EndX=0.45 EndY=0 EndZ=0
  constraints (35):
    c: Coincident(g14,g-1)
    c: PointOnObject(g5,g-2)
    c: Horizontal(g1)
    c: Vertical(g2)
    c: Horizontal(g3)
    c: DistanceX(g5,g8) = 2
    c: DistanceY(g11,g8) = 2
    c: PointOnObject(g5,g0)
    c: PointOnObject(g5,g1)
    c: Tangent(g0,g4) = 1.5708
    c: Tangent(g1,g4) = 1.5708
    c: Coincident(g6,g0)
    c: Coincident(g6,g1)
    c: PointOnObject(g8,g2)
    c: PointOnObject(g8,g1)
    c: Tangent(g2,g7) = 1.5708
    c: Tangent(g1,g7) = 1.5708
    c: Coincident(g9,g2)
    c: Coincident(g9,g1)
    c: PointOnObject(g11,g2)
    c: PointOnObject(g11,g3)
    c: Tangent(g2,g10) = 1.5708
    c: Tangent(g3,g10) = 1.5708
    c: Coincident(g12,g2)
    c: Coincident(g12,g3)
    c: PointOnObject(g14,g0)
    c: PointOnObject(g14,g3)
    c: Tangent(g0,g13) = 1.5708
    c: Tangent(g3,g13) = 1.5708
    c: Coincident(g15,g0)
    c: Coincident(g15,g3)
    c: Equal(g6,g9)
    c: Equal(g9,g12)
    c: Equal(g12,g15)
    c: DistanceX(g14,g3) = 0.45
FEATURE [PartDesign::Pad] Pad029
  Direction = (0,-1,2e-16)
  Length = 17
  Length2 = 10
  Midplane = true
  Placement = pos=(0,0,0) rot=(1,0,0;1.5708rad)
  Profile = -> Sketch134
  ReferenceAxis = -> Sketch134 [N_Axis]
  Refine = true
  Suppressed = false
  Type = 0
FEATURE [PartDesign::Body] Body008  label="perno fermo neopixel"
  AllowCompound = false
  Group = -> [Sketch134,Pad029]
  Origin = -> Origin008
  Tip = -> Pad029
FEATURE [Sketcher::SketchObject] Sketch135  label="perno fermo rumble003"
  ArcFitTolerance = 1e-06
  AttachmentSupport = -> [XZ_Plane009]
  FullyConstrained = true
  MakeInternals = false
  MapMode = 5
  Placement = pos=(0,0,0) rot=(1,0,0;1.5708rad)
  sketch-geometry (16):
    g0: LineSegment StartX=4.69e-14 StartY=0.8 StartZ=0 EndX=-3.04e-14 EndY=3.1 EndZ=0
    g1: LineSegment StartX=0.8 StartY=3.9 StartZ=0 EndX=3.1 EndY=3.9 EndZ=0
    g2: LineSegment StartX=3.9 StartY=3.1 StartZ=0 EndX=3.9 EndY=0.8 EndZ=0
    g3: LineSegment StartX=3.1 StartY=0 StartZ=0 EndX=0.8 EndY=0 EndZ=0
    g4: ArcOfCircle [constr] CenterX=0.8 CenterY=3.1 CenterZ=0 NormalX=0 NormalY=0 NormalZ=1 AngleXU=0 Radius=0.8 StartAngle=1.5708 EndAngle=3.14159
    g5: GeomPoint [constr] X=0 Y=3.9 Z=0
    g6: LineSegment StartX=0.8 StartY=3.9 StartZ=0 EndX=-3.04e-14 EndY=3.1 EndZ=0
    g7: ArcOfCircle [constr] CenterX=3.1 CenterY=3.1 CenterZ=0 NormalX=0 NormalY=0 NormalZ=1 AngleXU=0 Radius=0.8 StartAngle=-2.4e-14 EndAngle=1.5708
    g8: GeomPoint [constr] X=3.9 Y=3.9 Z=0
    g9: LineSegment StartX=3.9 StartY=3.1 StartZ=0 EndX=3.1 EndY=3.9 EndZ=0
    g10: ArcOfCircle [constr] CenterX=3.1 CenterY=0.8 CenterZ=0 NormalX=0 NormalY=0 NormalZ=1 AngleXU=0 Radius=0.8 StartAngle=4.71239 EndAngle=6.28319
    g11: GeomPoint [constr] X=3.9 Y=0 Z=0
    g12: LineSegment StartX=3.1 StartY=0 StartZ=0 EndX=3.9 EndY=0.8 EndZ=0
    g13: ArcOfCircle [constr] CenterX=0.8 CenterY=0.8 CenterZ=0 NormalX=0 NormalY=0 NormalZ=1 AngleXU=0 Radius=0.8 StartAngle=3.14159 EndAngle=4.71239
    g14: GeomPoint [constr] X=0 Y=0 Z=0
    g15: LineSegment StartX=4.69e-14 StartY=0.8 StartZ=0 EndX=0.8 EndY=0 EndZ=0
  constraints (35):
    c: Coincident(g14,g-1)
    c: PointOnObject(g5,g-2)
    c: Horizontal(g1)
    c: Vertical(g2)
    c: Horizontal(g3)
    c: DistanceX(g5,g8) = 3.9
    c: DistanceY(g11,g8) = 3.9
    c: PointOnObject(g5,g0)
    c: PointOnObject(g5,g1)
    c: Tangent(g0,g4) = 1.5708
    c: Tangent(g1,g4) = 1.5708
    c: Coincident(g6,g0)
    c: Coincident(g6,g1)
    c: PointOnObject(g8,g2)
    c: PointOnObject(g8,g1)
    c: Tangent(g2,g7) = 1.5708
    c: Tangent(g1,g7) = 1.5708
    c: Coincident(g9,g2)
    c: Coincident(g9,g1)
    c: PointOnObject(g11,g2)
    c: PointOnObject(g11,g3)
    c: Tangent(g2,g10) = 1.5708
    c: Tangent(g3,g10) = 1.5708
    c: Coincident(g12,g2)
    c: Coincident(g12,g3)
    c: PointOnObject(g14,g0)
    c: PointOnObject(g14,g3)
    c: Tangent(g0,g13) = 1.5708
    c: Tangent(g3,g13) = 1.5708
    c: Coincident(g15,g0)
    c: Coincident(g15,g3)
    c: Equal(g6,g9)
    c: Equal(g9,g12)
    c: Equal(g12,g15)
    c: DistanceX(g14,g3) = 0.8
FEATURE [PartDesign::Pad] Pad030
  Direction = (0,-1,2e-16)
  Length = 25.2
  Length2 = 10
  Midplane = true
  Placement = pos=(0,0,0) rot=(1,0,0;1.5708rad)
  Profile = -> Sketch135
  ReferenceAxis = -> Sketch135 [N_Axis]
  Refine = true
  Suppressed = false
  Type = 0
FEATURE [PartDesign::Body] Body009  label="perno fermo switch - caricabatterie - grilletto"
  AllowCompound = false
  Group = -> [Sketch135,Pad030]
  Origin = -> Origin009
  Tip = -> Pad030
FEATURE [Sketcher::SketchObject] Sketch136  label="scavo_rele"
  ArcFitTolerance = 1e-06
  AttachmentSupport = -> [XZ_Plane]
  ExternalGeometry = -> [Sketch]
  FullyConstrained = true
  MakeInternals = false
  MapMode = 5
  Placement = pos=(0,0,0) rot=(1,0,0;1.5708rad)
  sketch-geometry (7):
    g0: LineSegment [constr] StartX=-168.686 StartY=-49.3292 StartZ=0 EndX=-170.664 EndY=-55.416 EndZ=0
    g1: LineSegment [constr] StartX=-168.686 StartY=-49.3292 StartZ=0 EndX=-164.882 EndY=-50.5653 EndZ=0
    g2: LineSegment [constr] StartX=-168.686 StartY=-49.3292 StartZ=0 EndX=-172.3 EndY=-48.155 EndZ=0
    g3: LineSegment StartX=-172.3 StartY=-48.155 StartZ=0 EndX=-164.882 EndY=-50.5653 EndZ=0
    g4: LineSegment StartX=-172.3 StartY=-48.155 StartZ=0 EndX=-174.278 EndY=-54.2417 EndZ=0
    g5: LineSegment StartX=-164.882 StartY=-50.5653 StartZ=0 EndX=-166.86 EndY=-56.6521 EndZ=0
    g6: LineSegment StartX=-174.278 StartY=-54.2417 StartZ=0 EndX=-166.86 EndY=-56.6521 EndZ=0
  constraints (19):
    c: Tangent(g0,g-3)
    c: Distance(g0,g-3) = 75
    c: Distance(g0,g0) = 6.4
    c: Coincident(g1,g0)
    c: Coincident(g2,g0)
    c: Distance(g2) = 3.8
    c: Distance(g1) = 4
    c: Perpendicular(g0,g1)
    c: Perpendicular(g0,g2)
    c: Coincident(g3,g2)
    c: Coincident(g3,g1)
    c: Equal(g4,g0)
    c: Equal(g5,g0)
    c: Parallel(g4,g0)
    c: Parallel(g5,g0)
    c: Coincident(g4,g2)
    c: Coincident(g5,g1)
    c: Coincident(g6,g4)
    c: Coincident(g6,g5)
FEATURE [Part::Extrusion] Extrude076  label="Extrude076 - scavo_rele"
  Base = -> Sketch136
  Dir = (0,-1,2e-16)
  DirMode = 2
  FaceMakerClass = Part::FaceMakerBullseye
  FaceMakerMode = 3
  LengthFwd = 10.4
  LengthRev = 0
  Solid = true
  Symmetric = true
FEATURE [Sketcher::SketchObject] Sketch137  label="scavo_nuovo_driver"
  ArcFitTolerance = 1e-06
  AttachmentSupport = -> [XZ_Plane]
  ExternalGeometry = -> [Sketch]
  FullyConstrained = true
  MakeInternals = false
  MapMode = 5
  Placement = pos=(0,0,0) rot=(1,0,0;1.5708rad)
  sketch-geometry (7):
    g0: LineSegment [constr] StartX=-171.776 StartY=-58.8398 StartZ=0 EndX=-175.794 EndY=-71.2035 EndZ=0
    g1: LineSegment [constr] StartX=-171.776 StartY=-58.8398 StartZ=0 EndX=-170.255 EndY=-59.3342 EndZ=0
    g2: LineSegment [constr] StartX=-171.776 StartY=-58.8398 StartZ=0 EndX=-175.39 EndY=-57.6655 EndZ=0
    g3: LineSegment StartX=-175.39 StartY=-57.6655 StartZ=0 EndX=-170.255 EndY=-59.3342 EndZ=0
    g4: LineSegment StartX=-175.39 StartY=-57.6655 StartZ=0 EndX=-179.408 EndY=-70.0293 EndZ=0
    g5: LineSegment StartX=-170.255 StartY=-59.3342 StartZ=0 EndX=-174.272 EndY=-71.698 EndZ=0
    g6: LineSegment StartX=-179.408 StartY=-70.0293 StartZ=0 EndX=-174.272 EndY=-71.698 EndZ=0
  constraints (19):
    c: Distance(g0,g-3) = 85
    c: Distance(g0) = 13
    c: Tangent(g0,g-3)
    c: Coincident(g1,g0)
    c: Coincident(g2,g0)
    c: Distance(g1) = 1.6
    c: Distance(g2) = 3.8
    c: Perpendicular(g0,g1)
    c: Perpendicular(g0,g2)
    c: Coincident(g3,g2)
    c: Coincident(g3,g1)
    c: Equal(g4,g0)
    c: Equal(g5,g0)
    c: Parallel(g4,g0)
    c: Parallel(g5,g0)
    c: Coincident(g4,g2)
    c: Coincident(g5,g1)
    c: Coincident(g6,g4)
    c: Coincident(g6,g5)
FEATURE [Part::Extrusion] Extrude077  label="Extrude077 - scavo_nuovo_driver"
  Base = -> Sketch137
  Dir = (0,-1,2e-16)
  DirMode = 2
  FaceMakerClass = Part::FaceMakerBullseye
  FaceMakerMode = 3
  LengthFwd = 16.8
  LengthRev = 0
  Solid = true
  Symmetric = true
FEATURE [Sketcher::SketchObject] Sketch138  label="scavo_nuovo_driver_alto"
  ArcFitTolerance = 1e-06
  AttachmentSupport = -> [XZ_Plane]
  ExternalGeometry = -> [Sketch]
  FullyConstrained = true
  MakeInternals = false
  MapMode = 5
  Placement = pos=(0,0,0) rot=(1,0,0;1.5708rad)
  sketch-geometry (7):
    g0: LineSegment [constr] StartX=-188.796 StartY=17.7274 StartZ=0 EndX=-187.75 EndY=4.97025 EndZ=0
    g1: LineSegment StartX=-187.75 StartY=4.97025 StartZ=0 EndX=-189.743 EndY=4.8067 EndZ=0
    g2: LineSegment StartX=-187.75 StartY=4.97025 StartZ=0 EndX=-182.766 EndY=5.37913 EndZ=0
    g3: LineSegment StartX=-190.79 StartY=17.5638 StartZ=0 EndX=-189.743 EndY=4.8067 EndZ=0
    g4: LineSegment StartX=-183.813 StartY=18.1363 StartZ=0 EndX=-182.766 EndY=5.37913 EndZ=0
    g5: LineSegment StartX=-190.79 StartY=17.5638 StartZ=0 EndX=-188.796 EndY=17.7274 EndZ=0
    g6: LineSegment StartX=-188.796 StartY=17.7274 StartZ=0 EndX=-183.813 EndY=18.1363 EndZ=0
  constraints (20):
    c: Distance(g0) = 12.8
    c: DistanceY(g-3,g0) = 9
    c: PointOnObject(g0,g-4)
    c: PointOnObject(g0,g-4)
    c: Coincident(g1,g0)
    c: Coincident(g2,g0)
    c: Distance(g1) = 2
    c: Distance(g2) = 5
    c: Perpendicular(g0,g1)
    c: Perpendicular(g0,g2)
    c: Equal(g3,g0)
    c: Parallel(g3,g0)
    c: Coincident(g3,g1)
    c: Equal(g4,g0)
    c: Parallel(g4,g0)
    c: Coincident(g4,g2)
    c: Coincident(g5,g3)
    c: Coincident(g5,g0)
    c: Coincident(g6,g0)
    c: Coincident(g6,g4)
FEATURE [Part::Extrusion] Extrude078  label="Extrude078 - scavo_nuovo_driver_alto"
  Base = -> Sketch138
  Dir = (0,-1,2e-16)
  DirMode = 2
  FaceMakerClass = Part::FaceMakerBullseye
  FaceMakerMode = 3
  LengthFwd = 16.4
  LengthRev = 0
  Solid = true
  Symmetric = true
FEATURE [Sketcher::SketchObject] Sketch139  label="fermi_nuovo_driver_alto"
  ArcFitTolerance = 1e-06
  AttachmentSupport = -> [XZ_Plane]
  ExternalGeometry = -> [Sketch138,Sketch]
  FullyConstrained = true
  MakeInternals = false
  MapMode = 5
  Placement = pos=(0,0,0) rot=(1,0,0;1.5708rad)
  sketch-geometry (17):
    g0: LineSegment [constr] StartX=-188.39 StartY=16.7251 StartZ=0 EndX=-187.935 EndY=14.0638 EndZ=0
    g1: LineSegment [constr] StartX=-187.935 StartY=14.0638 StartZ=0 EndX=-187.479 EndY=11.4025 EndZ=0
    g2: LineSegment StartX=-187.935 StartY=14.0638 StartZ=0 EndX=-187.749 EndY=12.9796 EndZ=0
    g3: LineSegment StartX=-187.935 StartY=14.0638 StartZ=0 EndX=-188.12 EndY=15.1481 EndZ=0
    g4: LineSegment StartX=-187.749 StartY=12.9796 StartZ=0 EndX=-185.581 EndY=13.3507 EndZ=0
    g5: LineSegment StartX=-188.12 StartY=15.1481 StartZ=0 EndX=-185.952 EndY=15.5192 EndZ=0
    g6: LineSegment StartX=-185.952 StartY=15.5192 StartZ=0 EndX=-185.581 EndY=13.3507 EndZ=0
    g7: LineSegment StartX=-187.479 StartY=11.4025 StartZ=0 EndX=-189.056 EndY=11.1326 EndZ=0
    g8: LineSegment StartX=-188.39 StartY=16.7251 StartZ=0 EndX=-189.967 EndY=16.4552 EndZ=0
    g9: LineSegment StartX=-189.967 StartY=16.4552 StartZ=0 EndX=-189.056 EndY=11.1326 EndZ=0
    g10: LineSegment StartX=-187.479 StartY=11.4025 StartZ=0 EndX=-185.311 EndY=11.7737 EndZ=0
    g11: LineSegment StartX=-188.39 StartY=16.7251 StartZ=0 EndX=-186.222 EndY=17.0963 EndZ=0
    g12: LineSegment StartX=-184.375 StartY=15.7891 StartZ=0 EndX=-184.004 EndY=13.6206 EndZ=0
    g13: ArcOfCircle CenterX=-185.952 CenterY=15.5192 CenterZ=0 NormalX=0 NormalY=0 NormalZ=1 AngleXU=0 Radius=1.6 StartAngle=0.169508 EndAngle=1.7403
    g14: GeomPoint [constr] X=-184.645 Y=17.3662 Z=0
    g15: ArcOfCircle CenterX=-185.581 CenterY=13.3507 CenterZ=0 NormalX=0 NormalY=0 NormalZ=1 AngleXU=0 Radius=1.6 StartAngle=4.8819 EndAngle=6.45269
    g16: GeomPoint [constr] X=-183.734 Y=12.0436 Z=0
  constraints (43):
    c: Tangent(g1,g0) = -1.5708
    c: Distance(g0) = 2.7
    c: Equal(g1,g0)
    c: Tangent(g1,g-5)
    c: Coincident(g2,g0)
    c: Coincident(g3,g0)
    c: Distance(g2) = 1.1
    c: Equal(g3,g2)
    c: PointOnObject(g3,g2)
    c: Coincident(g4,g2)
    c: Coincident(g5,g3)
    c: Distance(g4) = 2.2
    c: Equal(g4,g5)
    c: Perpendicular(g1,g4)
    c: Perpendicular(g0,g5)
    c: Coincident(g6,g5)
    c: Coincident(g6,g4)
    c: Coincident(g7,g1)
    c: Coincident(g8,g0)
    c: Distance(g7) = 1.6
    c: Equal(g7,g8)
    c: Perpendicular(g1,g7)
    c: Perpendicular(g8,g0)
    c: Coincident(g9,g8)
    c: Coincident(g9,g7)
    c: Coincident(g10,g1)
    c: Coincident(g11,g0)
    c: Distance(g10,g16) = 3.8
    c: Perpendicular(g1,g10)
    c: Perpendicular(g1,g11)
    c: DistanceY(g0,g-4) = 3.5
    c: PointOnObject(g14,g12)
    c: PointOnObject(g14,g11)
    c: Tangent(g12,g13) = 1.5708
    c: Tangent(g11,g13) = 1.5708
    c: PointOnObject(g16,g12)
    c: PointOnObject(g16,g10)
    c: Tangent(g12,g15) = 1.5708
    c: Tangent(g10,g15) = -1.5708
    c: Equal(g13,g15)
    c: Coincident(g13,g5)
    c: Parallel(g2,g0)
    c: PointOnObject(g0,g-5)
FEATURE [Part::Extrusion] Extrude079  label="Extrude079 - fermi_nuovo_driver_alto"
  Base = -> Sketch139
  Dir = (0,-1,2e-16)
  DirMode = 2
  FaceMakerClass = Part::FaceMakerBullseye
  FaceMakerMode = 3
  LengthFwd = 25.2
  LengthRev = 0
  Solid = true
  Symmetric = true
FEATURE [Sketcher::SketchObject] Sketch140  label="scavo_diodo_nuovo_driver_alto"
  ArcFitTolerance = 1e-06
  AttachmentSupport = -> [XZ_Plane]
  ExternalGeometry = -> [Sketch138]
  FullyConstrained = true
  MakeInternals = false
  MapMode = 5
  Placement = pos=(0,0,0) rot=(1,0,0;1.5708rad)
  sketch-geometry (4):
    g0: LineSegment StartX=-190.79 StartY=17.5638 StartZ=0 EndX=-189.743 EndY=4.8067 EndZ=0
    g1: LineSegment StartX=-193.78 StartY=17.3185 StartZ=0 EndX=-192.733 EndY=4.56137 EndZ=0
    g2: LineSegment StartX=-190.79 StartY=17.5638 StartZ=0 EndX=-193.78 EndY=17.3185 EndZ=0
    g3: LineSegment StartX=-192.733 StartY=4.56137 StartZ=0 EndX=-189.743 EndY=4.8067 EndZ=0
  constraints (11):
    c: Equal(g0,g-3)
    c: Parallel(g0,g-3)
    c: Equal(g1,g-3)
    c: Parallel(g1,g-3)
    c: Coincident(g2,g0)
    c: Distance(g2) = 3
    c: Perpendicular(g0,g2)
    c: Coincident(g1,g2)
    c: Coincident(g3,g1)
    c: Coincident(g3,g0)
    c: Coincident(g0,g-3)
FEATURE [PartDesign::Body] Body  label="Struttura pistola"
  AllowCompound = false
  Group = -> [Sketch,Sketch002,Sketch004,DatumPlane,Sketch005,DatumPlane001,CopyCut,Sketch008,Sketch009,Sketch010,Sketch011,Sketch012,Sketch013,Sketch014,Sketch015,Sketch016,Sketch017,Sketch018,Sketch019,Sketch020,Sketch022,Sketch023,Sketch024,Sketch025,Sketch026,Sketch027,Sketch029,Sketch030,Sketch031,Sketch032,Sketch033,Sketch034,Sketch035,Sketch036,Sketch037,Sketch038,Sketch039,Sketch040,Sketch041,Sketch042,+20 more]
  Origin = -> Origin
FEATURE [Part::Extrusion] Extrude080  label="Extrude080 - scavo_diodo_nuovo_driver_alto"
  Base = -> Sketch140
  Dir = (0,-1,2e-16)
  DirMode = 2
  FaceMakerClass = Part::FaceMakerBullseye
  FaceMakerMode = 3
  LengthFwd = 4
  LengthRev = 0
  Placement = pos=(0,7.8,0) rot=(0,0,1;0rad)
  Solid = true
  Symmetric = false
note: 2 file-system paths scrubbed to <path> (originals preserved in the JSON sidecar)
